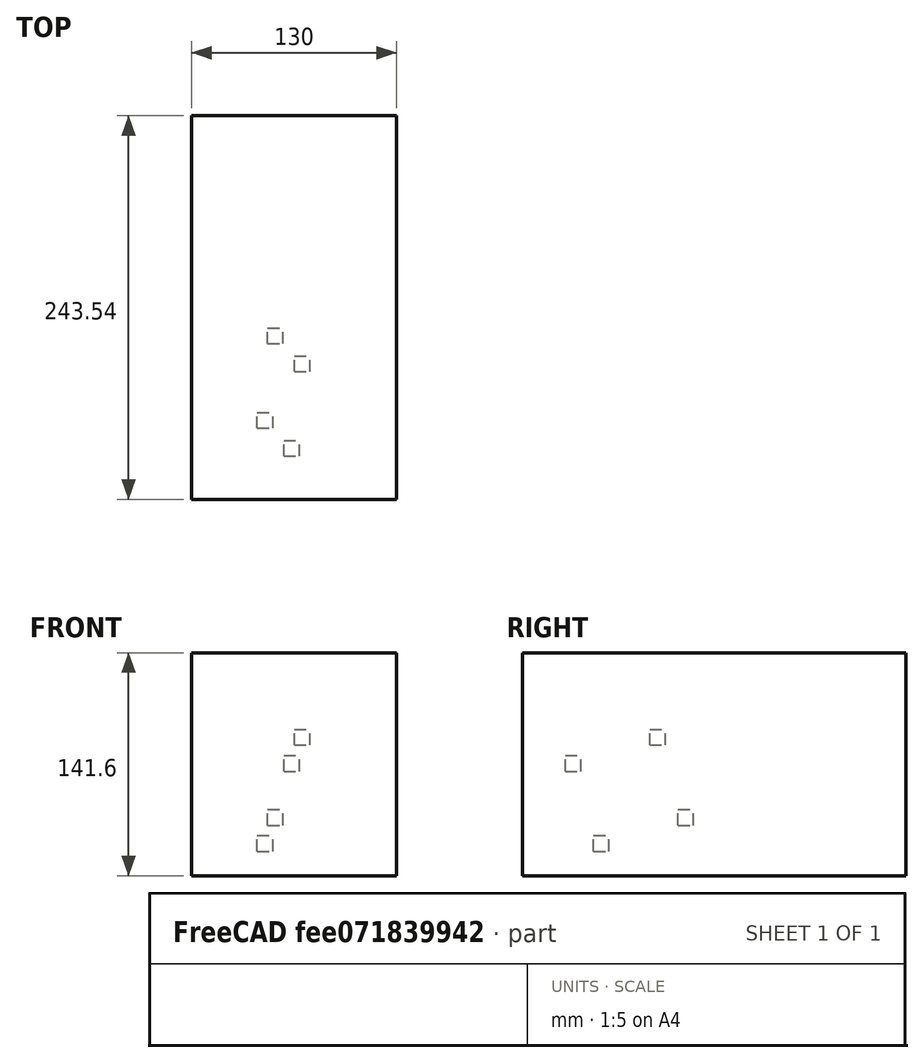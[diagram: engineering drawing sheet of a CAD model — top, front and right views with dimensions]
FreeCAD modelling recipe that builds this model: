
FCSTD DOCUMENT  (FreeCAD 1.0R39109 (Git))
Label: PathArray2
License: All rights reserved
LicenseURL: http://en.wikipedia.org/wiki/All_rights_reserved
objects: App::DocumentObjectGroupPython×1251, Part::FeaturePython×3, App::Part×2, Part::Part2DObjectPython×1
note: 4 computed .brp shape members not serialized (recipe doc carries the construction recipe); baked Part::Feature solids carry a one-line shape summary decoded from their .brp

FEATURE [App::DocumentObjectGroupPython] HALFPI  # scripted group (container) (typed FeaturePython)
  name = HALFPI
  value = pi/2.
FEATURE [App::DocumentObjectGroupPython] PI  # scripted group (container) (typed FeaturePython)
  name = PI
  value = 1.*pi
FEATURE [App::DocumentObjectGroupPython] TWOPI  # scripted group (container) (typed FeaturePython)
  name = TWOPI
  value = 2.*pi
FEATURE [App::DocumentObjectGroupPython] Constants  # scripted group (container) (typed FeaturePython)
  Group = -> [HALFPI,PI,TWOPI]
FEATURE [App::DocumentObjectGroupPython] Variables  # scripted group (container) (typed FeaturePython)
FEATURE [App::DocumentObjectGroupPython] Quantities  # scripted group (container) (typed FeaturePython)
FEATURE [App::DocumentObjectGroupPython] Isotopes  # scripted group (container) (typed FeaturePython)
FEATURE [App::DocumentObjectGroupPython] Elements  # scripted group (container) (typed FeaturePython)
FEATURE [App::DocumentObjectGroupPython] Matrix  # scripted group (container) (typed FeaturePython)
FEATURE [App::DocumentObjectGroupPython] Surfaces  # scripted group (container) (typed FeaturePython)
FEATURE [App::DocumentObjectGroupPython] Opticals  # scripted group (container) (typed FeaturePython)
  Group = -> [Matrix,Surfaces]
FEATURE [App::DocumentObjectGroupPython] G4Isotopes  # scripted group (container) (typed FeaturePython)
FEATURE [App::DocumentObjectGroupPython] H_element  # scripted group (container) (typed FeaturePython)
  Z = 1
  atom_value = 1.008
  formula = H
  name = H_element
FEATURE [App::DocumentObjectGroupPython] He_element  # scripted group (container) (typed FeaturePython)
  Z = 2
  atom_value = 4.0026
  formula = He
  name = He_element
FEATURE [App::DocumentObjectGroupPython] Li_element  # scripted group (container) (typed FeaturePython)
  Z = 3
  atom_value = 6.94
  formula = Li
  name = Li_element
FEATURE [App::DocumentObjectGroupPython] Be_element  # scripted group (container) (typed FeaturePython)
  Z = 4
  atom_value = 9.01218
  formula = Be
  name = Be_element
FEATURE [App::DocumentObjectGroupPython] B_element  # scripted group (container) (typed FeaturePython)
  Z = 5
  atom_value = 10.81
  formula = B
  name = B_element
FEATURE [App::DocumentObjectGroupPython] C_element  # scripted group (container) (typed FeaturePython)
  Z = 6
  atom_value = 12.011
  formula = C
  name = C_element
FEATURE [App::DocumentObjectGroupPython] N_element  # scripted group (container) (typed FeaturePython)
  Z = 7
  atom_value = 14.007
  formula = N
  name = N_element
FEATURE [App::DocumentObjectGroupPython] O_element  # scripted group (container) (typed FeaturePython)
  Z = 8
  atom_value = 15.999
  formula = O
  name = O_element
FEATURE [App::DocumentObjectGroupPython] F_element  # scripted group (container) (typed FeaturePython)
  Z = 9
  atom_value = 18.9984
  formula = F
  name = F_element
FEATURE [App::DocumentObjectGroupPython] Ne_element  # scripted group (container) (typed FeaturePython)
  Z = 10
  atom_value = 20.1797
  formula = Ne
  name = Ne_element
FEATURE [App::DocumentObjectGroupPython] Na_element  # scripted group (container) (typed FeaturePython)
  Z = 11
  atom_value = 22.9898
  formula = Na
  name = Na_element
FEATURE [App::DocumentObjectGroupPython] Mg_element  # scripted group (container) (typed FeaturePython)
  Z = 12
  atom_value = 24.305
  formula = Mg
  name = Mg_element
FEATURE [App::DocumentObjectGroupPython] Al_element  # scripted group (container) (typed FeaturePython)
  Z = 13
  atom_value = 26.9815
  formula = Al
  name = Al_element
FEATURE [App::DocumentObjectGroupPython] Si_element  # scripted group (container) (typed FeaturePython)
  Z = 14
  atom_value = 28.085
  formula = Si
  name = Si_element
FEATURE [App::DocumentObjectGroupPython] P_element  # scripted group (container) (typed FeaturePython)
  Z = 15
  atom_value = 30.9738
  formula = P
  name = P_element
FEATURE [App::DocumentObjectGroupPython] S_element  # scripted group (container) (typed FeaturePython)
  Z = 16
  atom_value = 32.06
  formula = S
  name = S_element
FEATURE [App::DocumentObjectGroupPython] Cl_element  # scripted group (container) (typed FeaturePython)
  Z = 17
  atom_value = 35.45
  formula = Cl
  name = Cl_element
FEATURE [App::DocumentObjectGroupPython] Ar_element  # scripted group (container) (typed FeaturePython)
  Z = 18
  atom_value = 39.95
  formula = Ar
  name = Ar_element
FEATURE [App::DocumentObjectGroupPython] K_element  # scripted group (container) (typed FeaturePython)
  Z = 19
  atom_value = 39.0983
  formula = K
  name = K_element
FEATURE [App::DocumentObjectGroupPython] Ca_element  # scripted group (container) (typed FeaturePython)
  Z = 20
  atom_value = 40.078
  formula = Ca
  name = Ca_element
FEATURE [App::DocumentObjectGroupPython] Sc_element  # scripted group (container) (typed FeaturePython)
  Z = 21
  atom_value = 44.9559
  formula = Sc
  name = Sc_element
FEATURE [App::DocumentObjectGroupPython] Ti_element  # scripted group (container) (typed FeaturePython)
  Z = 22
  atom_value = 47.867
  formula = Ti
  name = Ti_element
FEATURE [App::DocumentObjectGroupPython] V_element  # scripted group (container) (typed FeaturePython)
  Z = 23
  atom_value = 50.9415
  formula = V
  name = V_element
FEATURE [App::DocumentObjectGroupPython] Cr_element  # scripted group (container) (typed FeaturePython)
  Z = 24
  atom_value = 51.9961
  formula = Cr
  name = Cr_element
FEATURE [App::DocumentObjectGroupPython] Mn_element  # scripted group (container) (typed FeaturePython)
  Z = 25
  atom_value = 54.938
  formula = Mn
  name = Mn_element
FEATURE [App::DocumentObjectGroupPython] Fe_element  # scripted group (container) (typed FeaturePython)
  Z = 26
  atom_value = 55.845
  formula = Fe
  name = Fe_element
FEATURE [App::DocumentObjectGroupPython] Co_element  # scripted group (container) (typed FeaturePython)
  Z = 27
  atom_value = 58.9332
  formula = Co
  name = Co_element
FEATURE [App::DocumentObjectGroupPython] Ni_element  # scripted group (container) (typed FeaturePython)
  Z = 28
  atom_value = 58.6934
  formula = Ni
  name = Ni_element
FEATURE [App::DocumentObjectGroupPython] Cu_element  # scripted group (container) (typed FeaturePython)
  Z = 29
  atom_value = 63.546
  formula = Cu
  name = Cu_element
FEATURE [App::DocumentObjectGroupPython] Zn_element  # scripted group (container) (typed FeaturePython)
  Z = 30
  atom_value = 65.38
  formula = Zn
  name = Zn_element
FEATURE [App::DocumentObjectGroupPython] Ga_element  # scripted group (container) (typed FeaturePython)
  Z = 31
  atom_value = 69.723
  formula = Ga
  name = Ga_element
FEATURE [App::DocumentObjectGroupPython] Ge_element  # scripted group (container) (typed FeaturePython)
  Z = 32
  atom_value = 72.63
  formula = Ge
  name = Ge_element
FEATURE [App::DocumentObjectGroupPython] As_element  # scripted group (container) (typed FeaturePython)
  Z = 33
  atom_value = 74.9216
  formula = As
  name = As_element
FEATURE [App::DocumentObjectGroupPython] Se_element  # scripted group (container) (typed FeaturePython)
  Z = 34
  atom_value = 78.971
  formula = Se
  name = Se_element
FEATURE [App::DocumentObjectGroupPython] Br_element  # scripted group (container) (typed FeaturePython)
  Z = 35
  atom_value = 79.904
  formula = Br
  name = Br_element
FEATURE [App::DocumentObjectGroupPython] Kr_element  # scripted group (container) (typed FeaturePython)
  Z = 36
  atom_value = 83.798
  formula = Kr
  name = Kr_element
FEATURE [App::DocumentObjectGroupPython] Rb_element  # scripted group (container) (typed FeaturePython)
  Z = 37
  atom_value = 85.4678
  formula = Rb
  name = Rb_element
FEATURE [App::DocumentObjectGroupPython] Sr_element  # scripted group (container) (typed FeaturePython)
  Z = 38
  atom_value = 87.62
  formula = Sr
  name = Sr_element
FEATURE [App::DocumentObjectGroupPython] Y_element  # scripted group (container) (typed FeaturePython)
  Z = 39
  atom_value = 88.9058
  formula = Y
  name = Y_element
FEATURE [App::DocumentObjectGroupPython] Zr_element  # scripted group (container) (typed FeaturePython)
  Z = 40
  atom_value = 91.224
  formula = Zr
  name = Zr_element
FEATURE [App::DocumentObjectGroupPython] Nb_element  # scripted group (container) (typed FeaturePython)
  Z = 41
  atom_value = 92.9064
  formula = Nb
  name = Nb_element
FEATURE [App::DocumentObjectGroupPython] Mo_element  # scripted group (container) (typed FeaturePython)
  Z = 42
  atom_value = 95.95
  formula = Mo
  name = Mo_element
FEATURE [App::DocumentObjectGroupPython] Tc_element  # scripted group (container) (typed FeaturePython)
  Z = 43
  atom_value = 97
  formula = Tc
  name = Tc_element
FEATURE [App::DocumentObjectGroupPython] Ru_element  # scripted group (container) (typed FeaturePython)
  Z = 44
  atom_value = 101.07
  formula = Ru
  name = Ru_element
FEATURE [App::DocumentObjectGroupPython] Rh_element  # scripted group (container) (typed FeaturePython)
  Z = 45
  atom_value = 102.905
  formula = Rh
  name = Rh_element
FEATURE [App::DocumentObjectGroupPython] Pd_element  # scripted group (container) (typed FeaturePython)
  Z = 46
  atom_value = 106.42
  formula = Pd
  name = Pd_element
FEATURE [App::DocumentObjectGroupPython] Ag_element  # scripted group (container) (typed FeaturePython)
  Z = 47
  atom_value = 107.868
  formula = Ag
  name = Ag_element
FEATURE [App::DocumentObjectGroupPython] Cd_element  # scripted group (container) (typed FeaturePython)
  Z = 48
  atom_value = 112.414
  formula = Cd
  name = Cd_element
FEATURE [App::DocumentObjectGroupPython] In_element  # scripted group (container) (typed FeaturePython)
  Z = 49
  atom_value = 114.818
  formula = In
  name = In_element
FEATURE [App::DocumentObjectGroupPython] Sn_element  # scripted group (container) (typed FeaturePython)
  Z = 50
  atom_value = 118.71
  formula = Sn
  name = Sn_element
FEATURE [App::DocumentObjectGroupPython] Sb_element  # scripted group (container) (typed FeaturePython)
  Z = 51
  atom_value = 121.76
  formula = Sb
  name = Sb_element
FEATURE [App::DocumentObjectGroupPython] Te_element  # scripted group (container) (typed FeaturePython)
  Z = 52
  atom_value = 127.6
  formula = Te
  name = Te_element
FEATURE [App::DocumentObjectGroupPython] I_element  # scripted group (container) (typed FeaturePython)
  Z = 53
  atom_value = 126.904
  formula = I
  name = I_element
FEATURE [App::DocumentObjectGroupPython] Xe_element  # scripted group (container) (typed FeaturePython)
  Z = 54
  atom_value = 131.293
  formula = Xe
  name = Xe_element
FEATURE [App::DocumentObjectGroupPython] Cs_element  # scripted group (container) (typed FeaturePython)
  Z = 55
  atom_value = 132.905
  formula = Cs
  name = Cs_element
FEATURE [App::DocumentObjectGroupPython] Ba_element  # scripted group (container) (typed FeaturePython)
  Z = 56
  atom_value = 137.327
  formula = Ba
  name = Ba_element
FEATURE [App::DocumentObjectGroupPython] La_element  # scripted group (container) (typed FeaturePython)
  Z = 57
  atom_value = 138.905
  formula = La
  name = La_element
FEATURE [App::DocumentObjectGroupPython] Ce_element  # scripted group (container) (typed FeaturePython)
  Z = 58
  atom_value = 140.116
  formula = Ce
  name = Ce_element
FEATURE [App::DocumentObjectGroupPython] Pr_element  # scripted group (container) (typed FeaturePython)
  Z = 59
  atom_value = 140.908
  formula = Pr
  name = Pr_element
FEATURE [App::DocumentObjectGroupPython] Nd_element  # scripted group (container) (typed FeaturePython)
  Z = 60
  atom_value = 144.242
  formula = Nd
  name = Nd_element
FEATURE [App::DocumentObjectGroupPython] Pm_element  # scripted group (container) (typed FeaturePython)
  Z = 61
  atom_value = 145
  formula = Pm
  name = Pm_element
FEATURE [App::DocumentObjectGroupPython] Sm_element  # scripted group (container) (typed FeaturePython)
  Z = 62
  atom_value = 150.36
  formula = Sm
  name = Sm_element
FEATURE [App::DocumentObjectGroupPython] Eu_element  # scripted group (container) (typed FeaturePython)
  Z = 63
  atom_value = 151.964
  formula = Eu
  name = Eu_element
FEATURE [App::DocumentObjectGroupPython] Gd_element  # scripted group (container) (typed FeaturePython)
  Z = 64
  atom_value = 157.25
  formula = Gd
  name = Gd_element
FEATURE [App::DocumentObjectGroupPython] Tb_element  # scripted group (container) (typed FeaturePython)
  Z = 65
  atom_value = 158.925
  formula = Tb
  name = Tb_element
FEATURE [App::DocumentObjectGroupPython] Dy_element  # scripted group (container) (typed FeaturePython)
  Z = 66
  atom_value = 162.5
  formula = Dy
  name = Dy_element
FEATURE [App::DocumentObjectGroupPython] Ho_element  # scripted group (container) (typed FeaturePython)
  Z = 67
  atom_value = 164.93
  formula = Ho
  name = Ho_element
FEATURE [App::DocumentObjectGroupPython] Er_element  # scripted group (container) (typed FeaturePython)
  Z = 68
  atom_value = 167.259
  formula = Er
  name = Er_element
FEATURE [App::DocumentObjectGroupPython] Tm_element  # scripted group (container) (typed FeaturePython)
  Z = 69
  atom_value = 168.934
  formula = Tm
  name = Tm_element
FEATURE [App::DocumentObjectGroupPython] Yb_element  # scripted group (container) (typed FeaturePython)
  Z = 70
  atom_value = 173.045
  formula = Yb
  name = Yb_element
FEATURE [App::DocumentObjectGroupPython] Lu_element  # scripted group (container) (typed FeaturePython)
  Z = 71
  atom_value = 174.967
  formula = Lu
  name = Lu_element
FEATURE [App::DocumentObjectGroupPython] Hf_element  # scripted group (container) (typed FeaturePython)
  Z = 72
  atom_value = 178.49
  formula = Hf
  name = Hf_element
FEATURE [App::DocumentObjectGroupPython] Ta_element  # scripted group (container) (typed FeaturePython)
  Z = 73
  atom_value = 180.948
  formula = Ta
  name = Ta_element
FEATURE [App::DocumentObjectGroupPython] W_element  # scripted group (container) (typed FeaturePython)
  Z = 74
  atom_value = 183.84
  formula = W
  name = W_element
FEATURE [App::DocumentObjectGroupPython] Re_element  # scripted group (container) (typed FeaturePython)
  Z = 75
  atom_value = 186.207
  formula = Re
  name = Re_element
FEATURE [App::DocumentObjectGroupPython] Os_element  # scripted group (container) (typed FeaturePython)
  Z = 76
  atom_value = 190.23
  formula = Os
  name = Os_element
FEATURE [App::DocumentObjectGroupPython] Ir_element  # scripted group (container) (typed FeaturePython)
  Z = 77
  atom_value = 192.217
  formula = Ir
  name = Ir_element
FEATURE [App::DocumentObjectGroupPython] Pt_element  # scripted group (container) (typed FeaturePython)
  Z = 78
  atom_value = 195.084
  formula = Pt
  name = Pt_element
FEATURE [App::DocumentObjectGroupPython] Au_element  # scripted group (container) (typed FeaturePython)
  Z = 79
  atom_value = 196.967
  formula = Au
  name = Au_element
FEATURE [App::DocumentObjectGroupPython] Hg_element  # scripted group (container) (typed FeaturePython)
  Z = 80
  atom_value = 200.592
  formula = Hg
  name = Hg_element
FEATURE [App::DocumentObjectGroupPython] Tl_element  # scripted group (container) (typed FeaturePython)
  Z = 81
  atom_value = 204.38
  formula = Tl
  name = Tl_element
FEATURE [App::DocumentObjectGroupPython] Pb_element  # scripted group (container) (typed FeaturePython)
  Z = 82
  atom_value = 207.2
  formula = Pb
  name = Pb_element
FEATURE [App::DocumentObjectGroupPython] Bi_element  # scripted group (container) (typed FeaturePython)
  Z = 83
  atom_value = 208.98
  formula = Bi
  name = Bi_element
FEATURE [App::DocumentObjectGroupPython] Po_element  # scripted group (container) (typed FeaturePython)
  Z = 84
  atom_value = 209
  formula = Po
  name = Po_element
FEATURE [App::DocumentObjectGroupPython] At_element  # scripted group (container) (typed FeaturePython)
  Z = 85
  atom_value = 210
  formula = At
  name = At_element
FEATURE [App::DocumentObjectGroupPython] Rn_element  # scripted group (container) (typed FeaturePython)
  Z = 86
  atom_value = 222
  formula = Rn
  name = Rn_element
FEATURE [App::DocumentObjectGroupPython] Fr_element  # scripted group (container) (typed FeaturePython)
  Z = 87
  atom_value = 223
  formula = Fr
  name = Fr_element
FEATURE [App::DocumentObjectGroupPython] Ra_element  # scripted group (container) (typed FeaturePython)
  Z = 88
  atom_value = 226
  formula = Ra
  name = Ra_element
FEATURE [App::DocumentObjectGroupPython] Ac_element  # scripted group (container) (typed FeaturePython)
  Z = 89
  atom_value = 227
  formula = Ac
  name = Ac_element
FEATURE [App::DocumentObjectGroupPython] Th_element  # scripted group (container) (typed FeaturePython)
  Z = 90
  atom_value = 232.038
  formula = Th
  name = Th_element
FEATURE [App::DocumentObjectGroupPython] Pa_element  # scripted group (container) (typed FeaturePython)
  Z = 91
  atom_value = 231.036
  formula = Pa
  name = Pa_element
FEATURE [App::DocumentObjectGroupPython] U_element  # scripted group (container) (typed FeaturePython)
  Z = 92
  atom_value = 238.029
  formula = U
  name = U_element
FEATURE [App::DocumentObjectGroupPython] Np_element  # scripted group (container) (typed FeaturePython)
  Z = 93
  atom_value = 237
  formula = Np
  name = Np_element
FEATURE [App::DocumentObjectGroupPython] Pu_element  # scripted group (container) (typed FeaturePython)
  Z = 94
  atom_value = 244
  formula = Pu
  name = Pu_element
FEATURE [App::DocumentObjectGroupPython] Am_element  # scripted group (container) (typed FeaturePython)
  Z = 95
  atom_value = 243
  formula = Am
  name = Am_element
FEATURE [App::DocumentObjectGroupPython] Cm_element  # scripted group (container) (typed FeaturePython)
  Z = 96
  atom_value = 247
  formula = Cm
  name = Cm_element
FEATURE [App::DocumentObjectGroupPython] Bk_element  # scripted group (container) (typed FeaturePython)
  Z = 97
  atom_value = 247
  formula = Bk
  name = Bk_element
FEATURE [App::DocumentObjectGroupPython] Cf_element  # scripted group (container) (typed FeaturePython)
  Z = 98
  atom_value = 251
  formula = Cf
  name = Cf_element
FEATURE [App::DocumentObjectGroupPython] G4Elements  # scripted group (container) (typed FeaturePython)
  Group = -> [H_element,He_element,Li_element,Be_element,B_element,C_element,N_element,O_element,F_element,Ne_element,Na_element,Mg_element,Al_element,Si_element,P_element,S_element,Cl_element,Ar_element,K_element,Ca_element,Sc_element,Ti_element,V_element,Cr_element,Mn_element,Fe_element,Co_element,Ni_element,Cu_element,Zn_element,Ga_element,Ge_element,As_element,Se_element,Br_element,Kr_element,Rb_element,+61 more]
FEATURE [App::DocumentObjectGroupPython] H_element001  label="H_element : 0.101"  # scripted group (container) (typed FeaturePython)
  n = 0.101327
FEATURE [App::DocumentObjectGroupPython] C_element001  label="C_element : 0.775"  # scripted group (container) (typed FeaturePython)
  n = 0.7755
FEATURE [App::DocumentObjectGroupPython] N_element001  label="N_element : 0.035"  # scripted group (container) (typed FeaturePython)
  n = 0.035057
FEATURE [App::DocumentObjectGroupPython] O_element001  label="O_element : 0.052"  # scripted group (container) (typed FeaturePython)
  n = 0.0523159
FEATURE [App::DocumentObjectGroupPython] F_element001  label="F_element : 0.017"  # scripted group (container) (typed FeaturePython)
  n = 0.017422
FEATURE [App::DocumentObjectGroupPython] Ca_element001  label="Ca_element : 0.018"  # scripted group (container) (typed FeaturePython)
  n = 0.018378
FEATURE [App::DocumentObjectGroupPython] G4_A_150_TISSUE  label="G4_A-150_TISSUE"  # scripted group (container) (typed FeaturePython)
  Dunit = g/cm3
  Dvalue = 1.127
  Group = -> [H_element001,C_element001,N_element001,O_element001,F_element001,Ca_element001]
  conduct = 2
  density = 1
  expand = 3
  formula = G4_A-150_TISSUE
  name = G4_A-150_TISSUE
  specific = 4
FEATURE [App::DocumentObjectGroupPython] C_element002  label="C_element : 3"  # scripted group (container) (typed FeaturePython)
  n = 3
  ref = C_element
FEATURE [App::DocumentObjectGroupPython] H_element002  label="H_element : 6"  # scripted group (container) (typed FeaturePython)
  n = 6
  ref = H_element
FEATURE [App::DocumentObjectGroupPython] O_element002  label="O_element : 1"  # scripted group (container) (typed FeaturePython)
  n = 1
  ref = O_element
FEATURE [App::DocumentObjectGroupPython] G4_ACETONE  # scripted group (container) (typed FeaturePython)
  Dunit = g/cm3
  Dvalue = 0.7899
  Group = -> [C_element002,H_element002,O_element002]
  conduct = 2
  density = 1
  expand = 3
  formula = G4_ACETONE
  name = G4_ACETONE
  specific = 4
FEATURE [App::DocumentObjectGroupPython] C_element003  label="C_element : 2"  # scripted group (container) (typed FeaturePython)
  n = 2
  ref = C_element
FEATURE [App::DocumentObjectGroupPython] H_element003  label="H_element : 2"  # scripted group (container) (typed FeaturePython)
  n = 2
  ref = H_element
FEATURE [App::DocumentObjectGroupPython] G4_ACETYLENE  # scripted group (container) (typed FeaturePython)
  Dunit = g/cm3
  Dvalue = 0.0010967
  Group = -> [C_element003,H_element003]
  conduct = 2
  density = 1
  expand = 3
  formula = G4_ACETYLENE
  name = G4_ACETYLENE
  specific = 4
FEATURE [App::DocumentObjectGroupPython] C_element004  label="C_element : 5"  # scripted group (container) (typed FeaturePython)
  n = 5
  ref = C_element
FEATURE [App::DocumentObjectGroupPython] H_element004  label="H_element : 5"  # scripted group (container) (typed FeaturePython)
  n = 5
  ref = H_element
FEATURE [App::DocumentObjectGroupPython] N_element002  label="N_element : 5"  # scripted group (container) (typed FeaturePython)
  n = 5
  ref = N_element
FEATURE [App::DocumentObjectGroupPython] G4_ADENINE  # scripted group (container) (typed FeaturePython)
  Dunit = g/cm3
  Dvalue = 1.6
  Group = -> [C_element004,H_element004,N_element002]
  conduct = 2
  density = 1
  expand = 3
  formula = G4_ADENINE
  name = G4_ADENINE
  specific = 4
FEATURE [App::DocumentObjectGroupPython] H_element005  label="H_element : 0.114"  # scripted group (container) (typed FeaturePython)
  n = 0.114
FEATURE [App::DocumentObjectGroupPython] C_element005  label="C_element : 0.598"  # scripted group (container) (typed FeaturePython)
  n = 0.598
FEATURE [App::DocumentObjectGroupPython] N_element003  label="N_element : 0.007"  # scripted group (container) (typed FeaturePython)
  n = 0.007
FEATURE [App::DocumentObjectGroupPython] O_element003  label="O_element : 0.278"  # scripted group (container) (typed FeaturePython)
  n = 0.278
FEATURE [App::DocumentObjectGroupPython] Na_element001  label="Na_element : 0.001"  # scripted group (container) (typed FeaturePython)
  n = 0.001
FEATURE [App::DocumentObjectGroupPython] S_element001  label="S_element : 0.001"  # scripted group (container) (typed FeaturePython)
  n = 0.001
FEATURE [App::DocumentObjectGroupPython] Cl_element001  label="Cl_element : 0.001"  # scripted group (container) (typed FeaturePython)
  n = 0.001
FEATURE [App::DocumentObjectGroupPython] G4_ADIPOSE_TISSUE_ICRP  # scripted group (container) (typed FeaturePython)
  Dunit = g/cm3
  Dvalue = 0.95
  Group = -> [H_element005,C_element005,N_element003,O_element003,Na_element001,S_element001,Cl_element001]
  conduct = 2
  density = 1
  expand = 3
  formula = G4_ADIPOSE_TISSUE_ICRP
  name = G4_ADIPOSE_TISSUE_ICRP
  specific = 4
FEATURE [App::DocumentObjectGroupPython] C_element006  label="C_element : 0.000"  # scripted group (container) (typed FeaturePython)
  n = 0.000124
FEATURE [App::DocumentObjectGroupPython] N_element004  label="N_element : 0.755"  # scripted group (container) (typed FeaturePython)
  n = 0.755268
FEATURE [App::DocumentObjectGroupPython] O_element004  label="O_element : 0.232"  # scripted group (container) (typed FeaturePython)
  n = 0.231781
FEATURE [App::DocumentObjectGroupPython] Ar_element001  label="Ar_element : 0.013"  # scripted group (container) (typed FeaturePython)
  n = 0.012827
FEATURE [App::DocumentObjectGroupPython] G4_AIR  # scripted group (container) (typed FeaturePython)
  Dunit = g/cm3
  Dvalue = 0.00120479
  Group = -> [C_element006,N_element004,O_element004,Ar_element001]
  conduct = 2
  density = 1
  expand = 3
  formula = G4_AIR
  name = G4_AIR
  specific = 4
FEATURE [App::DocumentObjectGroupPython] C_element007  label="C_element : 006"  # scripted group (container) (typed FeaturePython)
  n = 3
  ref = C_element
FEATURE [App::DocumentObjectGroupPython] H_element006  label="H_element : 7"  # scripted group (container) (typed FeaturePython)
  n = 7
  ref = H_element
FEATURE [App::DocumentObjectGroupPython] N_element005  label="N_element : 1"  # scripted group (container) (typed FeaturePython)
  n = 1
  ref = N_element
FEATURE [App::DocumentObjectGroupPython] O_element005  label="O_element : 2"  # scripted group (container) (typed FeaturePython)
  n = 2
  ref = O_element
FEATURE [App::DocumentObjectGroupPython] G4_ALANINE  # scripted group (container) (typed FeaturePython)
  Dunit = g/cm3
  Dvalue = 1.42
  Group = -> [C_element007,H_element006,N_element005,O_element005]
  conduct = 2
  density = 1
  expand = 3
  formula = G4_ALANINE
  name = G4_ALANINE
  specific = 4
FEATURE [App::DocumentObjectGroupPython] Al_element001  label="Al_element : 2"  # scripted group (container) (typed FeaturePython)
  n = 2
  ref = Al_element
FEATURE [App::DocumentObjectGroupPython] O_element006  label="O_element : 3"  # scripted group (container) (typed FeaturePython)
  n = 3
  ref = O_element
FEATURE [App::DocumentObjectGroupPython] G4_ALUMINUM_OXIDE  # scripted group (container) (typed FeaturePython)
  Dunit = g/cm3
  Dvalue = 3.97
  Group = -> [Al_element001,O_element006]
  conduct = 2
  density = 1
  expand = 3
  formula = G4_ALUMINUM_OXIDE
  name = G4_ALUMINUM_OXIDE
  specific = 4
FEATURE [App::DocumentObjectGroupPython] H_element007  label="H_element : 0.106"  # scripted group (container) (typed FeaturePython)
  n = 0.10593
FEATURE [App::DocumentObjectGroupPython] C_element008  label="C_element : 0.789"  # scripted group (container) (typed FeaturePython)
  n = 0.788974
FEATURE [App::DocumentObjectGroupPython] O_element007  label="O_element : 0.105"  # scripted group (container) (typed FeaturePython)
  n = 0.105096
FEATURE [App::DocumentObjectGroupPython] G4_AMBER  # scripted group (container) (typed FeaturePython)
  Dunit = g/cm3
  Dvalue = 1.1
  Group = -> [H_element007,C_element008,O_element007]
  conduct = 2
  density = 1
  expand = 3
  formula = G4_AMBER
  name = G4_AMBER
  specific = 4
FEATURE [App::DocumentObjectGroupPython] N_element006  label="N_element : 006"  # scripted group (container) (typed FeaturePython)
  n = 1
  ref = N_element
FEATURE [App::DocumentObjectGroupPython] H_element008  label="H_element : 3"  # scripted group (container) (typed FeaturePython)
  n = 3
  ref = H_element
FEATURE [App::DocumentObjectGroupPython] G4_AMMONIA  # scripted group (container) (typed FeaturePython)
  Dunit = g/cm3
  Dvalue = 0.000826019
  Group = -> [N_element006,H_element008]
  conduct = 2
  density = 1
  expand = 3
  formula = G4_AMMONIA
  name = G4_AMMONIA
  specific = 4
FEATURE [App::DocumentObjectGroupPython] C_element009  label="C_element : 6"  # scripted group (container) (typed FeaturePython)
  n = 6
  ref = C_element
FEATURE [App::DocumentObjectGroupPython] H_element009  label="H_element : 008"  # scripted group (container) (typed FeaturePython)
  n = 7
  ref = H_element
FEATURE [App::DocumentObjectGroupPython] N_element007  label="N_element : 007"  # scripted group (container) (typed FeaturePython)
  n = 1
  ref = N_element
FEATURE [App::DocumentObjectGroupPython] G4_ANILINE  # scripted group (container) (typed FeaturePython)
  Dunit = g/cm3
  Dvalue = 1.0235
  Group = -> [C_element009,H_element009,N_element007]
  conduct = 2
  density = 1
  expand = 3
  formula = G4_ANILINE
  name = G4_ANILINE
  specific = 4
FEATURE [App::DocumentObjectGroupPython] C_element010  label="C_element : 14"  # scripted group (container) (typed FeaturePython)
  n = 14
  ref = C_element
FEATURE [App::DocumentObjectGroupPython] H_element010  label="H_element : 10"  # scripted group (container) (typed FeaturePython)
  n = 10
  ref = H_element
FEATURE [App::DocumentObjectGroupPython] G4_ANTHRACENE  # scripted group (container) (typed FeaturePython)
  Dunit = g/cm3
  Dvalue = 1.283
  Group = -> [C_element010,H_element010]
  conduct = 2
  density = 1
  expand = 3
  formula = G4_ANTHRACENE
  name = G4_ANTHRACENE
  specific = 4
FEATURE [App::DocumentObjectGroupPython] H_element011  label="H_element : 0.065"  # scripted group (container) (typed FeaturePython)
  n = 0.0654709
FEATURE [App::DocumentObjectGroupPython] C_element011  label="C_element : 0.537"  # scripted group (container) (typed FeaturePython)
  n = 0.536944
FEATURE [App::DocumentObjectGroupPython] N_element008  label="N_element : 0.021"  # scripted group (container) (typed FeaturePython)
  n = 0.0215
FEATURE [App::DocumentObjectGroupPython] O_element008  label="O_element : 0.032"  # scripted group (container) (typed FeaturePython)
  n = 0.032085
FEATURE [App::DocumentObjectGroupPython] F_element002  label="F_element : 0.167"  # scripted group (container) (typed FeaturePython)
  n = 0.167411
FEATURE [App::DocumentObjectGroupPython] Ca_element002  label="Ca_element : 0.177"  # scripted group (container) (typed FeaturePython)
  n = 0.176589
FEATURE [App::DocumentObjectGroupPython] G4_B_100_BONE  label="G4_B-100_BONE"  # scripted group (container) (typed FeaturePython)
  Dunit = g/cm3
  Dvalue = 1.45
  Group = -> [H_element011,C_element011,N_element008,O_element008,F_element002,Ca_element002]
  conduct = 2
  density = 1
  expand = 3
  formula = G4_B-100_BONE
  name = G4_B-100_BONE
  specific = 4
FEATURE [App::DocumentObjectGroupPython] H_element012  label="H_element : 0.057"  # scripted group (container) (typed FeaturePython)
  n = 0.057441
FEATURE [App::DocumentObjectGroupPython] C_element012  label="C_element : 0.790"  # scripted group (container) (typed FeaturePython)
  n = 0.774591
FEATURE [App::DocumentObjectGroupPython] O_element009  label="O_element : 0.168"  # scripted group (container) (typed FeaturePython)
  n = 0.167968
FEATURE [App::DocumentObjectGroupPython] G4_BAKELITE  # scripted group (container) (typed FeaturePython)
  Dunit = g/cm3
  Dvalue = 1.25
  Group = -> [H_element012,C_element012,O_element009]
  conduct = 2
  density = 1
  expand = 3
  formula = G4_BAKELITE
  name = G4_BAKELITE
  specific = 4
FEATURE [App::DocumentObjectGroupPython] Ba_element001  label="Ba_element : 1"  # scripted group (container) (typed FeaturePython)
  n = 1
  ref = Ba_element
FEATURE [App::DocumentObjectGroupPython] F_element003  label="F_element : 2"  # scripted group (container) (typed FeaturePython)
  n = 2
  ref = F_element
FEATURE [App::DocumentObjectGroupPython] G4_BARIUM_FLUORIDE  # scripted group (container) (typed FeaturePython)
  Dunit = g/cm3
  Dvalue = 4.89
  Group = -> [Ba_element001,F_element003]
  conduct = 2
  density = 1
  expand = 3
  formula = G4_BARIUM_FLUORIDE
  name = G4_BARIUM_FLUORIDE
  specific = 4
FEATURE [App::DocumentObjectGroupPython] Ba_element002  label="Ba_element : 002"  # scripted group (container) (typed FeaturePython)
  n = 1
  ref = Ba_element
FEATURE [App::DocumentObjectGroupPython] S_element002  label="S_element : 1"  # scripted group (container) (typed FeaturePython)
  n = 1
  ref = S_element
FEATURE [App::DocumentObjectGroupPython] O_element010  label="O_element : 4"  # scripted group (container) (typed FeaturePython)
  n = 4
  ref = O_element
FEATURE [App::DocumentObjectGroupPython] G4_BARIUM_SULFATE  # scripted group (container) (typed FeaturePython)
  Dunit = g/cm3
  Dvalue = 4.5
  Group = -> [Ba_element002,S_element002,O_element010]
  conduct = 2
  density = 1
  expand = 3
  formula = G4_BARIUM_SULFATE
  name = G4_BARIUM_SULFATE
  specific = 4
FEATURE [App::DocumentObjectGroupPython] C_element013  label="C_element : 007"  # scripted group (container) (typed FeaturePython)
  n = 6
  ref = C_element
FEATURE [App::DocumentObjectGroupPython] H_element013  label="H_element : 009"  # scripted group (container) (typed FeaturePython)
  n = 6
  ref = H_element
FEATURE [App::DocumentObjectGroupPython] G4_BENZENE  # scripted group (container) (typed FeaturePython)
  Dunit = g/cm3
  Dvalue = 0.87865
  Group = -> [C_element013,H_element013]
  conduct = 2
  density = 1
  expand = 3
  formula = G4_BENZENE
  name = G4_BENZENE
  specific = 4
FEATURE [App::DocumentObjectGroupPython] Be_element001  label="Be_element : 1"  # scripted group (container) (typed FeaturePython)
  n = 1
  ref = Be_element
FEATURE [App::DocumentObjectGroupPython] O_element011  label="O_element : 005"  # scripted group (container) (typed FeaturePython)
  n = 1
  ref = O_element
FEATURE [App::DocumentObjectGroupPython] G4_BERYLLIUM_OXIDE  # scripted group (container) (typed FeaturePython)
  Dunit = g/cm3
  Dvalue = 3.01
  Group = -> [Be_element001,O_element011]
  conduct = 2
  density = 1
  expand = 3
  formula = G4_BERYLLIUM_OXIDE
  name = G4_BERYLLIUM_OXIDE
  specific = 4
FEATURE [App::DocumentObjectGroupPython] Bi_element001  label="Bi_element : 4"  # scripted group (container) (typed FeaturePython)
  n = 4
  ref = Bi_element
FEATURE [App::DocumentObjectGroupPython] Ge_element001  label="Ge_element : 3"  # scripted group (container) (typed FeaturePython)
  n = 3
  ref = Ge_element
FEATURE [App::DocumentObjectGroupPython] O_element012  label="O_element : 12"  # scripted group (container) (typed FeaturePython)
  n = 12
  ref = O_element
FEATURE [App::DocumentObjectGroupPython] G4_BGO  # scripted group (container) (typed FeaturePython)
  Dunit = g/cm3
  Dvalue = 7.13
  Group = -> [Bi_element001,Ge_element001,O_element012]
  conduct = 2
  density = 1
  expand = 3
  formula = G4_BGO
  name = G4_BGO
  specific = 4
FEATURE [App::DocumentObjectGroupPython] H_element014  label="H_element : 0.102"  # scripted group (container) (typed FeaturePython)
  n = 0.102
FEATURE [App::DocumentObjectGroupPython] C_element014  label="C_element : 0.110"  # scripted group (container) (typed FeaturePython)
  n = 0.11
FEATURE [App::DocumentObjectGroupPython] N_element009  label="N_element : 0.033"  # scripted group (container) (typed FeaturePython)
  n = 0.033
FEATURE [App::DocumentObjectGroupPython] O_element013  label="O_element : 0.745"  # scripted group (container) (typed FeaturePython)
  n = 0.745
FEATURE [App::DocumentObjectGroupPython] Na_element002  label="Na_element : 0.002"  # scripted group (container) (typed FeaturePython)
  n = 0.001
FEATURE [App::DocumentObjectGroupPython] P_element001  label="P_element : 0.001"  # scripted group (container) (typed FeaturePython)
  n = 0.001
FEATURE [App::DocumentObjectGroupPython] S_element003  label="S_element : 0.002"  # scripted group (container) (typed FeaturePython)
  n = 0.002
FEATURE [App::DocumentObjectGroupPython] Cl_element002  label="Cl_element : 0.003"  # scripted group (container) (typed FeaturePython)
  n = 0.003
FEATURE [App::DocumentObjectGroupPython] K_element001  label="K_element : 0.002"  # scripted group (container) (typed FeaturePython)
  n = 0.002
FEATURE [App::DocumentObjectGroupPython] Fe_element001  label="Fe_element : 0.001"  # scripted group (container) (typed FeaturePython)
  n = 0.001
FEATURE [App::DocumentObjectGroupPython] G4_BLOOD_ICRP  # scripted group (container) (typed FeaturePython)
  Dunit = g/cm3
  Dvalue = 1.06
  Group = -> [H_element014,C_element014,N_element009,O_element013,Na_element002,P_element001,S_element003,Cl_element002,K_element001,Fe_element001]
  conduct = 2
  density = 1
  expand = 3
  formula = G4_BLOOD_ICRP
  name = G4_BLOOD_ICRP
  specific = 4
FEATURE [App::DocumentObjectGroupPython] H_element015  label="H_element : 0.064"  # scripted group (container) (typed FeaturePython)
  n = 0.064
FEATURE [App::DocumentObjectGroupPython] C_element015  label="C_element : 0.278"  # scripted group (container) (typed FeaturePython)
  n = 0.278
FEATURE [App::DocumentObjectGroupPython] N_element010  label="N_element : 0.027"  # scripted group (container) (typed FeaturePython)
  n = 0.027
FEATURE [App::DocumentObjectGroupPython] O_element014  label="O_element : 0.410"  # scripted group (container) (typed FeaturePython)
  n = 0.41
FEATURE [App::DocumentObjectGroupPython] Mg_element001  label="Mg_element : 0.002"  # scripted group (container) (typed FeaturePython)
  n = 0.002
FEATURE [App::DocumentObjectGroupPython] P_element002  label="P_element : 0.070"  # scripted group (container) (typed FeaturePython)
  n = 0.07
FEATURE [App::DocumentObjectGroupPython] S_element004  label="S_element : 0.003"  # scripted group (container) (typed FeaturePython)
  n = 0.002
FEATURE [App::DocumentObjectGroupPython] Ca_element003  label="Ca_element : 0.147"  # scripted group (container) (typed FeaturePython)
  n = 0.147
FEATURE [App::DocumentObjectGroupPython] G4_BONE_COMPACT_ICRU  # scripted group (container) (typed FeaturePython)
  Dunit = g/cm3
  Dvalue = 1.85
  Group = -> [H_element015,C_element015,N_element010,O_element014,Mg_element001,P_element002,S_element004,Ca_element003]
  conduct = 2
  density = 1
  expand = 3
  formula = G4_BONE_COMPACT_ICRU
  name = G4_BONE_COMPACT_ICRU
  specific = 4
FEATURE [App::DocumentObjectGroupPython] H_element016  label="H_element : 0.034"  # scripted group (container) (typed FeaturePython)
  n = 0.034
FEATURE [App::DocumentObjectGroupPython] C_element016  label="C_element : 0.155"  # scripted group (container) (typed FeaturePython)
  n = 0.155
FEATURE [App::DocumentObjectGroupPython] N_element011  label="N_element : 0.042"  # scripted group (container) (typed FeaturePython)
  n = 0.042
FEATURE [App::DocumentObjectGroupPython] O_element015  label="O_element : 0.435"  # scripted group (container) (typed FeaturePython)
  n = 0.435
FEATURE [App::DocumentObjectGroupPython] Na_element003  label="Na_element : 0.003"  # scripted group (container) (typed FeaturePython)
  n = 0.001
FEATURE [App::DocumentObjectGroupPython] Mg_element002  label="Mg_element : 0.003"  # scripted group (container) (typed FeaturePython)
  n = 0.002
FEATURE [App::DocumentObjectGroupPython] P_element003  label="P_element : 0.103"  # scripted group (container) (typed FeaturePython)
  n = 0.103
FEATURE [App::DocumentObjectGroupPython] S_element005  label="S_element : 0.004"  # scripted group (container) (typed FeaturePython)
  n = 0.003
FEATURE [App::DocumentObjectGroupPython] Ca_element004  label="Ca_element : 0.225"  # scripted group (container) (typed FeaturePython)
  n = 0.225
FEATURE [App::DocumentObjectGroupPython] G4_BONE_CORTICAL_ICRP  # scripted group (container) (typed FeaturePython)
  Dunit = g/cm3
  Dvalue = 1.92
  Group = -> [H_element016,C_element016,N_element011,O_element015,Na_element003,Mg_element002,P_element003,S_element005,Ca_element004]
  conduct = 2
  density = 1
  expand = 3
  formula = G4_BONE_CORTICAL_ICRP
  name = G4_BONE_CORTICAL_ICRP
  specific = 4
FEATURE [App::DocumentObjectGroupPython] B_element001  label="B_element : 4"  # scripted group (container) (typed FeaturePython)
  n = 4
  ref = B_element
FEATURE [App::DocumentObjectGroupPython] C_element017  label="C_element : 1"  # scripted group (container) (typed FeaturePython)
  n = 1
  ref = C_element
FEATURE [App::DocumentObjectGroupPython] G4_BORON_CARBIDE  # scripted group (container) (typed FeaturePython)
  Dunit = g/cm3
  Dvalue = 2.52
  Group = -> [B_element001,C_element017]
  conduct = 2
  density = 1
  expand = 3
  formula = G4_BORON_CARBIDE
  name = G4_BORON_CARBIDE
  specific = 4
FEATURE [App::DocumentObjectGroupPython] B_element002  label="B_element : 2"  # scripted group (container) (typed FeaturePython)
  n = 2
  ref = B_element
FEATURE [App::DocumentObjectGroupPython] O_element016  label="O_element : 006"  # scripted group (container) (typed FeaturePython)
  n = 3
  ref = O_element
FEATURE [App::DocumentObjectGroupPython] G4_BORON_OXIDE  # scripted group (container) (typed FeaturePython)
  Dunit = g/cm3
  Dvalue = 1.812
  Group = -> [B_element002,O_element016]
  conduct = 2
  density = 1
  expand = 3
  formula = G4_BORON_OXIDE
  name = G4_BORON_OXIDE
  specific = 4
FEATURE [App::DocumentObjectGroupPython] H_element017  label="H_element : 0.107"  # scripted group (container) (typed FeaturePython)
  n = 0.107
FEATURE [App::DocumentObjectGroupPython] C_element018  label="C_element : 0.145"  # scripted group (container) (typed FeaturePython)
  n = 0.145
FEATURE [App::DocumentObjectGroupPython] N_element012  label="N_element : 0.022"  # scripted group (container) (typed FeaturePython)
  n = 0.022
FEATURE [App::DocumentObjectGroupPython] O_element017  label="O_element : 0.712"  # scripted group (container) (typed FeaturePython)
  n = 0.712
FEATURE [App::DocumentObjectGroupPython] Na_element004  label="Na_element : 0.004"  # scripted group (container) (typed FeaturePython)
  n = 0.002
FEATURE [App::DocumentObjectGroupPython] P_element004  label="P_element : 0.004"  # scripted group (container) (typed FeaturePython)
  n = 0.004
FEATURE [App::DocumentObjectGroupPython] S_element006  label="S_element : 0.005"  # scripted group (container) (typed FeaturePython)
  n = 0.002
FEATURE [App::DocumentObjectGroupPython] Cl_element003  label="Cl_element : 0.004"  # scripted group (container) (typed FeaturePython)
  n = 0.003
FEATURE [App::DocumentObjectGroupPython] K_element002  label="K_element : 0.003"  # scripted group (container) (typed FeaturePython)
  n = 0.003
FEATURE [App::DocumentObjectGroupPython] G4_BRAIN_ICRP  # scripted group (container) (typed FeaturePython)
  Dunit = g/cm3
  Dvalue = 1.04
  Group = -> [H_element017,C_element018,N_element012,O_element017,Na_element004,P_element004,S_element006,Cl_element003,K_element002]
  conduct = 2
  density = 1
  expand = 3
  formula = G4_BRAIN_ICRP
  name = G4_BRAIN_ICRP
  specific = 4
FEATURE [App::DocumentObjectGroupPython] C_element019  label="C_element : 4"  # scripted group (container) (typed FeaturePython)
  n = 4
  ref = C_element
FEATURE [App::DocumentObjectGroupPython] H_element018  label="H_element : 010"  # scripted group (container) (typed FeaturePython)
  n = 10
  ref = H_element
FEATURE [App::DocumentObjectGroupPython] G4_BUTANE  # scripted group (container) (typed FeaturePython)
  Dunit = g/cm3
  Dvalue = 0.00249343
  Group = -> [C_element019,H_element018]
  conduct = 2
  density = 1
  expand = 3
  formula = G4_BUTANE
  name = G4_BUTANE
  specific = 4
FEATURE [App::DocumentObjectGroupPython] C_element020  label="C_element : 008"  # scripted group (container) (typed FeaturePython)
  n = 4
  ref = C_element
FEATURE [App::DocumentObjectGroupPython] H_element019  label="H_element : 011"  # scripted group (container) (typed FeaturePython)
  n = 10
  ref = H_element
FEATURE [App::DocumentObjectGroupPython] O_element018  label="O_element : 007"  # scripted group (container) (typed FeaturePython)
  n = 1
  ref = O_element
FEATURE [App::DocumentObjectGroupPython] G4_N_BUTYL_ALCOHOL  label="G4_N-BUTYL_ALCOHOL"  # scripted group (container) (typed FeaturePython)
  Dunit = g/cm3
  Dvalue = 0.8098
  Group = -> [C_element020,H_element019,O_element018]
  conduct = 2
  density = 1
  expand = 3
  formula = G4_N-BUTYL_ALCOHOL
  name = G4_N-BUTYL_ALCOHOL
  specific = 4
FEATURE [App::DocumentObjectGroupPython] H_element020  label="H_element : 0.025"  # scripted group (container) (typed FeaturePython)
  n = 0.02468
FEATURE [App::DocumentObjectGroupPython] C_element021  label="C_element : 0.502"  # scripted group (container) (typed FeaturePython)
  n = 0.501611
FEATURE [App::DocumentObjectGroupPython] O_element019  label="O_element : 0.005"  # scripted group (container) (typed FeaturePython)
  n = 0.004527
FEATURE [App::DocumentObjectGroupPython] F_element004  label="F_element : 0.465"  # scripted group (container) (typed FeaturePython)
  n = 0.465209
FEATURE [App::DocumentObjectGroupPython] Si_element001  label="Si_element : 0.004"  # scripted group (container) (typed FeaturePython)
  n = 0.003973
FEATURE [App::DocumentObjectGroupPython] G4_C_552  label="G4_C-552"  # scripted group (container) (typed FeaturePython)
  Dunit = g/cm3
  Dvalue = 1.76
  Group = -> [H_element020,C_element021,O_element019,F_element004,Si_element001]
  conduct = 2
  density = 1
  expand = 3
  formula = G4_C-552
  name = G4_C-552
  specific = 4
FEATURE [App::DocumentObjectGroupPython] Cd_element001  label="Cd_element : 1"  # scripted group (container) (typed FeaturePython)
  n = 1
  ref = Cd_element
FEATURE [App::DocumentObjectGroupPython] Te_element001  label="Te_element : 1"  # scripted group (container) (typed FeaturePython)
  n = 1
  ref = Te_element
FEATURE [App::DocumentObjectGroupPython] G4_CADMIUM_TELLURIDE  # scripted group (container) (typed FeaturePython)
  Dunit = g/cm3
  Dvalue = 6.2
  Group = -> [Cd_element001,Te_element001]
  conduct = 2
  density = 1
  expand = 3
  formula = G4_CADMIUM_TELLURIDE
  name = G4_CADMIUM_TELLURIDE
  specific = 4
FEATURE [App::DocumentObjectGroupPython] Cd_element002  label="Cd_element : 002"  # scripted group (container) (typed FeaturePython)
  n = 1
  ref = Cd_element
FEATURE [App::DocumentObjectGroupPython] W_element001  label="W_element : 1"  # scripted group (container) (typed FeaturePython)
  n = 1
  ref = W_element
FEATURE [App::DocumentObjectGroupPython] O_element020  label="O_element : 008"  # scripted group (container) (typed FeaturePython)
  n = 4
  ref = O_element
FEATURE [App::DocumentObjectGroupPython] G4_CADMIUM_TUNGSTATE  # scripted group (container) (typed FeaturePython)
  Dunit = g/cm3
  Dvalue = 7.9
  Group = -> [Cd_element002,W_element001,O_element020]
  conduct = 2
  density = 1
  expand = 3
  formula = G4_CADMIUM_TUNGSTATE
  name = G4_CADMIUM_TUNGSTATE
  specific = 4
FEATURE [App::DocumentObjectGroupPython] Ca_element005  label="Ca_element : 1"  # scripted group (container) (typed FeaturePython)
  n = 1
  ref = Ca_element
FEATURE [App::DocumentObjectGroupPython] C_element022  label="C_element : 009"  # scripted group (container) (typed FeaturePython)
  n = 1
  ref = C_element
FEATURE [App::DocumentObjectGroupPython] O_element021  label="O_element : 009"  # scripted group (container) (typed FeaturePython)
  n = 3
  ref = O_element
FEATURE [App::DocumentObjectGroupPython] G4_CALCIUM_CARBONATE  # scripted group (container) (typed FeaturePython)
  Dunit = g/cm3
  Dvalue = 2.8
  Group = -> [Ca_element005,C_element022,O_element021]
  conduct = 2
  density = 1
  expand = 3
  formula = G4_CALCIUM_CARBONATE
  name = G4_CALCIUM_CARBONATE
  specific = 4
FEATURE [App::DocumentObjectGroupPython] Ca_element006  label="Ca_element : 002"  # scripted group (container) (typed FeaturePython)
  n = 1
  ref = Ca_element
FEATURE [App::DocumentObjectGroupPython] F_element005  label="F_element : 003"  # scripted group (container) (typed FeaturePython)
  n = 2
  ref = F_element
FEATURE [App::DocumentObjectGroupPython] G4_CALCIUM_FLUORIDE  # scripted group (container) (typed FeaturePython)
  Dunit = g/cm3
  Dvalue = 3.18
  Group = -> [Ca_element006,F_element005]
  conduct = 2
  density = 1
  expand = 3
  formula = G4_CALCIUM_FLUORIDE
  name = G4_CALCIUM_FLUORIDE
  specific = 4
FEATURE [App::DocumentObjectGroupPython] Ca_element007  label="Ca_element : 003"  # scripted group (container) (typed FeaturePython)
  n = 1
  ref = Ca_element
FEATURE [App::DocumentObjectGroupPython] O_element022  label="O_element : 010"  # scripted group (container) (typed FeaturePython)
  n = 1
  ref = O_element
FEATURE [App::DocumentObjectGroupPython] G4_CALCIUM_OXIDE  # scripted group (container) (typed FeaturePython)
  Dunit = g/cm3
  Dvalue = 3.3
  Group = -> [Ca_element007,O_element022]
  conduct = 2
  density = 1
  expand = 3
  formula = G4_CALCIUM_OXIDE
  name = G4_CALCIUM_OXIDE
  specific = 4
FEATURE [App::DocumentObjectGroupPython] Ca_element008  label="Ca_element : 004"  # scripted group (container) (typed FeaturePython)
  n = 1
  ref = Ca_element
FEATURE [App::DocumentObjectGroupPython] S_element007  label="S_element : 002"  # scripted group (container) (typed FeaturePython)
  n = 1
  ref = S_element
FEATURE [App::DocumentObjectGroupPython] O_element023  label="O_element : 011"  # scripted group (container) (typed FeaturePython)
  n = 4
  ref = O_element
FEATURE [App::DocumentObjectGroupPython] G4_CALCIUM_SULFATE  # scripted group (container) (typed FeaturePython)
  Dunit = g/cm3
  Dvalue = 2.96
  Group = -> [Ca_element008,S_element007,O_element023]
  conduct = 2
  density = 1
  expand = 3
  formula = G4_CALCIUM_SULFATE
  name = G4_CALCIUM_SULFATE
  specific = 4
FEATURE [App::DocumentObjectGroupPython] Ca_element009  label="Ca_element : 005"  # scripted group (container) (typed FeaturePython)
  n = 1
  ref = Ca_element
FEATURE [App::DocumentObjectGroupPython] W_element002  label="W_element : 002"  # scripted group (container) (typed FeaturePython)
  n = 1
  ref = W_element
FEATURE [App::DocumentObjectGroupPython] O_element024  label="O_element : 012"  # scripted group (container) (typed FeaturePython)
  n = 4
  ref = O_element
FEATURE [App::DocumentObjectGroupPython] G4_CALCIUM_TUNGSTATE  # scripted group (container) (typed FeaturePython)
  Dunit = g/cm3
  Dvalue = 6.062
  Group = -> [Ca_element009,W_element002,O_element024]
  conduct = 2
  density = 1
  expand = 3
  formula = G4_CALCIUM_TUNGSTATE
  name = G4_CALCIUM_TUNGSTATE
  specific = 4
FEATURE [App::DocumentObjectGroupPython] C_element023  label="C_element : 010"  # scripted group (container) (typed FeaturePython)
  n = 1
  ref = C_element
FEATURE [App::DocumentObjectGroupPython] O_element025  label="O_element : 013"  # scripted group (container) (typed FeaturePython)
  n = 2
  ref = O_element
FEATURE [App::DocumentObjectGroupPython] G4_CARBON_DIOXIDE  # scripted group (container) (typed FeaturePython)
  Dunit = g/cm3
  Dvalue = 0.00184212
  Group = -> [C_element023,O_element025]
  conduct = 2
  density = 1
  expand = 3
  formula = G4_CARBON_DIOXIDE
  name = G4_CARBON_DIOXIDE
  specific = 4
FEATURE [App::DocumentObjectGroupPython] C_element024  label="C_element : 011"  # scripted group (container) (typed FeaturePython)
  n = 1
  ref = C_element
FEATURE [App::DocumentObjectGroupPython] Cl_element004  label="Cl_element : 4"  # scripted group (container) (typed FeaturePython)
  n = 4
  ref = Cl_element
FEATURE [App::DocumentObjectGroupPython] G4_CARBON_TETRACHLORIDE  # scripted group (container) (typed FeaturePython)
  Dunit = g/cm3
  Dvalue = 1.594
  Group = -> [C_element024,Cl_element004]
  conduct = 2
  density = 1
  expand = 3
  formula = G4_CARBON_TETRACHLORIDE
  name = G4_CARBON_TETRACHLORIDE
  specific = 4
FEATURE [App::DocumentObjectGroupPython] C_element025  label="C_element : 012"  # scripted group (container) (typed FeaturePython)
  n = 6
  ref = C_element
FEATURE [App::DocumentObjectGroupPython] H_element021  label="H_element : 012"  # scripted group (container) (typed FeaturePython)
  n = 10
  ref = H_element
FEATURE [App::DocumentObjectGroupPython] O_element026  label="O_element : 5"  # scripted group (container) (typed FeaturePython)
  n = 5
  ref = O_element
FEATURE [App::DocumentObjectGroupPython] G4_CELLULOSE_CELLOPHANE  # scripted group (container) (typed FeaturePython)
  Dunit = g/cm3
  Dvalue = 1.42
  Group = -> [C_element025,H_element021,O_element026]
  conduct = 2
  density = 1
  expand = 3
  formula = G4_CELLULOSE_CELLOPHANE
  name = G4_CELLULOSE_CELLOPHANE
  specific = 4
FEATURE [App::DocumentObjectGroupPython] H_element022  label="H_element : 0.067"  # scripted group (container) (typed FeaturePython)
  n = 0.067125
FEATURE [App::DocumentObjectGroupPython] C_element026  label="C_element : 0.545"  # scripted group (container) (typed FeaturePython)
  n = 0.545403
FEATURE [App::DocumentObjectGroupPython] O_element027  label="O_element : 0.387"  # scripted group (container) (typed FeaturePython)
  n = 0.387472
FEATURE [App::DocumentObjectGroupPython] G4_CELLULOSE_BUTYRATE  # scripted group (container) (typed FeaturePython)
  Dunit = g/cm3
  Dvalue = 1.2
  Group = -> [H_element022,C_element026,O_element027]
  conduct = 2
  density = 1
  expand = 3
  formula = G4_CELLULOSE_BUTYRATE
  name = G4_CELLULOSE_BUTYRATE
  specific = 4
FEATURE [App::DocumentObjectGroupPython] H_element023  label="H_element : 0.029"  # scripted group (container) (typed FeaturePython)
  n = 0.029216
FEATURE [App::DocumentObjectGroupPython] C_element027  label="C_element : 0.271"  # scripted group (container) (typed FeaturePython)
  n = 0.271296
FEATURE [App::DocumentObjectGroupPython] N_element013  label="N_element : 0.121"  # scripted group (container) (typed FeaturePython)
  n = 0.121276
FEATURE [App::DocumentObjectGroupPython] O_element028  label="O_element : 0.578"  # scripted group (container) (typed FeaturePython)
  n = 0.578212
FEATURE [App::DocumentObjectGroupPython] G4_CELLULOSE_NITRATE  # scripted group (container) (typed FeaturePython)
  Dunit = g/cm3
  Dvalue = 1.49
  Group = -> [H_element023,C_element027,N_element013,O_element028]
  conduct = 2
  density = 1
  expand = 3
  formula = G4_CELLULOSE_NITRATE
  name = G4_CELLULOSE_NITRATE
  specific = 4
FEATURE [App::DocumentObjectGroupPython] H_element024  label="H_element : 0.108"  # scripted group (container) (typed FeaturePython)
  n = 0.107596
FEATURE [App::DocumentObjectGroupPython] N_element014  label="N_element : 0.001"  # scripted group (container) (typed FeaturePython)
  n = 0.0008
FEATURE [App::DocumentObjectGroupPython] O_element029  label="O_element : 0.875"  # scripted group (container) (typed FeaturePython)
  n = 0.874976
FEATURE [App::DocumentObjectGroupPython] S_element008  label="S_element : 0.015"  # scripted group (container) (typed FeaturePython)
  n = 0.014627
FEATURE [App::DocumentObjectGroupPython] Ce_element001  label="Ce_element : 0.002"  # scripted group (container) (typed FeaturePython)
  n = 0.002001
FEATURE [App::DocumentObjectGroupPython] G4_CERIC_SULFATE  # scripted group (container) (typed FeaturePython)
  Dunit = g/cm3
  Dvalue = 1.03
  Group = -> [H_element024,N_element014,O_element029,S_element008,Ce_element001]
  conduct = 2
  density = 1
  expand = 3
  formula = G4_CERIC_SULFATE
  name = G4_CERIC_SULFATE
  specific = 4
FEATURE [App::DocumentObjectGroupPython] Cs_element001  label="Cs_element : 1"  # scripted group (container) (typed FeaturePython)
  n = 1
  ref = Cs_element
FEATURE [App::DocumentObjectGroupPython] F_element006  label="F_element : 1"  # scripted group (container) (typed FeaturePython)
  n = 1
  ref = F_element
FEATURE [App::DocumentObjectGroupPython] G4_CESIUM_FLUORIDE  # scripted group (container) (typed FeaturePython)
  Dunit = g/cm3
  Dvalue = 4.115
  Group = -> [Cs_element001,F_element006]
  conduct = 2
  density = 1
  expand = 3
  formula = G4_CESIUM_FLUORIDE
  name = G4_CESIUM_FLUORIDE
  specific = 4
FEATURE [App::DocumentObjectGroupPython] Cs_element002  label="Cs_element : 002"  # scripted group (container) (typed FeaturePython)
  n = 1
  ref = Cs_element
FEATURE [App::DocumentObjectGroupPython] I_element001  label="I_element : 1"  # scripted group (container) (typed FeaturePython)
  n = 1
  ref = I_element
FEATURE [App::DocumentObjectGroupPython] G4_CESIUM_IODIDE  # scripted group (container) (typed FeaturePython)
  Dunit = g/cm3
  Dvalue = 4.51
  Group = -> [Cs_element002,I_element001]
  conduct = 2
  density = 1
  expand = 3
  formula = G4_CESIUM_IODIDE
  name = G4_CESIUM_IODIDE
  specific = 4
FEATURE [App::DocumentObjectGroupPython] C_element028  label="C_element : 013"  # scripted group (container) (typed FeaturePython)
  n = 6
  ref = C_element
FEATURE [App::DocumentObjectGroupPython] H_element025  label="H_element : 013"  # scripted group (container) (typed FeaturePython)
  n = 5
  ref = H_element
FEATURE [App::DocumentObjectGroupPython] Cl_element005  label="Cl_element : 1"  # scripted group (container) (typed FeaturePython)
  n = 1
  ref = Cl_element
FEATURE [App::DocumentObjectGroupPython] G4_CHLOROBENZENE  # scripted group (container) (typed FeaturePython)
  Dunit = g/cm3
  Dvalue = 1.1058
  Group = -> [C_element028,H_element025,Cl_element005]
  conduct = 2
  density = 1
  expand = 3
  formula = G4_CHLOROBENZENE
  name = G4_CHLOROBENZENE
  specific = 4
FEATURE [App::DocumentObjectGroupPython] C_element029  label="C_element : 014"  # scripted group (container) (typed FeaturePython)
  n = 1
  ref = C_element
FEATURE [App::DocumentObjectGroupPython] H_element026  label="H_element : 1"  # scripted group (container) (typed FeaturePython)
  n = 1
  ref = H_element
FEATURE [App::DocumentObjectGroupPython] Cl_element006  label="Cl_element : 3"  # scripted group (container) (typed FeaturePython)
  n = 3
  ref = Cl_element
FEATURE [App::DocumentObjectGroupPython] G4_CHLOROFORM  # scripted group (container) (typed FeaturePython)
  Dunit = g/cm3
  Dvalue = 1.4832
  Group = -> [C_element029,H_element026,Cl_element006]
  conduct = 2
  density = 1
  expand = 3
  formula = G4_CHLOROFORM
  name = G4_CHLOROFORM
  specific = 4
FEATURE [App::DocumentObjectGroupPython] H_element027  label="H_element : 0.010"  # scripted group (container) (typed FeaturePython)
  n = 0.01
FEATURE [App::DocumentObjectGroupPython] C_element030  label="C_element : 0.001"  # scripted group (container) (typed FeaturePython)
  n = 0.001
FEATURE [App::DocumentObjectGroupPython] O_element030  label="O_element : 0.529"  # scripted group (container) (typed FeaturePython)
  n = 0.529107
FEATURE [App::DocumentObjectGroupPython] Na_element005  label="Na_element : 0.016"  # scripted group (container) (typed FeaturePython)
  n = 0.016
FEATURE [App::DocumentObjectGroupPython] Mg_element003  label="Mg_element : 0.004"  # scripted group (container) (typed FeaturePython)
  n = 0.002
FEATURE [App::DocumentObjectGroupPython] Al_element002  label="Al_element : 0.034"  # scripted group (container) (typed FeaturePython)
  n = 0.033872
FEATURE [App::DocumentObjectGroupPython] Si_element002  label="Si_element : 0.337"  # scripted group (container) (typed FeaturePython)
  n = 0.337021
FEATURE [App::DocumentObjectGroupPython] K_element003  label="K_element : 0.013"  # scripted group (container) (typed FeaturePython)
  n = 0.013
FEATURE [App::DocumentObjectGroupPython] Ca_element010  label="Ca_element : 0.044"  # scripted group (container) (typed FeaturePython)
  n = 0.044
FEATURE [App::DocumentObjectGroupPython] Fe_element002  label="Fe_element : 0.014"  # scripted group (container) (typed FeaturePython)
  n = 0.014
FEATURE [App::DocumentObjectGroupPython] G4_CONCRETE  # scripted group (container) (typed FeaturePython)
  Dunit = g/cm3
  Dvalue = 2.3
  Group = -> [H_element027,C_element030,O_element030,Na_element005,Mg_element003,Al_element002,Si_element002,K_element003,Ca_element010,Fe_element002]
  conduct = 2
  density = 1
  expand = 3
  formula = G4_CONCRETE
  name = G4_CONCRETE
  specific = 4
FEATURE [App::DocumentObjectGroupPython] C_element031  label="C_element : 015"  # scripted group (container) (typed FeaturePython)
  n = 6
  ref = C_element
FEATURE [App::DocumentObjectGroupPython] H_element028  label="H_element : 12"  # scripted group (container) (typed FeaturePython)
  n = 12
  ref = H_element
FEATURE [App::DocumentObjectGroupPython] G4_CYCLOHEXANE  # scripted group (container) (typed FeaturePython)
  Dunit = g/cm3
  Dvalue = 0.779
  Group = -> [C_element031,H_element028]
  conduct = 2
  density = 1
  expand = 3
  formula = G4_CYCLOHEXANE
  name = G4_CYCLOHEXANE
  specific = 4
FEATURE [App::DocumentObjectGroupPython] C_element032  label="C_element : 016"  # scripted group (container) (typed FeaturePython)
  n = 6
  ref = C_element
FEATURE [App::DocumentObjectGroupPython] H_element029  label="H_element : 4"  # scripted group (container) (typed FeaturePython)
  n = 4
  ref = H_element
FEATURE [App::DocumentObjectGroupPython] Cl_element007  label="Cl_element : 2"  # scripted group (container) (typed FeaturePython)
  n = 2
  ref = Cl_element
FEATURE [App::DocumentObjectGroupPython] G4_1_2_DICHLOROBENZENE  label="G4_1.2-DICHLOROBENZENE"  # scripted group (container) (typed FeaturePython)
  Dunit = g/cm3
  Dvalue = 1.3048
  Group = -> [C_element032,H_element029,Cl_element007]
  conduct = 2
  density = 1
  expand = 3
  formula = G4_1.2-DICHLOROBENZENE
  name = G4_1.2-DICHLOROBENZENE
  specific = 4
FEATURE [App::DocumentObjectGroupPython] C_element033  label="C_element : 017"  # scripted group (container) (typed FeaturePython)
  n = 4
  ref = C_element
FEATURE [App::DocumentObjectGroupPython] H_element030  label="H_element : 8"  # scripted group (container) (typed FeaturePython)
  n = 8
  ref = H_element
FEATURE [App::DocumentObjectGroupPython] O_element031  label="O_element : 014"  # scripted group (container) (typed FeaturePython)
  n = 1
  ref = O_element
FEATURE [App::DocumentObjectGroupPython] Cl_element008  label="Cl_element : 005"  # scripted group (container) (typed FeaturePython)
  n = 2
  ref = Cl_element
FEATURE [App::DocumentObjectGroupPython] G4_DICHLORODIETHYL_ETHER  # scripted group (container) (typed FeaturePython)
  Dunit = g/cm3
  Dvalue = 1.2199
  Group = -> [C_element033,H_element030,O_element031,Cl_element008]
  conduct = 2
  density = 1
  expand = 3
  formula = G4_DICHLORODIETHYL_ETHER
  name = G4_DICHLORODIETHYL_ETHER
  specific = 4
FEATURE [App::DocumentObjectGroupPython] C_element034  label="C_element : 018"  # scripted group (container) (typed FeaturePython)
  n = 2
  ref = C_element
FEATURE [App::DocumentObjectGroupPython] H_element031  label="H_element : 014"  # scripted group (container) (typed FeaturePython)
  n = 4
  ref = H_element
FEATURE [App::DocumentObjectGroupPython] Cl_element009  label="Cl_element : 006"  # scripted group (container) (typed FeaturePython)
  n = 2
  ref = Cl_element
FEATURE [App::DocumentObjectGroupPython] G4_1_2_DICHLOROETHANE  label="G4_1.2-DICHLOROETHANE"  # scripted group (container) (typed FeaturePython)
  Dunit = g/cm3
  Dvalue = 1.2351
  Group = -> [C_element034,H_element031,Cl_element009]
  conduct = 2
  density = 1
  expand = 3
  formula = G4_1.2-DICHLOROETHANE
  name = G4_1.2-DICHLOROETHANE
  specific = 4
FEATURE [App::DocumentObjectGroupPython] C_element035  label="C_element : 019"  # scripted group (container) (typed FeaturePython)
  n = 4
  ref = C_element
FEATURE [App::DocumentObjectGroupPython] H_element032  label="H_element : 015"  # scripted group (container) (typed FeaturePython)
  n = 10
  ref = H_element
FEATURE [App::DocumentObjectGroupPython] O_element032  label="O_element : 015"  # scripted group (container) (typed FeaturePython)
  n = 1
  ref = O_element
FEATURE [App::DocumentObjectGroupPython] G4_DIETHYL_ETHER  # scripted group (container) (typed FeaturePython)
  Dunit = g/cm3
  Dvalue = 0.71378
  Group = -> [C_element035,H_element032,O_element032]
  conduct = 2
  density = 1
  expand = 3
  formula = G4_DIETHYL_ETHER
  name = G4_DIETHYL_ETHER
  specific = 4
FEATURE [App::DocumentObjectGroupPython] C_element036  label="C_element : 020"  # scripted group (container) (typed FeaturePython)
  n = 3
  ref = C_element
FEATURE [App::DocumentObjectGroupPython] H_element033  label="H_element : 016"  # scripted group (container) (typed FeaturePython)
  n = 7
  ref = H_element
FEATURE [App::DocumentObjectGroupPython] N_element015  label="N_element : 008"  # scripted group (container) (typed FeaturePython)
  n = 1
  ref = N_element
FEATURE [App::DocumentObjectGroupPython] O_element033  label="O_element : 016"  # scripted group (container) (typed FeaturePython)
  n = 1
  ref = O_element
FEATURE [App::DocumentObjectGroupPython] G4_N_N_DIMETHYL_FORMAMIDE  label="G4_N.N-DIMETHYL_FORMAMIDE"  # scripted group (container) (typed FeaturePython)
  Dunit = g/cm3
  Dvalue = 0.9487
  Group = -> [C_element036,H_element033,N_element015,O_element033]
  conduct = 2
  density = 1
  expand = 3
  formula = G4_N.N-DIMETHYL_FORMAMIDE
  name = G4_N.N-DIMETHYL_FORMAMIDE
  specific = 4
FEATURE [App::DocumentObjectGroupPython] C_element037  label="C_element : 021"  # scripted group (container) (typed FeaturePython)
  n = 2
  ref = C_element
FEATURE [App::DocumentObjectGroupPython] H_element034  label="H_element : 017"  # scripted group (container) (typed FeaturePython)
  n = 6
  ref = H_element
FEATURE [App::DocumentObjectGroupPython] O_element034  label="O_element : 017"  # scripted group (container) (typed FeaturePython)
  n = 1
  ref = O_element
FEATURE [App::DocumentObjectGroupPython] S_element009  label="S_element : 003"  # scripted group (container) (typed FeaturePython)
  n = 1
  ref = S_element
FEATURE [App::DocumentObjectGroupPython] G4_DIMETHYL_SULFOXIDE  # scripted group (container) (typed FeaturePython)
  Dunit = g/cm3
  Dvalue = 1.1014
  Group = -> [C_element037,H_element034,O_element034,S_element009]
  conduct = 2
  density = 1
  expand = 3
  formula = G4_DIMETHYL_SULFOXIDE
  name = G4_DIMETHYL_SULFOXIDE
  specific = 4
FEATURE [App::DocumentObjectGroupPython] C_element038  label="C_element : 022"  # scripted group (container) (typed FeaturePython)
  n = 2
  ref = C_element
FEATURE [App::DocumentObjectGroupPython] H_element035  label="H_element : 018"  # scripted group (container) (typed FeaturePython)
  n = 6
  ref = H_element
FEATURE [App::DocumentObjectGroupPython] G4_ETHANE  # scripted group (container) (typed FeaturePython)
  Dunit = g/cm3
  Dvalue = 0.00125324
  Group = -> [C_element038,H_element035]
  conduct = 2
  density = 1
  expand = 3
  formula = G4_ETHANE
  name = G4_ETHANE
  specific = 4
FEATURE [App::DocumentObjectGroupPython] C_element039  label="C_element : 023"  # scripted group (container) (typed FeaturePython)
  n = 2
  ref = C_element
FEATURE [App::DocumentObjectGroupPython] H_element036  label="H_element : 019"  # scripted group (container) (typed FeaturePython)
  n = 6
  ref = H_element
FEATURE [App::DocumentObjectGroupPython] O_element035  label="O_element : 018"  # scripted group (container) (typed FeaturePython)
  n = 1
  ref = O_element
FEATURE [App::DocumentObjectGroupPython] G4_ETHYL_ALCOHOL  # scripted group (container) (typed FeaturePython)
  Dunit = g/cm3
  Dvalue = 0.7893
  Group = -> [C_element039,H_element036,O_element035]
  conduct = 2
  density = 1
  expand = 3
  formula = G4_ETHYL_ALCOHOL
  name = G4_ETHYL_ALCOHOL
  specific = 4
FEATURE [App::DocumentObjectGroupPython] H_element037  label="H_element : 0.090"  # scripted group (container) (typed FeaturePython)
  n = 0.090027
FEATURE [App::DocumentObjectGroupPython] C_element040  label="C_element : 0.585"  # scripted group (container) (typed FeaturePython)
  n = 0.585182
FEATURE [App::DocumentObjectGroupPython] O_element036  label="O_element : 0.325"  # scripted group (container) (typed FeaturePython)
  n = 0.324791
FEATURE [App::DocumentObjectGroupPython] G4_ETHYL_CELLULOSE  # scripted group (container) (typed FeaturePython)
  Dunit = g/cm3
  Dvalue = 1.13
  Group = -> [H_element037,C_element040,O_element036]
  conduct = 2
  density = 1
  expand = 3
  formula = G4_ETHYL_CELLULOSE
  name = G4_ETHYL_CELLULOSE
  specific = 4
FEATURE [App::DocumentObjectGroupPython] C_element041  label="C_element : 024"  # scripted group (container) (typed FeaturePython)
  n = 2
  ref = C_element
FEATURE [App::DocumentObjectGroupPython] H_element038  label="H_element : 020"  # scripted group (container) (typed FeaturePython)
  n = 4
  ref = H_element
FEATURE [App::DocumentObjectGroupPython] G4_ETHYLENE  # scripted group (container) (typed FeaturePython)
  Dunit = g/cm3
  Dvalue = 0.00117497
  Group = -> [C_element041,H_element038]
  conduct = 2
  density = 1
  expand = 3
  formula = G4_ETHYLENE
  name = G4_ETHYLENE
  specific = 4
FEATURE [App::DocumentObjectGroupPython] H_element039  label="H_element : 0.096"  # scripted group (container) (typed FeaturePython)
  n = 0.096
FEATURE [App::DocumentObjectGroupPython] C_element042  label="C_element : 0.195"  # scripted group (container) (typed FeaturePython)
  n = 0.195
FEATURE [App::DocumentObjectGroupPython] N_element016  label="N_element : 0.057"  # scripted group (container) (typed FeaturePython)
  n = 0.057
FEATURE [App::DocumentObjectGroupPython] O_element037  label="O_element : 0.646"  # scripted group (container) (typed FeaturePython)
  n = 0.646
FEATURE [App::DocumentObjectGroupPython] Na_element006  label="Na_element : 0.017"  # scripted group (container) (typed FeaturePython)
  n = 0.001
FEATURE [App::DocumentObjectGroupPython] P_element005  label="P_element : 0.104"  # scripted group (container) (typed FeaturePython)
  n = 0.001
FEATURE [App::DocumentObjectGroupPython] S_element010  label="S_element : 0.016"  # scripted group (container) (typed FeaturePython)
  n = 0.003
FEATURE [App::DocumentObjectGroupPython] Cl_element010  label="Cl_element : 0.005"  # scripted group (container) (typed FeaturePython)
  n = 0.001
FEATURE [App::DocumentObjectGroupPython] G4_EYE_LENS_ICRP  # scripted group (container) (typed FeaturePython)
  Dunit = g/cm3
  Dvalue = 1.07
  Group = -> [H_element039,C_element042,N_element016,O_element037,Na_element006,P_element005,S_element010,Cl_element010]
  conduct = 2
  density = 1
  expand = 3
  formula = G4_EYE_LENS_ICRP
  name = G4_EYE_LENS_ICRP
  specific = 4
FEATURE [App::DocumentObjectGroupPython] Fe_element003  label="Fe_element : 2"  # scripted group (container) (typed FeaturePython)
  n = 2
  ref = Fe_element
FEATURE [App::DocumentObjectGroupPython] O_element038  label="O_element : 019"  # scripted group (container) (typed FeaturePython)
  n = 3
  ref = O_element
FEATURE [App::DocumentObjectGroupPython] G4_FERRIC_OXIDE  # scripted group (container) (typed FeaturePython)
  Dunit = g/cm3
  Dvalue = 5.2
  Group = -> [Fe_element003,O_element038]
  conduct = 2
  density = 1
  expand = 3
  formula = G4_FERRIC_OXIDE
  name = G4_FERRIC_OXIDE
  specific = 4
FEATURE [App::DocumentObjectGroupPython] Fe_element004  label="Fe_element : 1"  # scripted group (container) (typed FeaturePython)
  n = 1
  ref = Fe_element
FEATURE [App::DocumentObjectGroupPython] B_element003  label="B_element : 1"  # scripted group (container) (typed FeaturePython)
  n = 1
  ref = B_element
FEATURE [App::DocumentObjectGroupPython] G4_FERROBORIDE  # scripted group (container) (typed FeaturePython)
  Dunit = g/cm3
  Dvalue = 7.15
  Group = -> [Fe_element004,B_element003]
  conduct = 2
  density = 1
  expand = 3
  formula = G4_FERROBORIDE
  name = G4_FERROBORIDE
  specific = 4
FEATURE [App::DocumentObjectGroupPython] Fe_element005  label="Fe_element : 003"  # scripted group (container) (typed FeaturePython)
  n = 1
  ref = Fe_element
FEATURE [App::DocumentObjectGroupPython] O_element039  label="O_element : 020"  # scripted group (container) (typed FeaturePython)
  n = 1
  ref = O_element
FEATURE [App::DocumentObjectGroupPython] G4_FERROUS_OXIDE  # scripted group (container) (typed FeaturePython)
  Dunit = g/cm3
  Dvalue = 5.7
  Group = -> [Fe_element005,O_element039]
  conduct = 2
  density = 1
  expand = 3
  formula = G4_FERROUS_OXIDE
  name = G4_FERROUS_OXIDE
  specific = 4
FEATURE [App::DocumentObjectGroupPython] H_element040  label="H_element : 0.115"  # scripted group (container) (typed FeaturePython)
  n = 0.108259
FEATURE [App::DocumentObjectGroupPython] N_element017  label="N_element : 0.000"  # scripted group (container) (typed FeaturePython)
  n = 2.7e-05
FEATURE [App::DocumentObjectGroupPython] O_element040  label="O_element : 0.879"  # scripted group (container) (typed FeaturePython)
  n = 0.878636
FEATURE [App::DocumentObjectGroupPython] Na_element007  label="Na_element : 0.000"  # scripted group (container) (typed FeaturePython)
  n = 2.2e-05
FEATURE [App::DocumentObjectGroupPython] S_element011  label="S_element : 0.013"  # scripted group (container) (typed FeaturePython)
  n = 0.012968
FEATURE [App::DocumentObjectGroupPython] Cl_element011  label="Cl_element : 0.000"  # scripted group (container) (typed FeaturePython)
  n = 3.4e-05
FEATURE [App::DocumentObjectGroupPython] Fe_element006  label="Fe_element : 0.000"  # scripted group (container) (typed FeaturePython)
  n = 5.4e-05
FEATURE [App::DocumentObjectGroupPython] G4_FERROUS_SULFATE  # scripted group (container) (typed FeaturePython)
  Dunit = g/cm3
  Dvalue = 1.024
  Group = -> [H_element040,N_element017,O_element040,Na_element007,S_element011,Cl_element011,Fe_element006]
  conduct = 2
  density = 1
  expand = 3
  formula = G4_FERROUS_SULFATE
  name = G4_FERROUS_SULFATE
  specific = 4
FEATURE [App::DocumentObjectGroupPython] C_element043  label="C_element : 0.099"  # scripted group (container) (typed FeaturePython)
  n = 0.099335
FEATURE [App::DocumentObjectGroupPython] F_element007  label="F_element : 0.314"  # scripted group (container) (typed FeaturePython)
  n = 0.314247
FEATURE [App::DocumentObjectGroupPython] Cl_element012  label="Cl_element : 0.586"  # scripted group (container) (typed FeaturePython)
  n = 0.586418
FEATURE [App::DocumentObjectGroupPython] G4_FREON_12  label="G4_FREON-12"  # scripted group (container) (typed FeaturePython)
  Dunit = g/cm3
  Dvalue = 1.12
  Group = -> [C_element043,F_element007,Cl_element012]
  conduct = 2
  density = 1
  expand = 3
  formula = G4_FREON-12
  name = G4_FREON-12
  specific = 4
FEATURE [App::DocumentObjectGroupPython] C_element044  label="C_element : 0.057"  # scripted group (container) (typed FeaturePython)
  n = 0.057245
FEATURE [App::DocumentObjectGroupPython] F_element008  label="F_element : 0.181"  # scripted group (container) (typed FeaturePython)
  n = 0.181096
FEATURE [App::DocumentObjectGroupPython] Br_element001  label="Br_element : 0.762"  # scripted group (container) (typed FeaturePython)
  n = 0.761659
FEATURE [App::DocumentObjectGroupPython] G4_FREON_12B2  label="G4_FREON-12B2"  # scripted group (container) (typed FeaturePython)
  Dunit = g/cm3
  Dvalue = 1.8
  Group = -> [C_element044,F_element008,Br_element001]
  conduct = 2
  density = 1
  expand = 3
  formula = G4_FREON-12B2
  name = G4_FREON-12B2
  specific = 4
FEATURE [App::DocumentObjectGroupPython] C_element045  label="C_element : 0.115"  # scripted group (container) (typed FeaturePython)
  n = 0.114983
FEATURE [App::DocumentObjectGroupPython] F_element009  label="F_element : 0.546"  # scripted group (container) (typed FeaturePython)
  n = 0.545621
FEATURE [App::DocumentObjectGroupPython] Cl_element013  label="Cl_element : 0.339"  # scripted group (container) (typed FeaturePython)
  n = 0.339396
FEATURE [App::DocumentObjectGroupPython] G4_FREON_13  label="G4_FREON-13"  # scripted group (container) (typed FeaturePython)
  Dunit = g/cm3
  Dvalue = 0.95
  Group = -> [C_element045,F_element009,Cl_element013]
  conduct = 2
  density = 1
  expand = 3
  formula = G4_FREON-13
  name = G4_FREON-13
  specific = 4
FEATURE [App::DocumentObjectGroupPython] C_element046  label="C_element : 025"  # scripted group (container) (typed FeaturePython)
  n = 1
  ref = C_element
FEATURE [App::DocumentObjectGroupPython] F_element010  label="F_element : 3"  # scripted group (container) (typed FeaturePython)
  n = 3
  ref = F_element
FEATURE [App::DocumentObjectGroupPython] Br_element002  label="Br_element : 1"  # scripted group (container) (typed FeaturePython)
  n = 1
  ref = Br_element
FEATURE [App::DocumentObjectGroupPython] G4_FREON_13B1  label="G4_FREON-13B1"  # scripted group (container) (typed FeaturePython)
  Dunit = g/cm3
  Dvalue = 1.5
  Group = -> [C_element046,F_element010,Br_element002]
  conduct = 2
  density = 1
  expand = 3
  formula = G4_FREON-13B1
  name = G4_FREON-13B1
  specific = 4
FEATURE [App::DocumentObjectGroupPython] C_element047  label="C_element : 0.061"  # scripted group (container) (typed FeaturePython)
  n = 0.061309
FEATURE [App::DocumentObjectGroupPython] F_element011  label="F_element : 0.291"  # scripted group (container) (typed FeaturePython)
  n = 0.290924
FEATURE [App::DocumentObjectGroupPython] I_element002  label="I_element : 0.648"  # scripted group (container) (typed FeaturePython)
  n = 0.647767
FEATURE [App::DocumentObjectGroupPython] G4_FREON_13I1  label="G4_FREON-13I1"  # scripted group (container) (typed FeaturePython)
  Dunit = g/cm3
  Dvalue = 1.8
  Group = -> [C_element047,F_element011,I_element002]
  conduct = 2
  density = 1
  expand = 3
  formula = G4_FREON-13I1
  name = G4_FREON-13I1
  specific = 4
FEATURE [App::DocumentObjectGroupPython] Gd_element001  label="Gd_element : 2"  # scripted group (container) (typed FeaturePython)
  n = 2
  ref = Gd_element
FEATURE [App::DocumentObjectGroupPython] O_element041  label="O_element : 021"  # scripted group (container) (typed FeaturePython)
  n = 2
  ref = O_element
FEATURE [App::DocumentObjectGroupPython] S_element012  label="S_element : 004"  # scripted group (container) (typed FeaturePython)
  n = 1
  ref = S_element
FEATURE [App::DocumentObjectGroupPython] G4_GADOLINIUM_OXYSULFIDE  # scripted group (container) (typed FeaturePython)
  Dunit = g/cm3
  Dvalue = 7.44
  Group = -> [Gd_element001,O_element041,S_element012]
  conduct = 2
  density = 1
  expand = 3
  formula = G4_GADOLINIUM_OXYSULFIDE
  name = G4_GADOLINIUM_OXYSULFIDE
  specific = 4
FEATURE [App::DocumentObjectGroupPython] Ga_element001  label="Ga_element : 1"  # scripted group (container) (typed FeaturePython)
  n = 1
  ref = Ga_element
FEATURE [App::DocumentObjectGroupPython] As_element001  label="As_element : 1"  # scripted group (container) (typed FeaturePython)
  n = 1
  ref = As_element
FEATURE [App::DocumentObjectGroupPython] G4_GALLIUM_ARSENIDE  # scripted group (container) (typed FeaturePython)
  Dunit = g/cm3
  Dvalue = 5.31
  Group = -> [Ga_element001,As_element001]
  conduct = 2
  density = 1
  expand = 3
  formula = G4_GALLIUM_ARSENIDE
  name = G4_GALLIUM_ARSENIDE
  specific = 4
FEATURE [App::DocumentObjectGroupPython] H_element041  label="H_element : 0.081"  # scripted group (container) (typed FeaturePython)
  n = 0.08118
FEATURE [App::DocumentObjectGroupPython] C_element048  label="C_element : 0.416"  # scripted group (container) (typed FeaturePython)
  n = 0.41606
FEATURE [App::DocumentObjectGroupPython] N_element018  label="N_element : 0.111"  # scripted group (container) (typed FeaturePython)
  n = 0.11124
FEATURE [App::DocumentObjectGroupPython] O_element042  label="O_element : 0.381"  # scripted group (container) (typed FeaturePython)
  n = 0.38064
FEATURE [App::DocumentObjectGroupPython] S_element013  label="S_element : 0.011"  # scripted group (container) (typed FeaturePython)
  n = 0.01088
FEATURE [App::DocumentObjectGroupPython] G4_GEL_PHOTO_EMULSION  # scripted group (container) (typed FeaturePython)
  Dunit = g/cm3
  Dvalue = 1.2914
  Group = -> [H_element041,C_element048,N_element018,O_element042,S_element013]
  conduct = 2
  density = 1
  expand = 3
  formula = G4_GEL_PHOTO_EMULSION
  name = G4_GEL_PHOTO_EMULSION
  specific = 4
FEATURE [App::DocumentObjectGroupPython] B_element004  label="B_element : 0.040"  # scripted group (container) (typed FeaturePython)
  n = 0.0400639
FEATURE [App::DocumentObjectGroupPython] O_element043  label="O_element : 0.540"  # scripted group (container) (typed FeaturePython)
  n = 0.539561
FEATURE [App::DocumentObjectGroupPython] Na_element008  label="Na_element : 0.028"  # scripted group (container) (typed FeaturePython)
  n = 0.0281909
FEATURE [App::DocumentObjectGroupPython] Al_element003  label="Al_element : 0.012"  # scripted group (container) (typed FeaturePython)
  n = 0.011644
FEATURE [App::DocumentObjectGroupPython] Si_element003  label="Si_element : 0.377"  # scripted group (container) (typed FeaturePython)
  n = 0.377219
FEATURE [App::DocumentObjectGroupPython] K_element004  label="K_element : 0.014"  # scripted group (container) (typed FeaturePython)
  n = 0.00332099
FEATURE [App::DocumentObjectGroupPython] G4_Pyrex_Glass  # scripted group (container) (typed FeaturePython)
  Dunit = g/cm3
  Dvalue = 2.23
  Group = -> [B_element004,O_element043,Na_element008,Al_element003,Si_element003,K_element004]
  conduct = 2
  density = 1
  expand = 3
  formula = G4_Pyrex_Glass
  name = G4_Pyrex_Glass
  specific = 4
FEATURE [App::DocumentObjectGroupPython] O_element044  label="O_element : 0.156"  # scripted group (container) (typed FeaturePython)
  n = 0.156453
FEATURE [App::DocumentObjectGroupPython] Si_element004  label="Si_element : 0.081"  # scripted group (container) (typed FeaturePython)
  n = 0.080866
FEATURE [App::DocumentObjectGroupPython] Ti_element001  label="Ti_element : 0.008"  # scripted group (container) (typed FeaturePython)
  n = 0.008092
FEATURE [App::DocumentObjectGroupPython] As_element002  label="As_element : 0.003"  # scripted group (container) (typed FeaturePython)
  n = 0.002651
FEATURE [App::DocumentObjectGroupPython] Pb_element001  label="Pb_element : 0.752"  # scripted group (container) (typed FeaturePython)
  n = 0.751938
FEATURE [App::DocumentObjectGroupPython] G4_GLASS_LEAD  # scripted group (container) (typed FeaturePython)
  Dunit = g/cm3
  Dvalue = 6.22
  Group = -> [O_element044,Si_element004,Ti_element001,As_element002,Pb_element001]
  conduct = 2
  density = 1
  expand = 3
  formula = G4_GLASS_LEAD
  name = G4_GLASS_LEAD
  specific = 4
FEATURE [App::DocumentObjectGroupPython] O_element045  label="O_element : 0.460"  # scripted group (container) (typed FeaturePython)
  n = 0.4598
FEATURE [App::DocumentObjectGroupPython] Na_element009  label="Na_element : 0.096"  # scripted group (container) (typed FeaturePython)
  n = 0.0964411
FEATURE [App::DocumentObjectGroupPython] Si_element005  label="Si_element : 0.378"  # scripted group (container) (typed FeaturePython)
  n = 0.336553
FEATURE [App::DocumentObjectGroupPython] Ca_element011  label="Ca_element : 0.107"  # scripted group (container) (typed FeaturePython)
  n = 0.107205
FEATURE [App::DocumentObjectGroupPython] G4_GLASS_PLATE  # scripted group (container) (typed FeaturePython)
  Dunit = g/cm3
  Dvalue = 2.4
  Group = -> [O_element045,Na_element009,Si_element005,Ca_element011]
  conduct = 2
  density = 1
  expand = 3
  formula = G4_GLASS_PLATE
  name = G4_GLASS_PLATE
  specific = 4
FEATURE [App::DocumentObjectGroupPython] C_element049  label="C_element : 026"  # scripted group (container) (typed FeaturePython)
  n = 5
  ref = C_element
FEATURE [App::DocumentObjectGroupPython] H_element042  label="H_element : 021"  # scripted group (container) (typed FeaturePython)
  n = 10
  ref = H_element
FEATURE [App::DocumentObjectGroupPython] N_element019  label="N_element : 2"  # scripted group (container) (typed FeaturePython)
  n = 2
  ref = N_element
FEATURE [App::DocumentObjectGroupPython] O_element046  label="O_element : 022"  # scripted group (container) (typed FeaturePython)
  n = 3
  ref = O_element
FEATURE [App::DocumentObjectGroupPython] G4_GLUTAMINE  # scripted group (container) (typed FeaturePython)
  Dunit = g/cm3
  Dvalue = 1.46
  Group = -> [C_element049,H_element042,N_element019,O_element046]
  conduct = 2
  density = 1
  expand = 3
  formula = G4_GLUTAMINE
  name = G4_GLUTAMINE
  specific = 4
FEATURE [App::DocumentObjectGroupPython] C_element050  label="C_element : 027"  # scripted group (container) (typed FeaturePython)
  n = 3
  ref = C_element
FEATURE [App::DocumentObjectGroupPython] H_element043  label="H_element : 022"  # scripted group (container) (typed FeaturePython)
  n = 8
  ref = H_element
FEATURE [App::DocumentObjectGroupPython] O_element047  label="O_element : 023"  # scripted group (container) (typed FeaturePython)
  n = 3
  ref = O_element
FEATURE [App::DocumentObjectGroupPython] G4_GLYCEROL  # scripted group (container) (typed FeaturePython)
  Dunit = g/cm3
  Dvalue = 1.2613
  Group = -> [C_element050,H_element043,O_element047]
  conduct = 2
  density = 1
  expand = 3
  formula = G4_GLYCEROL
  name = G4_GLYCEROL
  specific = 4
FEATURE [App::DocumentObjectGroupPython] C_element051  label="C_element : 028"  # scripted group (container) (typed FeaturePython)
  n = 5
  ref = C_element
FEATURE [App::DocumentObjectGroupPython] H_element044  label="H_element : 023"  # scripted group (container) (typed FeaturePython)
  n = 5
  ref = H_element
FEATURE [App::DocumentObjectGroupPython] N_element020  label="N_element : 009"  # scripted group (container) (typed FeaturePython)
  n = 5
  ref = N_element
FEATURE [App::DocumentObjectGroupPython] O_element048  label="O_element : 024"  # scripted group (container) (typed FeaturePython)
  n = 1
  ref = O_element
FEATURE [App::DocumentObjectGroupPython] G4_GUANINE  # scripted group (container) (typed FeaturePython)
  Dunit = g/cm3
  Dvalue = 2.2
  Group = -> [C_element051,H_element044,N_element020,O_element048]
  conduct = 2
  density = 1
  expand = 3
  formula = G4_GUANINE
  name = G4_GUANINE
  specific = 4
FEATURE [App::DocumentObjectGroupPython] Ca_element012  label="Ca_element : 006"  # scripted group (container) (typed FeaturePython)
  n = 1
  ref = Ca_element
FEATURE [App::DocumentObjectGroupPython] S_element014  label="S_element : 005"  # scripted group (container) (typed FeaturePython)
  n = 1
  ref = S_element
FEATURE [App::DocumentObjectGroupPython] O_element049  label="O_element : 6"  # scripted group (container) (typed FeaturePython)
  n = 6
  ref = O_element
FEATURE [App::DocumentObjectGroupPython] H_element045  label="H_element : 024"  # scripted group (container) (typed FeaturePython)
  n = 4
  ref = H_element
FEATURE [App::DocumentObjectGroupPython] G4_GYPSUM  # scripted group (container) (typed FeaturePython)
  Dunit = g/cm3
  Dvalue = 2.32
  Group = -> [Ca_element012,S_element014,O_element049,H_element045]
  conduct = 2
  density = 1
  expand = 3
  formula = G4_GYPSUM
  name = G4_GYPSUM
  specific = 4
FEATURE [App::DocumentObjectGroupPython] C_element052  label="C_element : 7"  # scripted group (container) (typed FeaturePython)
  n = 7
  ref = C_element
FEATURE [App::DocumentObjectGroupPython] H_element046  label="H_element : 16"  # scripted group (container) (typed FeaturePython)
  n = 16
  ref = H_element
FEATURE [App::DocumentObjectGroupPython] G4_N_HEPTANE  label="G4_N-HEPTANE"  # scripted group (container) (typed FeaturePython)
  Dunit = g/cm3
  Dvalue = 0.68376
  Group = -> [C_element052,H_element046]
  conduct = 2
  density = 1
  expand = 3
  formula = G4_N-HEPTANE
  name = G4_N-HEPTANE
  specific = 4
FEATURE [App::DocumentObjectGroupPython] C_element053  label="C_element : 029"  # scripted group (container) (typed FeaturePython)
  n = 6
  ref = C_element
FEATURE [App::DocumentObjectGroupPython] H_element047  label="H_element : 14"  # scripted group (container) (typed FeaturePython)
  n = 14
  ref = H_element
FEATURE [App::DocumentObjectGroupPython] G4_N_HEXANE  label="G4_N-HEXANE"  # scripted group (container) (typed FeaturePython)
  Dunit = g/cm3
  Dvalue = 0.6603
  Group = -> [C_element053,H_element047]
  conduct = 2
  density = 1
  expand = 3
  formula = G4_N-HEXANE
  name = G4_N-HEXANE
  specific = 4
FEATURE [App::DocumentObjectGroupPython] C_element054  label="C_element : 22"  # scripted group (container) (typed FeaturePython)
  n = 22
  ref = C_element
FEATURE [App::DocumentObjectGroupPython] H_element048  label="H_element : 025"  # scripted group (container) (typed FeaturePython)
  n = 10
  ref = H_element
FEATURE [App::DocumentObjectGroupPython] N_element021  label="N_element : 010"  # scripted group (container) (typed FeaturePython)
  n = 2
  ref = N_element
FEATURE [App::DocumentObjectGroupPython] O_element050  label="O_element : 025"  # scripted group (container) (typed FeaturePython)
  n = 5
  ref = O_element
FEATURE [App::DocumentObjectGroupPython] G4_KAPTON  # scripted group (container) (typed FeaturePython)
  Dunit = g/cm3
  Dvalue = 1.42
  Group = -> [C_element054,H_element048,N_element021,O_element050]
  conduct = 2
  density = 1
  expand = 3
  formula = G4_KAPTON
  name = G4_KAPTON
  specific = 4
FEATURE [App::DocumentObjectGroupPython] La_element001  label="La_element : 1"  # scripted group (container) (typed FeaturePython)
  n = 1
  ref = La_element
FEATURE [App::DocumentObjectGroupPython] Br_element003  label="Br_element : 002"  # scripted group (container) (typed FeaturePython)
  n = 1
  ref = Br_element
FEATURE [App::DocumentObjectGroupPython] O_element051  label="O_element : 026"  # scripted group (container) (typed FeaturePython)
  n = 1
  ref = O_element
FEATURE [App::DocumentObjectGroupPython] G4_LANTHANUM_OXYBROMIDE  # scripted group (container) (typed FeaturePython)
  Dunit = g/cm3
  Dvalue = 6.28
  Group = -> [La_element001,Br_element003,O_element051]
  conduct = 2
  density = 1
  expand = 3
  formula = G4_LANTHANUM_OXYBROMIDE
  name = G4_LANTHANUM_OXYBROMIDE
  specific = 4
FEATURE [App::DocumentObjectGroupPython] La_element002  label="La_element : 2"  # scripted group (container) (typed FeaturePython)
  n = 2
  ref = La_element
FEATURE [App::DocumentObjectGroupPython] O_element052  label="O_element : 027"  # scripted group (container) (typed FeaturePython)
  n = 2
  ref = O_element
FEATURE [App::DocumentObjectGroupPython] S_element015  label="S_element : 006"  # scripted group (container) (typed FeaturePython)
  n = 1
  ref = S_element
FEATURE [App::DocumentObjectGroupPython] G4_LANTHANUM_OXYSULFIDE  # scripted group (container) (typed FeaturePython)
  Dunit = g/cm3
  Dvalue = 5.86
  Group = -> [La_element002,O_element052,S_element015]
  conduct = 2
  density = 1
  expand = 3
  formula = G4_LANTHANUM_OXYSULFIDE
  name = G4_LANTHANUM_OXYSULFIDE
  specific = 4
FEATURE [App::DocumentObjectGroupPython] O_element053  label="O_element : 0.072"  # scripted group (container) (typed FeaturePython)
  n = 0.071682
FEATURE [App::DocumentObjectGroupPython] Pb_element002  label="Pb_element : 0.928"  # scripted group (container) (typed FeaturePython)
  n = 0.928318
FEATURE [App::DocumentObjectGroupPython] G4_LEAD_OXIDE  # scripted group (container) (typed FeaturePython)
  Dunit = g/cm3
  Dvalue = 9.53
  Group = -> [O_element053,Pb_element002]
  conduct = 2
  density = 1
  expand = 3
  formula = G4_LEAD_OXIDE
  name = G4_LEAD_OXIDE
  specific = 4
FEATURE [App::DocumentObjectGroupPython] Li_element001  label="Li_element : 1"  # scripted group (container) (typed FeaturePython)
  n = 1
  ref = Li_element
FEATURE [App::DocumentObjectGroupPython] N_element022  label="N_element : 011"  # scripted group (container) (typed FeaturePython)
  n = 1
  ref = N_element
FEATURE [App::DocumentObjectGroupPython] H_element049  label="H_element : 026"  # scripted group (container) (typed FeaturePython)
  n = 2
  ref = H_element
FEATURE [App::DocumentObjectGroupPython] G4_LITHIUM_AMIDE  # scripted group (container) (typed FeaturePython)
  Dunit = g/cm3
  Dvalue = 1.178
  Group = -> [Li_element001,N_element022,H_element049]
  conduct = 2
  density = 1
  expand = 3
  formula = G4_LITHIUM_AMIDE
  name = G4_LITHIUM_AMIDE
  specific = 4
FEATURE [App::DocumentObjectGroupPython] Li_element002  label="Li_element : 2"  # scripted group (container) (typed FeaturePython)
  n = 2
  ref = Li_element
FEATURE [App::DocumentObjectGroupPython] C_element055  label="C_element : 030"  # scripted group (container) (typed FeaturePython)
  n = 1
  ref = C_element
FEATURE [App::DocumentObjectGroupPython] O_element054  label="O_element : 028"  # scripted group (container) (typed FeaturePython)
  n = 3
  ref = O_element
FEATURE [App::DocumentObjectGroupPython] G4_LITHIUM_CARBONATE  # scripted group (container) (typed FeaturePython)
  Dunit = g/cm3
  Dvalue = 2.11
  Group = -> [Li_element002,C_element055,O_element054]
  conduct = 2
  density = 1
  expand = 3
  formula = G4_LITHIUM_CARBONATE
  name = G4_LITHIUM_CARBONATE
  specific = 4
FEATURE [App::DocumentObjectGroupPython] Li_element003  label="Li_element : 003"  # scripted group (container) (typed FeaturePython)
  n = 1
  ref = Li_element
FEATURE [App::DocumentObjectGroupPython] F_element012  label="F_element : 004"  # scripted group (container) (typed FeaturePython)
  n = 1
  ref = F_element
FEATURE [App::DocumentObjectGroupPython] G4_LITHIUM_FLUORIDE  # scripted group (container) (typed FeaturePython)
  Dunit = g/cm3
  Dvalue = 2.635
  Group = -> [Li_element003,F_element012]
  conduct = 2
  density = 1
  expand = 3
  formula = G4_LITHIUM_FLUORIDE
  name = G4_LITHIUM_FLUORIDE
  specific = 4
FEATURE [App::DocumentObjectGroupPython] Li_element004  label="Li_element : 004"  # scripted group (container) (typed FeaturePython)
  n = 1
  ref = Li_element
FEATURE [App::DocumentObjectGroupPython] H_element050  label="H_element : 027"  # scripted group (container) (typed FeaturePython)
  n = 1
  ref = H_element
FEATURE [App::DocumentObjectGroupPython] G4_LITHIUM_HYDRIDE  # scripted group (container) (typed FeaturePython)
  Dunit = g/cm3
  Dvalue = 0.82
  Group = -> [Li_element004,H_element050]
  conduct = 2
  density = 1
  expand = 3
  formula = G4_LITHIUM_HYDRIDE
  name = G4_LITHIUM_HYDRIDE
  specific = 4
FEATURE [App::DocumentObjectGroupPython] Li_element005  label="Li_element : 005"  # scripted group (container) (typed FeaturePython)
  n = 1
  ref = Li_element
FEATURE [App::DocumentObjectGroupPython] I_element003  label="I_element : 002"  # scripted group (container) (typed FeaturePython)
  n = 1
  ref = I_element
FEATURE [App::DocumentObjectGroupPython] G4_LITHIUM_IODIDE  # scripted group (container) (typed FeaturePython)
  Dunit = g/cm3
  Dvalue = 3.494
  Group = -> [Li_element005,I_element003]
  conduct = 2
  density = 1
  expand = 3
  formula = G4_LITHIUM_IODIDE
  name = G4_LITHIUM_IODIDE
  specific = 4
FEATURE [App::DocumentObjectGroupPython] Li_element006  label="Li_element : 006"  # scripted group (container) (typed FeaturePython)
  n = 2
  ref = Li_element
FEATURE [App::DocumentObjectGroupPython] O_element055  label="O_element : 029"  # scripted group (container) (typed FeaturePython)
  n = 1
  ref = O_element
FEATURE [App::DocumentObjectGroupPython] G4_LITHIUM_OXIDE  # scripted group (container) (typed FeaturePython)
  Dunit = g/cm3
  Dvalue = 2.013
  Group = -> [Li_element006,O_element055]
  conduct = 2
  density = 1
  expand = 3
  formula = G4_LITHIUM_OXIDE
  name = G4_LITHIUM_OXIDE
  specific = 4
FEATURE [App::DocumentObjectGroupPython] Li_element007  label="Li_element : 007"  # scripted group (container) (typed FeaturePython)
  n = 2
  ref = Li_element
FEATURE [App::DocumentObjectGroupPython] B_element005  label="B_element : 005"  # scripted group (container) (typed FeaturePython)
  n = 4
  ref = B_element
FEATURE [App::DocumentObjectGroupPython] O_element056  label="O_element : 7"  # scripted group (container) (typed FeaturePython)
  n = 7
  ref = O_element
FEATURE [App::DocumentObjectGroupPython] G4_LITHIUM_TETRABORATE  # scripted group (container) (typed FeaturePython)
  Dunit = g/cm3
  Dvalue = 2.44
  Group = -> [Li_element007,B_element005,O_element056]
  conduct = 2
  density = 1
  expand = 3
  formula = G4_LITHIUM_TETRABORATE
  name = G4_LITHIUM_TETRABORATE
  specific = 4
FEATURE [App::DocumentObjectGroupPython] H_element051  label="H_element : 0.105"  # scripted group (container) (typed FeaturePython)
  n = 0.105
FEATURE [App::DocumentObjectGroupPython] C_element056  label="C_element : 0.083"  # scripted group (container) (typed FeaturePython)
  n = 0.083
FEATURE [App::DocumentObjectGroupPython] N_element023  label="N_element : 0.023"  # scripted group (container) (typed FeaturePython)
  n = 0.023
FEATURE [App::DocumentObjectGroupPython] O_element057  label="O_element : 0.779"  # scripted group (container) (typed FeaturePython)
  n = 0.779
FEATURE [App::DocumentObjectGroupPython] Na_element010  label="Na_element : 0.097"  # scripted group (container) (typed FeaturePython)
  n = 0.002
FEATURE [App::DocumentObjectGroupPython] P_element006  label="P_element : 0.105"  # scripted group (container) (typed FeaturePython)
  n = 0.001
FEATURE [App::DocumentObjectGroupPython] S_element016  label="S_element : 0.017"  # scripted group (container) (typed FeaturePython)
  n = 0.002
FEATURE [App::DocumentObjectGroupPython] Cl_element014  label="Cl_element : 0.587"  # scripted group (container) (typed FeaturePython)
  n = 0.003
FEATURE [App::DocumentObjectGroupPython] K_element005  label="K_element : 0.015"  # scripted group (container) (typed FeaturePython)
  n = 0.002
FEATURE [App::DocumentObjectGroupPython] G4_LUNG_ICRP  # scripted group (container) (typed FeaturePython)
  Dunit = g/cm3
  Dvalue = 1.04
  Group = -> [H_element051,C_element056,N_element023,O_element057,Na_element010,P_element006,S_element016,Cl_element014,K_element005]
  conduct = 2
  density = 1
  expand = 3
  formula = G4_LUNG_ICRP
  name = G4_LUNG_ICRP
  specific = 4
FEATURE [App::DocumentObjectGroupPython] H_element052  label="H_element : 0.116"  # scripted group (container) (typed FeaturePython)
  n = 0.114318
FEATURE [App::DocumentObjectGroupPython] C_element057  label="C_element : 0.656"  # scripted group (container) (typed FeaturePython)
  n = 0.655824
FEATURE [App::DocumentObjectGroupPython] O_element058  label="O_element : 0.092"  # scripted group (container) (typed FeaturePython)
  n = 0.0921831
FEATURE [App::DocumentObjectGroupPython] Mg_element004  label="Mg_element : 0.135"  # scripted group (container) (typed FeaturePython)
  n = 0.134792
FEATURE [App::DocumentObjectGroupPython] Ca_element013  label="Ca_element : 0.003"  # scripted group (container) (typed FeaturePython)
  n = 0.002883
FEATURE [App::DocumentObjectGroupPython] G4_M3_WAX  # scripted group (container) (typed FeaturePython)
  Dunit = g/cm3
  Dvalue = 1.05
  Group = -> [H_element052,C_element057,O_element058,Mg_element004,Ca_element013]
  conduct = 2
  density = 1
  expand = 3
  formula = G4_M3_WAX
  name = G4_M3_WAX
  specific = 4
FEATURE [App::DocumentObjectGroupPython] Mg_element005  label="Mg_element : 1"  # scripted group (container) (typed FeaturePython)
  n = 1
  ref = Mg_element
FEATURE [App::DocumentObjectGroupPython] C_element058  label="C_element : 031"  # scripted group (container) (typed FeaturePython)
  n = 1
  ref = C_element
FEATURE [App::DocumentObjectGroupPython] O_element059  label="O_element : 030"  # scripted group (container) (typed FeaturePython)
  n = 3
  ref = O_element
FEATURE [App::DocumentObjectGroupPython] G4_MAGNESIUM_CARBONATE  # scripted group (container) (typed FeaturePython)
  Dunit = g/cm3
  Dvalue = 2.958
  Group = -> [Mg_element005,C_element058,O_element059]
  conduct = 2
  density = 1
  expand = 3
  formula = G4_MAGNESIUM_CARBONATE
  name = G4_MAGNESIUM_CARBONATE
  specific = 4
FEATURE [App::DocumentObjectGroupPython] Mg_element006  label="Mg_element : 002"  # scripted group (container) (typed FeaturePython)
  n = 1
  ref = Mg_element
FEATURE [App::DocumentObjectGroupPython] F_element013  label="F_element : 005"  # scripted group (container) (typed FeaturePython)
  n = 2
  ref = F_element
FEATURE [App::DocumentObjectGroupPython] G4_MAGNESIUM_FLUORIDE  # scripted group (container) (typed FeaturePython)
  Dunit = g/cm3
  Dvalue = 3
  Group = -> [Mg_element006,F_element013]
  conduct = 2
  density = 1
  expand = 3
  formula = G4_MAGNESIUM_FLUORIDE
  name = G4_MAGNESIUM_FLUORIDE
  specific = 4
FEATURE [App::DocumentObjectGroupPython] Mg_element007  label="Mg_element : 003"  # scripted group (container) (typed FeaturePython)
  n = 1
  ref = Mg_element
FEATURE [App::DocumentObjectGroupPython] O_element060  label="O_element : 031"  # scripted group (container) (typed FeaturePython)
  n = 1
  ref = O_element
FEATURE [App::DocumentObjectGroupPython] G4_MAGNESIUM_OXIDE  # scripted group (container) (typed FeaturePython)
  Dunit = g/cm3
  Dvalue = 3.58
  Group = -> [Mg_element007,O_element060]
  conduct = 2
  density = 1
  expand = 3
  formula = G4_MAGNESIUM_OXIDE
  name = G4_MAGNESIUM_OXIDE
  specific = 4
FEATURE [App::DocumentObjectGroupPython] Mg_element008  label="Mg_element : 004"  # scripted group (container) (typed FeaturePython)
  n = 1
  ref = Mg_element
FEATURE [App::DocumentObjectGroupPython] B_element006  label="B_element : 006"  # scripted group (container) (typed FeaturePython)
  n = 4
  ref = B_element
FEATURE [App::DocumentObjectGroupPython] O_element061  label="O_element : 032"  # scripted group (container) (typed FeaturePython)
  n = 7
  ref = O_element
FEATURE [App::DocumentObjectGroupPython] G4_MAGNESIUM_TETRABORATE  # scripted group (container) (typed FeaturePython)
  Dunit = g/cm3
  Dvalue = 2.53
  Group = -> [Mg_element008,B_element006,O_element061]
  conduct = 2
  density = 1
  expand = 3
  formula = G4_MAGNESIUM_TETRABORATE
  name = G4_MAGNESIUM_TETRABORATE
  specific = 4
FEATURE [App::DocumentObjectGroupPython] Hg_element001  label="Hg_element : 1"  # scripted group (container) (typed FeaturePython)
  n = 1
  ref = Hg_element
FEATURE [App::DocumentObjectGroupPython] I_element004  label="I_element : 2"  # scripted group (container) (typed FeaturePython)
  n = 2
  ref = I_element
FEATURE [App::DocumentObjectGroupPython] G4_MERCURIC_IODIDE  # scripted group (container) (typed FeaturePython)
  Dunit = g/cm3
  Dvalue = 6.36
  Group = -> [Hg_element001,I_element004]
  conduct = 2
  density = 1
  expand = 3
  formula = G4_MERCURIC_IODIDE
  name = G4_MERCURIC_IODIDE
  specific = 4
FEATURE [App::DocumentObjectGroupPython] C_element059  label="C_element : 032"  # scripted group (container) (typed FeaturePython)
  n = 1
  ref = C_element
FEATURE [App::DocumentObjectGroupPython] H_element053  label="H_element : 028"  # scripted group (container) (typed FeaturePython)
  n = 4
  ref = H_element
FEATURE [App::DocumentObjectGroupPython] G4_METHANE  # scripted group (container) (typed FeaturePython)
  Dunit = g/cm3
  Dvalue = 0.000667151
  Group = -> [C_element059,H_element053]
  conduct = 2
  density = 1
  expand = 3
  formula = G4_METHANE
  name = G4_METHANE
  specific = 4
FEATURE [App::DocumentObjectGroupPython] C_element060  label="C_element : 033"  # scripted group (container) (typed FeaturePython)
  n = 1
  ref = C_element
FEATURE [App::DocumentObjectGroupPython] H_element054  label="H_element : 029"  # scripted group (container) (typed FeaturePython)
  n = 4
  ref = H_element
FEATURE [App::DocumentObjectGroupPython] O_element062  label="O_element : 033"  # scripted group (container) (typed FeaturePython)
  n = 1
  ref = O_element
FEATURE [App::DocumentObjectGroupPython] G4_METHANOL  # scripted group (container) (typed FeaturePython)
  Dunit = g/cm3
  Dvalue = 0.7914
  Group = -> [C_element060,H_element054,O_element062]
  conduct = 2
  density = 1
  expand = 3
  formula = G4_METHANOL
  name = G4_METHANOL
  specific = 4
FEATURE [App::DocumentObjectGroupPython] H_element055  label="H_element : 0.134"  # scripted group (container) (typed FeaturePython)
  n = 0.13404
FEATURE [App::DocumentObjectGroupPython] C_element061  label="C_element : 0.778"  # scripted group (container) (typed FeaturePython)
  n = 0.77796
FEATURE [App::DocumentObjectGroupPython] O_element063  label="O_element : 0.035"  # scripted group (container) (typed FeaturePython)
  n = 0.03502
FEATURE [App::DocumentObjectGroupPython] Mg_element009  label="Mg_element : 0.039"  # scripted group (container) (typed FeaturePython)
  n = 0.038594
FEATURE [App::DocumentObjectGroupPython] Ti_element002  label="Ti_element : 0.014"  # scripted group (container) (typed FeaturePython)
  n = 0.014386
FEATURE [App::DocumentObjectGroupPython] G4_MIX_D_WAX  # scripted group (container) (typed FeaturePython)
  Dunit = g/cm3
  Dvalue = 0.99
  Group = -> [H_element055,C_element061,O_element063,Mg_element009,Ti_element002]
  conduct = 2
  density = 1
  expand = 3
  formula = G4_MIX_D_WAX
  name = G4_MIX_D_WAX
  specific = 4
FEATURE [App::DocumentObjectGroupPython] H_element056  label="H_element : 0.135"  # scripted group (container) (typed FeaturePython)
  n = 0.081192
FEATURE [App::DocumentObjectGroupPython] C_element062  label="C_element : 0.583"  # scripted group (container) (typed FeaturePython)
  n = 0.583442
FEATURE [App::DocumentObjectGroupPython] N_element024  label="N_element : 0.018"  # scripted group (container) (typed FeaturePython)
  n = 0.017798
FEATURE [App::DocumentObjectGroupPython] O_element064  label="O_element : 0.186"  # scripted group (container) (typed FeaturePython)
  n = 0.186381
FEATURE [App::DocumentObjectGroupPython] Mg_element010  label="Mg_element : 0.130"  # scripted group (container) (typed FeaturePython)
  n = 0.130287
FEATURE [App::DocumentObjectGroupPython] Cl_element015  label="Cl_element : 0.588"  # scripted group (container) (typed FeaturePython)
  n = 0.0009
FEATURE [App::DocumentObjectGroupPython] G4_MS20_TISSUE  # scripted group (container) (typed FeaturePython)
  Dunit = g/cm3
  Dvalue = 1
  Group = -> [H_element056,C_element062,N_element024,O_element064,Mg_element010,Cl_element015]
  conduct = 2
  density = 1
  expand = 3
  formula = G4_MS20_TISSUE
  name = G4_MS20_TISSUE
  specific = 4
FEATURE [App::DocumentObjectGroupPython] H_element057  label="H_element : 0.136"  # scripted group (container) (typed FeaturePython)
  n = 0.102
FEATURE [App::DocumentObjectGroupPython] C_element063  label="C_element : 0.143"  # scripted group (container) (typed FeaturePython)
  n = 0.143
FEATURE [App::DocumentObjectGroupPython] N_element025  label="N_element : 0.034"  # scripted group (container) (typed FeaturePython)
  n = 0.034
FEATURE [App::DocumentObjectGroupPython] O_element065  label="O_element : 0.710"  # scripted group (container) (typed FeaturePython)
  n = 0.71
FEATURE [App::DocumentObjectGroupPython] Na_element011  label="Na_element : 0.098"  # scripted group (container) (typed FeaturePython)
  n = 0.001
FEATURE [App::DocumentObjectGroupPython] P_element007  label="P_element : 0.002"  # scripted group (container) (typed FeaturePython)
  n = 0.002
FEATURE [App::DocumentObjectGroupPython] S_element017  label="S_element : 0.018"  # scripted group (container) (typed FeaturePython)
  n = 0.003
FEATURE [App::DocumentObjectGroupPython] Cl_element016  label="Cl_element : 0.589"  # scripted group (container) (typed FeaturePython)
  n = 0.001
FEATURE [App::DocumentObjectGroupPython] K_element006  label="K_element : 0.004"  # scripted group (container) (typed FeaturePython)
  n = 0.004
FEATURE [App::DocumentObjectGroupPython] G4_MUSCLE_SKELETAL_ICRP  # scripted group (container) (typed FeaturePython)
  Dunit = g/cm3
  Dvalue = 1.05
  Group = -> [H_element057,C_element063,N_element025,O_element065,Na_element011,P_element007,S_element017,Cl_element016,K_element006]
  conduct = 2
  density = 1
  expand = 3
  formula = G4_MUSCLE_SKELETAL_ICRP
  name = G4_MUSCLE_SKELETAL_ICRP
  specific = 4
FEATURE [App::DocumentObjectGroupPython] H_element058  label="H_element : 0.137"  # scripted group (container) (typed FeaturePython)
  n = 0.102102
FEATURE [App::DocumentObjectGroupPython] C_element064  label="C_element : 0.123"  # scripted group (container) (typed FeaturePython)
  n = 0.123123
FEATURE [App::DocumentObjectGroupPython] N_element026  label="N_element : 0.756"  # scripted group (container) (typed FeaturePython)
  n = 0.035035
FEATURE [App::DocumentObjectGroupPython] O_element066  label="O_element : 0.730"  # scripted group (container) (typed FeaturePython)
  n = 0.72973
FEATURE [App::DocumentObjectGroupPython] Na_element012  label="Na_element : 0.099"  # scripted group (container) (typed FeaturePython)
  n = 0.001001
FEATURE [App::DocumentObjectGroupPython] P_element008  label="P_element : 0.106"  # scripted group (container) (typed FeaturePython)
  n = 0.002002
FEATURE [App::DocumentObjectGroupPython] S_element018  label="S_element : 0.019"  # scripted group (container) (typed FeaturePython)
  n = 0.004004
FEATURE [App::DocumentObjectGroupPython] K_element007  label="K_element : 0.016"  # scripted group (container) (typed FeaturePython)
  n = 0.003003
FEATURE [App::DocumentObjectGroupPython] G4_MUSCLE_STRIATED_ICRU  # scripted group (container) (typed FeaturePython)
  Dunit = g/cm3
  Dvalue = 1.04
  Group = -> [H_element058,C_element064,N_element026,O_element066,Na_element012,P_element008,S_element018,K_element007]
  conduct = 2
  density = 1
  expand = 3
  formula = G4_MUSCLE_STRIATED_ICRU
  name = G4_MUSCLE_STRIATED_ICRU
  specific = 4
FEATURE [App::DocumentObjectGroupPython] H_element059  label="H_element : 0.098"  # scripted group (container) (typed FeaturePython)
  n = 0.0982341
FEATURE [App::DocumentObjectGroupPython] C_element065  label="C_element : 0.156"  # scripted group (container) (typed FeaturePython)
  n = 0.156214
FEATURE [App::DocumentObjectGroupPython] N_element027  label="N_element : 0.757"  # scripted group (container) (typed FeaturePython)
  n = 0.035451
FEATURE [App::DocumentObjectGroupPython] O_element067  label="O_element : 0.880"  # scripted group (container) (typed FeaturePython)
  n = 0.710101
FEATURE [App::DocumentObjectGroupPython] G4_MUSCLE_WITH_SUCROSE  # scripted group (container) (typed FeaturePython)
  Dunit = g/cm3
  Dvalue = 1.11
  Group = -> [H_element059,C_element065,N_element027,O_element067]
  conduct = 2
  density = 1
  expand = 3
  formula = G4_MUSCLE_WITH_SUCROSE
  name = G4_MUSCLE_WITH_SUCROSE
  specific = 4
FEATURE [App::DocumentObjectGroupPython] H_element060  label="H_element : 0.138"  # scripted group (container) (typed FeaturePython)
  n = 0.101969
FEATURE [App::DocumentObjectGroupPython] C_element066  label="C_element : 0.120"  # scripted group (container) (typed FeaturePython)
  n = 0.120058
FEATURE [App::DocumentObjectGroupPython] N_element028  label="N_element : 0.758"  # scripted group (container) (typed FeaturePython)
  n = 0.035451
FEATURE [App::DocumentObjectGroupPython] O_element068  label="O_element : 0.743"  # scripted group (container) (typed FeaturePython)
  n = 0.742522
FEATURE [App::DocumentObjectGroupPython] G4_MUSCLE_WITHOUT_SUCROSE  # scripted group (container) (typed FeaturePython)
  Dunit = g/cm3
  Dvalue = 1.07
  Group = -> [H_element060,C_element066,N_element028,O_element068]
  conduct = 2
  density = 1
  expand = 3
  formula = G4_MUSCLE_WITHOUT_SUCROSE
  name = G4_MUSCLE_WITHOUT_SUCROSE
  specific = 4
FEATURE [App::DocumentObjectGroupPython] C_element067  label="C_element : 10"  # scripted group (container) (typed FeaturePython)
  n = 10
  ref = C_element
FEATURE [App::DocumentObjectGroupPython] H_element061  label="H_element : 030"  # scripted group (container) (typed FeaturePython)
  n = 8
  ref = H_element
FEATURE [App::DocumentObjectGroupPython] G4_NAPHTHALENE  # scripted group (container) (typed FeaturePython)
  Dunit = g/cm3
  Dvalue = 1.145
  Group = -> [C_element067,H_element061]
  conduct = 2
  density = 1
  expand = 3
  formula = G4_NAPHTHALENE
  name = G4_NAPHTHALENE
  specific = 4
FEATURE [App::DocumentObjectGroupPython] C_element068  label="C_element : 034"  # scripted group (container) (typed FeaturePython)
  n = 6
  ref = C_element
FEATURE [App::DocumentObjectGroupPython] H_element062  label="H_element : 031"  # scripted group (container) (typed FeaturePython)
  n = 5
  ref = H_element
FEATURE [App::DocumentObjectGroupPython] N_element029  label="N_element : 012"  # scripted group (container) (typed FeaturePython)
  n = 1
  ref = N_element
FEATURE [App::DocumentObjectGroupPython] O_element069  label="O_element : 034"  # scripted group (container) (typed FeaturePython)
  n = 2
  ref = O_element
FEATURE [App::DocumentObjectGroupPython] G4_NITROBENZENE  # scripted group (container) (typed FeaturePython)
  Dunit = g/cm3
  Dvalue = 1.19867
  Group = -> [C_element068,H_element062,N_element029,O_element069]
  conduct = 2
  density = 1
  expand = 3
  formula = G4_NITROBENZENE
  name = G4_NITROBENZENE
  specific = 4
FEATURE [App::DocumentObjectGroupPython] N_element030  label="N_element : 013"  # scripted group (container) (typed FeaturePython)
  n = 2
  ref = N_element
FEATURE [App::DocumentObjectGroupPython] O_element070  label="O_element : 035"  # scripted group (container) (typed FeaturePython)
  n = 1
  ref = O_element
FEATURE [App::DocumentObjectGroupPython] G4_NITROUS_OXIDE  # scripted group (container) (typed FeaturePython)
  Dunit = g/cm3
  Dvalue = 0.00183094
  Group = -> [N_element030,O_element070]
  conduct = 2
  density = 1
  expand = 3
  formula = G4_NITROUS_OXIDE
  name = G4_NITROUS_OXIDE
  specific = 4
FEATURE [App::DocumentObjectGroupPython] H_element063  label="H_element : 0.104"  # scripted group (container) (typed FeaturePython)
  n = 0.103509
FEATURE [App::DocumentObjectGroupPython] C_element069  label="C_element : 0.648"  # scripted group (container) (typed FeaturePython)
  n = 0.648416
FEATURE [App::DocumentObjectGroupPython] N_element031  label="N_element : 0.100"  # scripted group (container) (typed FeaturePython)
  n = 0.0995361
FEATURE [App::DocumentObjectGroupPython] O_element071  label="O_element : 0.149"  # scripted group (container) (typed FeaturePython)
  n = 0.148539
FEATURE [App::DocumentObjectGroupPython] G4_NYLON_8062  label="G4_NYLON-8062"  # scripted group (container) (typed FeaturePython)
  Dunit = g/cm3
  Dvalue = 1.08
  Group = -> [H_element063,C_element069,N_element031,O_element071]
  conduct = 2
  density = 1
  expand = 3
  formula = G4_NYLON-8062
  name = G4_NYLON-8062
  specific = 4
FEATURE [App::DocumentObjectGroupPython] C_element070  label="C_element : 035"  # scripted group (container) (typed FeaturePython)
  n = 6
  ref = C_element
FEATURE [App::DocumentObjectGroupPython] H_element064  label="H_element : 11"  # scripted group (container) (typed FeaturePython)
  n = 11
  ref = H_element
FEATURE [App::DocumentObjectGroupPython] N_element032  label="N_element : 014"  # scripted group (container) (typed FeaturePython)
  n = 1
  ref = N_element
FEATURE [App::DocumentObjectGroupPython] O_element072  label="O_element : 036"  # scripted group (container) (typed FeaturePython)
  n = 1
  ref = O_element
FEATURE [App::DocumentObjectGroupPython] G4_NYLON_6_6  label="G4_NYLON-6-6"  # scripted group (container) (typed FeaturePython)
  Dunit = g/cm3
  Dvalue = 1.14
  Group = -> [C_element070,H_element064,N_element032,O_element072]
  conduct = 2
  density = 1
  expand = 3
  formula = G4_NYLON-6-6
  name = G4_NYLON-6-6
  specific = 4
FEATURE [App::DocumentObjectGroupPython] H_element065  label="H_element : 0.139"  # scripted group (container) (typed FeaturePython)
  n = 0.107062
FEATURE [App::DocumentObjectGroupPython] C_element071  label="C_element : 0.680"  # scripted group (container) (typed FeaturePython)
  n = 0.680449
FEATURE [App::DocumentObjectGroupPython] N_element033  label="N_element : 0.099"  # scripted group (container) (typed FeaturePython)
  n = 0.099189
FEATURE [App::DocumentObjectGroupPython] O_element073  label="O_element : 0.113"  # scripted group (container) (typed FeaturePython)
  n = 0.1133
FEATURE [App::DocumentObjectGroupPython] G4_NYLON_6_10  label="G4_NYLON-6-10"  # scripted group (container) (typed FeaturePython)
  Dunit = g/cm3
  Dvalue = 1.14
  Group = -> [H_element065,C_element071,N_element033,O_element073]
  conduct = 2
  density = 1
  expand = 3
  formula = G4_NYLON-6-10
  name = G4_NYLON-6-10
  specific = 4
FEATURE [App::DocumentObjectGroupPython] H_element066  label="H_element : 0.140"  # scripted group (container) (typed FeaturePython)
  n = 0.115476
FEATURE [App::DocumentObjectGroupPython] C_element072  label="C_element : 0.721"  # scripted group (container) (typed FeaturePython)
  n = 0.720818
FEATURE [App::DocumentObjectGroupPython] N_element034  label="N_element : 0.076"  # scripted group (container) (typed FeaturePython)
  n = 0.0764169
FEATURE [App::DocumentObjectGroupPython] O_element074  label="O_element : 0.087"  # scripted group (container) (typed FeaturePython)
  n = 0.0872889
FEATURE [App::DocumentObjectGroupPython] G4_NYLON_11_RILSAN  label="G4_NYLON-11_RILSAN"  # scripted group (container) (typed FeaturePython)
  Dunit = g/cm3
  Dvalue = 1.425
  Group = -> [H_element066,C_element072,N_element034,O_element074]
  conduct = 2
  density = 1
  expand = 3
  formula = G4_NYLON-11_RILSAN
  name = G4_NYLON-11_RILSAN
  specific = 4
FEATURE [App::DocumentObjectGroupPython] C_element073  label="C_element : 8"  # scripted group (container) (typed FeaturePython)
  n = 8
  ref = C_element
FEATURE [App::DocumentObjectGroupPython] H_element067  label="H_element : 18"  # scripted group (container) (typed FeaturePython)
  n = 18
  ref = H_element
FEATURE [App::DocumentObjectGroupPython] G4_OCTANE  # scripted group (container) (typed FeaturePython)
  Dunit = g/cm3
  Dvalue = 0.7026
  Group = -> [C_element073,H_element067]
  conduct = 2
  density = 1
  expand = 3
  formula = G4_OCTANE
  name = G4_OCTANE
  specific = 4
FEATURE [App::DocumentObjectGroupPython] C_element074  label="C_element : 25"  # scripted group (container) (typed FeaturePython)
  n = 25
  ref = C_element
FEATURE [App::DocumentObjectGroupPython] H_element068  label="H_element : 52"  # scripted group (container) (typed FeaturePython)
  n = 52
  ref = H_element
FEATURE [App::DocumentObjectGroupPython] G4_PARAFFIN  # scripted group (container) (typed FeaturePython)
  Dunit = g/cm3
  Dvalue = 0.93
  Group = -> [C_element074,H_element068]
  conduct = 2
  density = 1
  expand = 3
  formula = G4_PARAFFIN
  name = G4_PARAFFIN
  specific = 4
FEATURE [App::DocumentObjectGroupPython] C_element075  label="C_element : 036"  # scripted group (container) (typed FeaturePython)
  n = 5
  ref = C_element
FEATURE [App::DocumentObjectGroupPython] H_element069  label="H_element : 032"  # scripted group (container) (typed FeaturePython)
  n = 12
  ref = H_element
FEATURE [App::DocumentObjectGroupPython] G4_N_PENTANE  label="G4_N-PENTANE"  # scripted group (container) (typed FeaturePython)
  Dunit = g/cm3
  Dvalue = 0.6262
  Group = -> [C_element075,H_element069]
  conduct = 2
  density = 1
  expand = 3
  formula = G4_N-PENTANE
  name = G4_N-PENTANE
  specific = 4
FEATURE [App::DocumentObjectGroupPython] H_element070  label="H_element : 0.014"  # scripted group (container) (typed FeaturePython)
  n = 0.0141
FEATURE [App::DocumentObjectGroupPython] C_element076  label="C_element : 0.072"  # scripted group (container) (typed FeaturePython)
  n = 0.072261
FEATURE [App::DocumentObjectGroupPython] N_element035  label="N_element : 0.019"  # scripted group (container) (typed FeaturePython)
  n = 0.01932
FEATURE [App::DocumentObjectGroupPython] O_element075  label="O_element : 0.066"  # scripted group (container) (typed FeaturePython)
  n = 0.066101
FEATURE [App::DocumentObjectGroupPython] S_element019  label="S_element : 0.020"  # scripted group (container) (typed FeaturePython)
  n = 0.00189
FEATURE [App::DocumentObjectGroupPython] Br_element004  label="Br_element : 0.349"  # scripted group (container) (typed FeaturePython)
  n = 0.349103
FEATURE [App::DocumentObjectGroupPython] Ag_element001  label="Ag_element : 0.474"  # scripted group (container) (typed FeaturePython)
  n = 0.474105
FEATURE [App::DocumentObjectGroupPython] I_element005  label="I_element : 0.003"  # scripted group (container) (typed FeaturePython)
  n = 0.00312
FEATURE [App::DocumentObjectGroupPython] G4_PHOTO_EMULSION  # scripted group (container) (typed FeaturePython)
  Dunit = g/cm3
  Dvalue = 3.815
  Group = -> [H_element070,C_element076,N_element035,O_element075,S_element019,Br_element004,Ag_element001,I_element005]
  conduct = 2
  density = 1
  expand = 3
  formula = G4_PHOTO_EMULSION
  name = G4_PHOTO_EMULSION
  specific = 4
FEATURE [App::DocumentObjectGroupPython] C_element077  label="C_element : 9"  # scripted group (container) (typed FeaturePython)
  n = 9
  ref = C_element
FEATURE [App::DocumentObjectGroupPython] H_element071  label="H_element : 033"  # scripted group (container) (typed FeaturePython)
  n = 10
  ref = H_element
FEATURE [App::DocumentObjectGroupPython] G4_PLASTIC_SC_VINYLTOLUENE  # scripted group (container) (typed FeaturePython)
  Dunit = g/cm3
  Dvalue = 1.032
  Group = -> [C_element077,H_element071]
  conduct = 2
  density = 1
  expand = 3
  formula = G4_PLASTIC_SC_VINYLTOLUENE
  name = G4_PLASTIC_SC_VINYLTOLUENE
  specific = 4
FEATURE [App::DocumentObjectGroupPython] Pu_element001  label="Pu_element : 1"  # scripted group (container) (typed FeaturePython)
  n = 1
  ref = Pu_element
FEATURE [App::DocumentObjectGroupPython] O_element076  label="O_element : 037"  # scripted group (container) (typed FeaturePython)
  n = 2
  ref = O_element
FEATURE [App::DocumentObjectGroupPython] G4_PLUTONIUM_DIOXIDE  # scripted group (container) (typed FeaturePython)
  Dunit = g/cm3
  Dvalue = 11.46
  Group = -> [Pu_element001,O_element076]
  conduct = 2
  density = 1
  expand = 3
  formula = G4_PLUTONIUM_DIOXIDE
  name = G4_PLUTONIUM_DIOXIDE
  specific = 4
FEATURE [App::DocumentObjectGroupPython] C_element078  label="C_element : 037"  # scripted group (container) (typed FeaturePython)
  n = 3
  ref = C_element
FEATURE [App::DocumentObjectGroupPython] H_element072  label="H_element : 034"  # scripted group (container) (typed FeaturePython)
  n = 3
  ref = H_element
FEATURE [App::DocumentObjectGroupPython] N_element036  label="N_element : 015"  # scripted group (container) (typed FeaturePython)
  n = 1
  ref = N_element
FEATURE [App::DocumentObjectGroupPython] G4_POLYACRYLONITRILE  # scripted group (container) (typed FeaturePython)
  Dunit = g/cm3
  Dvalue = 1.17
  Group = -> [C_element078,H_element072,N_element036]
  conduct = 2
  density = 1
  expand = 3
  formula = G4_POLYACRYLONITRILE
  name = G4_POLYACRYLONITRILE
  specific = 4
FEATURE [App::DocumentObjectGroupPython] C_element079  label="C_element : 16"  # scripted group (container) (typed FeaturePython)
  n = 16
  ref = C_element
FEATURE [App::DocumentObjectGroupPython] H_element073  label="H_element : 035"  # scripted group (container) (typed FeaturePython)
  n = 14
  ref = H_element
FEATURE [App::DocumentObjectGroupPython] O_element077  label="O_element : 038"  # scripted group (container) (typed FeaturePython)
  n = 3
  ref = O_element
FEATURE [App::DocumentObjectGroupPython] G4_POLYCARBONATE  # scripted group (container) (typed FeaturePython)
  Dunit = g/cm3
  Dvalue = 1.2
  Group = -> [C_element079,H_element073,O_element077]
  conduct = 2
  density = 1
  expand = 3
  formula = G4_POLYCARBONATE
  name = G4_POLYCARBONATE
  specific = 4
FEATURE [App::DocumentObjectGroupPython] C_element080  label="C_element : 038"  # scripted group (container) (typed FeaturePython)
  n = 8
  ref = C_element
FEATURE [App::DocumentObjectGroupPython] H_element074  label="H_element : 036"  # scripted group (container) (typed FeaturePython)
  n = 7
  ref = H_element
FEATURE [App::DocumentObjectGroupPython] Cl_element017  label="Cl_element : 007"  # scripted group (container) (typed FeaturePython)
  n = 1
  ref = Cl_element
FEATURE [App::DocumentObjectGroupPython] G4_POLYCHLOROSTYRENE  # scripted group (container) (typed FeaturePython)
  Dunit = g/cm3
  Dvalue = 1.3
  Group = -> [C_element080,H_element074,Cl_element017]
  conduct = 2
  density = 1
  expand = 3
  formula = G4_POLYCHLOROSTYRENE
  name = G4_POLYCHLOROSTYRENE
  specific = 4
FEATURE [App::DocumentObjectGroupPython] C_element081  label="C_element : 039"  # scripted group (container) (typed FeaturePython)
  n = 1
  ref = C_element
FEATURE [App::DocumentObjectGroupPython] H_element075  label="H_element : 037"  # scripted group (container) (typed FeaturePython)
  n = 2
  ref = H_element
FEATURE [App::DocumentObjectGroupPython] G4_POLYETHYLENE  # scripted group (container) (typed FeaturePython)
  Dunit = g/cm3
  Dvalue = 0.94
  Group = -> [C_element081,H_element075]
  conduct = 2
  density = 1
  expand = 3
  formula = G4_POLYETHYLENE
  name = G4_POLYETHYLENE
  specific = 4
FEATURE [App::DocumentObjectGroupPython] C_element082  label="C_element : 040"  # scripted group (container) (typed FeaturePython)
  n = 10
  ref = C_element
FEATURE [App::DocumentObjectGroupPython] H_element076  label="H_element : 038"  # scripted group (container) (typed FeaturePython)
  n = 8
  ref = H_element
FEATURE [App::DocumentObjectGroupPython] O_element078  label="O_element : 039"  # scripted group (container) (typed FeaturePython)
  n = 4
  ref = O_element
FEATURE [App::DocumentObjectGroupPython] G4_MYLAR  # scripted group (container) (typed FeaturePython)
  Dunit = g/cm3
  Dvalue = 1.4
  Group = -> [C_element082,H_element076,O_element078]
  conduct = 2
  density = 1
  expand = 3
  formula = G4_MYLAR
  name = G4_MYLAR
  specific = 4
FEATURE [App::DocumentObjectGroupPython] C_element083  label="C_element : 041"  # scripted group (container) (typed FeaturePython)
  n = 5
  ref = C_element
FEATURE [App::DocumentObjectGroupPython] H_element077  label="H_element : 039"  # scripted group (container) (typed FeaturePython)
  n = 8
  ref = H_element
FEATURE [App::DocumentObjectGroupPython] O_element079  label="O_element : 040"  # scripted group (container) (typed FeaturePython)
  n = 2
  ref = O_element
FEATURE [App::DocumentObjectGroupPython] G4_PLEXIGLASS  # scripted group (container) (typed FeaturePython)
  Dunit = g/cm3
  Dvalue = 1.19
  Group = -> [C_element083,H_element077,O_element079]
  conduct = 2
  density = 1
  expand = 3
  formula = G4_PLEXIGLASS
  name = G4_PLEXIGLASS
  specific = 4
FEATURE [App::DocumentObjectGroupPython] C_element084  label="C_element : 042"  # scripted group (container) (typed FeaturePython)
  n = 1
  ref = C_element
FEATURE [App::DocumentObjectGroupPython] H_element078  label="H_element : 040"  # scripted group (container) (typed FeaturePython)
  n = 2
  ref = H_element
FEATURE [App::DocumentObjectGroupPython] O_element080  label="O_element : 041"  # scripted group (container) (typed FeaturePython)
  n = 1
  ref = O_element
FEATURE [App::DocumentObjectGroupPython] G4_POLYOXYMETHYLENE  # scripted group (container) (typed FeaturePython)
  Dunit = g/cm3
  Dvalue = 1.425
  Group = -> [C_element084,H_element078,O_element080]
  conduct = 2
  density = 1
  expand = 3
  formula = G4_POLYOXYMETHYLENE
  name = G4_POLYOXYMETHYLENE
  specific = 4
FEATURE [App::DocumentObjectGroupPython] C_element085  label="C_element : 043"  # scripted group (container) (typed FeaturePython)
  n = 2
  ref = C_element
FEATURE [App::DocumentObjectGroupPython] H_element079  label="H_element : 041"  # scripted group (container) (typed FeaturePython)
  n = 4
  ref = H_element
FEATURE [App::DocumentObjectGroupPython] G4_POLYPROPYLENE  # scripted group (container) (typed FeaturePython)
  Dunit = g/cm3
  Dvalue = 0.9
  Group = -> [C_element085,H_element079]
  conduct = 2
  density = 1
  expand = 3
  formula = G4_POLYPROPYLENE
  name = G4_POLYPROPYLENE
  specific = 4
FEATURE [App::DocumentObjectGroupPython] C_element086  label="C_element : 044"  # scripted group (container) (typed FeaturePython)
  n = 8
  ref = C_element
FEATURE [App::DocumentObjectGroupPython] H_element080  label="H_element : 042"  # scripted group (container) (typed FeaturePython)
  n = 8
  ref = H_element
FEATURE [App::DocumentObjectGroupPython] G4_POLYSTYRENE  # scripted group (container) (typed FeaturePython)
  Dunit = g/cm3
  Dvalue = 1.06
  Group = -> [C_element086,H_element080]
  conduct = 2
  density = 1
  expand = 3
  formula = G4_POLYSTYRENE
  name = G4_POLYSTYRENE
  specific = 4
FEATURE [App::DocumentObjectGroupPython] C_element087  label="C_element : 045"  # scripted group (container) (typed FeaturePython)
  n = 2
  ref = C_element
FEATURE [App::DocumentObjectGroupPython] F_element014  label="F_element : 4"  # scripted group (container) (typed FeaturePython)
  n = 4
  ref = F_element
FEATURE [App::DocumentObjectGroupPython] G4_TEFLON  # scripted group (container) (typed FeaturePython)
  Dunit = g/cm3
  Dvalue = 2.2
  Group = -> [C_element087,F_element014]
  conduct = 2
  density = 1
  expand = 3
  formula = G4_TEFLON
  name = G4_TEFLON
  specific = 4
FEATURE [App::DocumentObjectGroupPython] C_element088  label="C_element : 046"  # scripted group (container) (typed FeaturePython)
  n = 2
  ref = C_element
FEATURE [App::DocumentObjectGroupPython] F_element015  label="F_element : 006"  # scripted group (container) (typed FeaturePython)
  n = 3
  ref = F_element
FEATURE [App::DocumentObjectGroupPython] Cl_element018  label="Cl_element : 008"  # scripted group (container) (typed FeaturePython)
  n = 1
  ref = Cl_element
FEATURE [App::DocumentObjectGroupPython] G4_POLYTRIFLUOROCHLOROETHYLENE  # scripted group (container) (typed FeaturePython)
  Dunit = g/cm3
  Dvalue = 2.1
  Group = -> [C_element088,F_element015,Cl_element018]
  conduct = 2
  density = 1
  expand = 3
  formula = G4_POLYTRIFLUOROCHLOROETHYLENE
  name = G4_POLYTRIFLUOROCHLOROETHYLENE
  specific = 4
FEATURE [App::DocumentObjectGroupPython] C_element089  label="C_element : 047"  # scripted group (container) (typed FeaturePython)
  n = 4
  ref = C_element
FEATURE [App::DocumentObjectGroupPython] H_element081  label="H_element : 043"  # scripted group (container) (typed FeaturePython)
  n = 6
  ref = H_element
FEATURE [App::DocumentObjectGroupPython] O_element081  label="O_element : 042"  # scripted group (container) (typed FeaturePython)
  n = 2
  ref = O_element
FEATURE [App::DocumentObjectGroupPython] G4_POLYVINYL_ACETATE  # scripted group (container) (typed FeaturePython)
  Dunit = g/cm3
  Dvalue = 1.19
  Group = -> [C_element089,H_element081,O_element081]
  conduct = 2
  density = 1
  expand = 3
  formula = G4_POLYVINYL_ACETATE
  name = G4_POLYVINYL_ACETATE
  specific = 4
FEATURE [App::DocumentObjectGroupPython] C_element090  label="C_element : 048"  # scripted group (container) (typed FeaturePython)
  n = 2
  ref = C_element
FEATURE [App::DocumentObjectGroupPython] H_element082  label="H_element : 044"  # scripted group (container) (typed FeaturePython)
  n = 4
  ref = H_element
FEATURE [App::DocumentObjectGroupPython] O_element082  label="O_element : 043"  # scripted group (container) (typed FeaturePython)
  n = 1
  ref = O_element
FEATURE [App::DocumentObjectGroupPython] G4_POLYVINYL_ALCOHOL  # scripted group (container) (typed FeaturePython)
  Dunit = g/cm3
  Dvalue = 1.3
  Group = -> [C_element090,H_element082,O_element082]
  conduct = 2
  density = 1
  expand = 3
  formula = G4_POLYVINYL_ALCOHOL
  name = G4_POLYVINYL_ALCOHOL
  specific = 4
FEATURE [App::DocumentObjectGroupPython] C_element091  label="C_element : 049"  # scripted group (container) (typed FeaturePython)
  n = 8
  ref = C_element
FEATURE [App::DocumentObjectGroupPython] H_element083  label="H_element : 045"  # scripted group (container) (typed FeaturePython)
  n = 14
  ref = H_element
FEATURE [App::DocumentObjectGroupPython] O_element083  label="O_element : 044"  # scripted group (container) (typed FeaturePython)
  n = 2
  ref = O_element
FEATURE [App::DocumentObjectGroupPython] G4_POLYVINYL_BUTYRAL  # scripted group (container) (typed FeaturePython)
  Dunit = g/cm3
  Dvalue = 1.12
  Group = -> [C_element091,H_element083,O_element083]
  conduct = 2
  density = 1
  expand = 3
  formula = G4_POLYVINYL_BUTYRAL
  name = G4_POLYVINYL_BUTYRAL
  specific = 4
FEATURE [App::DocumentObjectGroupPython] C_element092  label="C_element : 050"  # scripted group (container) (typed FeaturePython)
  n = 2
  ref = C_element
FEATURE [App::DocumentObjectGroupPython] H_element084  label="H_element : 046"  # scripted group (container) (typed FeaturePython)
  n = 3
  ref = H_element
FEATURE [App::DocumentObjectGroupPython] Cl_element019  label="Cl_element : 009"  # scripted group (container) (typed FeaturePython)
  n = 1
  ref = Cl_element
FEATURE [App::DocumentObjectGroupPython] G4_POLYVINYL_CHLORIDE  # scripted group (container) (typed FeaturePython)
  Dunit = g/cm3
  Dvalue = 1.3
  Group = -> [C_element092,H_element084,Cl_element019]
  conduct = 2
  density = 1
  expand = 3
  formula = G4_POLYVINYL_CHLORIDE
  name = G4_POLYVINYL_CHLORIDE
  specific = 4
FEATURE [App::DocumentObjectGroupPython] C_element093  label="C_element : 051"  # scripted group (container) (typed FeaturePython)
  n = 2
  ref = C_element
FEATURE [App::DocumentObjectGroupPython] H_element085  label="H_element : 047"  # scripted group (container) (typed FeaturePython)
  n = 2
  ref = H_element
FEATURE [App::DocumentObjectGroupPython] Cl_element020  label="Cl_element : 010"  # scripted group (container) (typed FeaturePython)
  n = 2
  ref = Cl_element
FEATURE [App::DocumentObjectGroupPython] G4_POLYVINYLIDENE_CHLORIDE  # scripted group (container) (typed FeaturePython)
  Dunit = g/cm3
  Dvalue = 1.7
  Group = -> [C_element093,H_element085,Cl_element020]
  conduct = 2
  density = 1
  expand = 3
  formula = G4_POLYVINYLIDENE_CHLORIDE
  name = G4_POLYVINYLIDENE_CHLORIDE
  specific = 4
FEATURE [App::DocumentObjectGroupPython] C_element094  label="C_element : 052"  # scripted group (container) (typed FeaturePython)
  n = 2
  ref = C_element
FEATURE [App::DocumentObjectGroupPython] H_element086  label="H_element : 048"  # scripted group (container) (typed FeaturePython)
  n = 2
  ref = H_element
FEATURE [App::DocumentObjectGroupPython] F_element016  label="F_element : 007"  # scripted group (container) (typed FeaturePython)
  n = 2
  ref = F_element
FEATURE [App::DocumentObjectGroupPython] G4_POLYVINYLIDENE_FLUORIDE  # scripted group (container) (typed FeaturePython)
  Dunit = g/cm3
  Dvalue = 1.76
  Group = -> [C_element094,H_element086,F_element016]
  conduct = 2
  density = 1
  expand = 3
  formula = G4_POLYVINYLIDENE_FLUORIDE
  name = G4_POLYVINYLIDENE_FLUORIDE
  specific = 4
FEATURE [App::DocumentObjectGroupPython] C_element095  label="C_element : 053"  # scripted group (container) (typed FeaturePython)
  n = 6
  ref = C_element
FEATURE [App::DocumentObjectGroupPython] H_element087  label="H_element : 9"  # scripted group (container) (typed FeaturePython)
  n = 9
  ref = H_element
FEATURE [App::DocumentObjectGroupPython] N_element037  label="N_element : 016"  # scripted group (container) (typed FeaturePython)
  n = 1
  ref = N_element
FEATURE [App::DocumentObjectGroupPython] O_element084  label="O_element : 045"  # scripted group (container) (typed FeaturePython)
  n = 1
  ref = O_element
FEATURE [App::DocumentObjectGroupPython] G4_POLYVINYL_PYRROLIDONE  # scripted group (container) (typed FeaturePython)
  Dunit = g/cm3
  Dvalue = 1.25
  Group = -> [C_element095,H_element087,N_element037,O_element084]
  conduct = 2
  density = 1
  expand = 3
  formula = G4_POLYVINYL_PYRROLIDONE
  name = G4_POLYVINYL_PYRROLIDONE
  specific = 4
FEATURE [App::DocumentObjectGroupPython] K_element008  label="K_element : 1"  # scripted group (container) (typed FeaturePython)
  n = 1
  ref = K_element
FEATURE [App::DocumentObjectGroupPython] I_element006  label="I_element : 003"  # scripted group (container) (typed FeaturePython)
  n = 1
  ref = I_element
FEATURE [App::DocumentObjectGroupPython] G4_POTASSIUM_IODIDE  # scripted group (container) (typed FeaturePython)
  Dunit = g/cm3
  Dvalue = 3.13
  Group = -> [K_element008,I_element006]
  conduct = 2
  density = 1
  expand = 3
  formula = G4_POTASSIUM_IODIDE
  name = G4_POTASSIUM_IODIDE
  specific = 4
FEATURE [App::DocumentObjectGroupPython] K_element009  label="K_element : 2"  # scripted group (container) (typed FeaturePython)
  n = 2
  ref = K_element
FEATURE [App::DocumentObjectGroupPython] O_element085  label="O_element : 046"  # scripted group (container) (typed FeaturePython)
  n = 1
  ref = O_element
FEATURE [App::DocumentObjectGroupPython] G4_POTASSIUM_OXIDE  # scripted group (container) (typed FeaturePython)
  Dunit = g/cm3
  Dvalue = 2.32
  Group = -> [K_element009,O_element085]
  conduct = 2
  density = 1
  expand = 3
  formula = G4_POTASSIUM_OXIDE
  name = G4_POTASSIUM_OXIDE
  specific = 4
FEATURE [App::DocumentObjectGroupPython] C_element096  label="C_element : 054"  # scripted group (container) (typed FeaturePython)
  n = 3
  ref = C_element
FEATURE [App::DocumentObjectGroupPython] H_element088  label="H_element : 049"  # scripted group (container) (typed FeaturePython)
  n = 8
  ref = H_element
FEATURE [App::DocumentObjectGroupPython] G4_PROPANE  # scripted group (container) (typed FeaturePython)
  Dunit = g/cm3
  Dvalue = 0.00187939
  Group = -> [C_element096,H_element088]
  conduct = 2
  density = 1
  expand = 3
  formula = G4_PROPANE
  name = G4_PROPANE
  specific = 4
FEATURE [App::DocumentObjectGroupPython] C_element097  label="C_element : 055"  # scripted group (container) (typed FeaturePython)
  n = 3
  ref = C_element
FEATURE [App::DocumentObjectGroupPython] H_element089  label="H_element : 050"  # scripted group (container) (typed FeaturePython)
  n = 8
  ref = H_element
FEATURE [App::DocumentObjectGroupPython] G4_lPROPANE  # scripted group (container) (typed FeaturePython)
  Dunit = g/cm3
  Dvalue = 0.43
  Group = -> [C_element097,H_element089]
  conduct = 2
  density = 1
  expand = 3
  formula = G4_lPROPANE
  name = G4_lPROPANE
  specific = 4
FEATURE [App::DocumentObjectGroupPython] C_element098  label="C_element : 056"  # scripted group (container) (typed FeaturePython)
  n = 3
  ref = C_element
FEATURE [App::DocumentObjectGroupPython] H_element090  label="H_element : 051"  # scripted group (container) (typed FeaturePython)
  n = 8
  ref = H_element
FEATURE [App::DocumentObjectGroupPython] O_element086  label="O_element : 047"  # scripted group (container) (typed FeaturePython)
  n = 1
  ref = O_element
FEATURE [App::DocumentObjectGroupPython] G4_N_PROPYL_ALCOHOL  label="G4_N-PROPYL_ALCOHOL"  # scripted group (container) (typed FeaturePython)
  Dunit = g/cm3
  Dvalue = 0.8035
  Group = -> [C_element098,H_element090,O_element086]
  conduct = 2
  density = 1
  expand = 3
  formula = G4_N-PROPYL_ALCOHOL
  name = G4_N-PROPYL_ALCOHOL
  specific = 4
FEATURE [App::DocumentObjectGroupPython] C_element099  label="C_element : 057"  # scripted group (container) (typed FeaturePython)
  n = 5
  ref = C_element
FEATURE [App::DocumentObjectGroupPython] H_element091  label="H_element : 052"  # scripted group (container) (typed FeaturePython)
  n = 5
  ref = H_element
FEATURE [App::DocumentObjectGroupPython] N_element038  label="N_element : 017"  # scripted group (container) (typed FeaturePython)
  n = 1
  ref = N_element
FEATURE [App::DocumentObjectGroupPython] G4_PYRIDINE  # scripted group (container) (typed FeaturePython)
  Dunit = g/cm3
  Dvalue = 0.9819
  Group = -> [C_element099,H_element091,N_element038]
  conduct = 2
  density = 1
  expand = 3
  formula = G4_PYRIDINE
  name = G4_PYRIDINE
  specific = 4
FEATURE [App::DocumentObjectGroupPython] H_element092  label="H_element : 0.144"  # scripted group (container) (typed FeaturePython)
  n = 0.143711
FEATURE [App::DocumentObjectGroupPython] C_element100  label="C_element : 0.856"  # scripted group (container) (typed FeaturePython)
  n = 0.856289
FEATURE [App::DocumentObjectGroupPython] G4_RUBBER_BUTYL  # scripted group (container) (typed FeaturePython)
  Dunit = g/cm3
  Dvalue = 0.92
  Group = -> [H_element092,C_element100]
  conduct = 2
  density = 1
  expand = 3
  formula = G4_RUBBER_BUTYL
  name = G4_RUBBER_BUTYL
  specific = 4
FEATURE [App::DocumentObjectGroupPython] H_element093  label="H_element : 0.118"  # scripted group (container) (typed FeaturePython)
  n = 0.118371
FEATURE [App::DocumentObjectGroupPython] C_element101  label="C_element : 0.882"  # scripted group (container) (typed FeaturePython)
  n = 0.881629
FEATURE [App::DocumentObjectGroupPython] G4_RUBBER_NATURAL  # scripted group (container) (typed FeaturePython)
  Dunit = g/cm3
  Dvalue = 0.92
  Group = -> [H_element093,C_element101]
  conduct = 2
  density = 1
  expand = 3
  formula = G4_RUBBER_NATURAL
  name = G4_RUBBER_NATURAL
  specific = 4
FEATURE [App::DocumentObjectGroupPython] H_element094  label="H_element : 0.145"  # scripted group (container) (typed FeaturePython)
  n = 0.05692
FEATURE [App::DocumentObjectGroupPython] C_element102  label="C_element : 0.543"  # scripted group (container) (typed FeaturePython)
  n = 0.542646
FEATURE [App::DocumentObjectGroupPython] Cl_element021  label="Cl_element : 0.400"  # scripted group (container) (typed FeaturePython)
  n = 0.400434
FEATURE [App::DocumentObjectGroupPython] G4_RUBBER_NEOPRENE  # scripted group (container) (typed FeaturePython)
  Dunit = g/cm3
  Dvalue = 1.23
  Group = -> [H_element094,C_element102,Cl_element021]
  conduct = 2
  density = 1
  expand = 3
  formula = G4_RUBBER_NEOPRENE
  name = G4_RUBBER_NEOPRENE
  specific = 4
FEATURE [App::DocumentObjectGroupPython] Si_element006  label="Si_element : 1"  # scripted group (container) (typed FeaturePython)
  n = 1
  ref = Si_element
FEATURE [App::DocumentObjectGroupPython] O_element087  label="O_element : 048"  # scripted group (container) (typed FeaturePython)
  n = 2
  ref = O_element
FEATURE [App::DocumentObjectGroupPython] G4_SILICON_DIOXIDE  # scripted group (container) (typed FeaturePython)
  Dunit = g/cm3
  Dvalue = 2.32
  Group = -> [Si_element006,O_element087]
  conduct = 2
  density = 1
  expand = 3
  formula = G4_SILICON_DIOXIDE
  name = G4_SILICON_DIOXIDE
  specific = 4
FEATURE [App::DocumentObjectGroupPython] Ag_element002  label="Ag_element : 1"  # scripted group (container) (typed FeaturePython)
  n = 1
  ref = Ag_element
FEATURE [App::DocumentObjectGroupPython] Br_element005  label="Br_element : 003"  # scripted group (container) (typed FeaturePython)
  n = 1
  ref = Br_element
FEATURE [App::DocumentObjectGroupPython] G4_SILVER_BROMIDE  # scripted group (container) (typed FeaturePython)
  Dunit = g/cm3
  Dvalue = 6.473
  Group = -> [Ag_element002,Br_element005]
  conduct = 2
  density = 1
  expand = 3
  formula = G4_SILVER_BROMIDE
  name = G4_SILVER_BROMIDE
  specific = 4
FEATURE [App::DocumentObjectGroupPython] Ag_element003  label="Ag_element : 002"  # scripted group (container) (typed FeaturePython)
  n = 1
  ref = Ag_element
FEATURE [App::DocumentObjectGroupPython] Cl_element022  label="Cl_element : 011"  # scripted group (container) (typed FeaturePython)
  n = 1
  ref = Cl_element
FEATURE [App::DocumentObjectGroupPython] G4_SILVER_CHLORIDE  # scripted group (container) (typed FeaturePython)
  Dunit = g/cm3
  Dvalue = 5.56
  Group = -> [Ag_element003,Cl_element022]
  conduct = 2
  density = 1
  expand = 3
  formula = G4_SILVER_CHLORIDE
  name = G4_SILVER_CHLORIDE
  specific = 4
FEATURE [App::DocumentObjectGroupPython] Br_element006  label="Br_element : 0.423"  # scripted group (container) (typed FeaturePython)
  n = 0.422895
FEATURE [App::DocumentObjectGroupPython] Ag_element004  label="Ag_element : 0.574"  # scripted group (container) (typed FeaturePython)
  n = 0.573748
FEATURE [App::DocumentObjectGroupPython] I_element007  label="I_element : 0.649"  # scripted group (container) (typed FeaturePython)
  n = 0.003357
FEATURE [App::DocumentObjectGroupPython] G4_SILVER_HALIDES  # scripted group (container) (typed FeaturePython)
  Dunit = g/cm3
  Dvalue = 6.47
  Group = -> [Br_element006,Ag_element004,I_element007]
  conduct = 2
  density = 1
  expand = 3
  formula = G4_SILVER_HALIDES
  name = G4_SILVER_HALIDES
  specific = 4
FEATURE [App::DocumentObjectGroupPython] Ag_element005  label="Ag_element : 003"  # scripted group (container) (typed FeaturePython)
  n = 1
  ref = Ag_element
FEATURE [App::DocumentObjectGroupPython] I_element008  label="I_element : 004"  # scripted group (container) (typed FeaturePython)
  n = 1
  ref = I_element
FEATURE [App::DocumentObjectGroupPython] G4_SILVER_IODIDE  # scripted group (container) (typed FeaturePython)
  Dunit = g/cm3
  Dvalue = 6.01
  Group = -> [Ag_element005,I_element008]
  conduct = 2
  density = 1
  expand = 3
  formula = G4_SILVER_IODIDE
  name = G4_SILVER_IODIDE
  specific = 4
FEATURE [App::DocumentObjectGroupPython] H_element095  label="H_element : 0.100"  # scripted group (container) (typed FeaturePython)
  n = 0.1
FEATURE [App::DocumentObjectGroupPython] C_element103  label="C_element : 0.204"  # scripted group (container) (typed FeaturePython)
  n = 0.204
FEATURE [App::DocumentObjectGroupPython] N_element039  label="N_element : 0.759"  # scripted group (container) (typed FeaturePython)
  n = 0.042
FEATURE [App::DocumentObjectGroupPython] O_element088  label="O_element : 0.645"  # scripted group (container) (typed FeaturePython)
  n = 0.645
FEATURE [App::DocumentObjectGroupPython] Na_element013  label="Na_element : 0.100"  # scripted group (container) (typed FeaturePython)
  n = 0.002
FEATURE [App::DocumentObjectGroupPython] P_element009  label="P_element : 0.107"  # scripted group (container) (typed FeaturePython)
  n = 0.001
FEATURE [App::DocumentObjectGroupPython] S_element020  label="S_element : 0.021"  # scripted group (container) (typed FeaturePython)
  n = 0.002
FEATURE [App::DocumentObjectGroupPython] Cl_element023  label="Cl_element : 0.590"  # scripted group (container) (typed FeaturePython)
  n = 0.003
FEATURE [App::DocumentObjectGroupPython] K_element010  label="K_element : 0.001"  # scripted group (container) (typed FeaturePython)
  n = 0.001
FEATURE [App::DocumentObjectGroupPython] G4_SKIN_ICRP  # scripted group (container) (typed FeaturePython)
  Dunit = g/cm3
  Dvalue = 1.09
  Group = -> [H_element095,C_element103,N_element039,O_element088,Na_element013,P_element009,S_element020,Cl_element023,K_element010]
  conduct = 2
  density = 1
  expand = 3
  formula = G4_SKIN_ICRP
  name = G4_SKIN_ICRP
  specific = 4
FEATURE [App::DocumentObjectGroupPython] Na_element014  label="Na_element : 2"  # scripted group (container) (typed FeaturePython)
  n = 2
  ref = Na_element
FEATURE [App::DocumentObjectGroupPython] C_element104  label="C_element : 058"  # scripted group (container) (typed FeaturePython)
  n = 1
  ref = C_element
FEATURE [App::DocumentObjectGroupPython] O_element089  label="O_element : 049"  # scripted group (container) (typed FeaturePython)
  n = 3
  ref = O_element
FEATURE [App::DocumentObjectGroupPython] G4_SODIUM_CARBONATE  # scripted group (container) (typed FeaturePython)
  Dunit = g/cm3
  Dvalue = 2.532
  Group = -> [Na_element014,C_element104,O_element089]
  conduct = 2
  density = 1
  expand = 3
  formula = G4_SODIUM_CARBONATE
  name = G4_SODIUM_CARBONATE
  specific = 4
FEATURE [App::DocumentObjectGroupPython] Na_element015  label="Na_element : 1"  # scripted group (container) (typed FeaturePython)
  n = 1
  ref = Na_element
FEATURE [App::DocumentObjectGroupPython] I_element009  label="I_element : 005"  # scripted group (container) (typed FeaturePython)
  n = 1
  ref = I_element
FEATURE [App::DocumentObjectGroupPython] G4_SODIUM_IODIDE  # scripted group (container) (typed FeaturePython)
  Dunit = g/cm3
  Dvalue = 3.667
  Group = -> [Na_element015,I_element009]
  conduct = 2
  density = 1
  expand = 3
  formula = G4_SODIUM_IODIDE
  name = G4_SODIUM_IODIDE
  specific = 4
FEATURE [App::DocumentObjectGroupPython] Na_element016  label="Na_element : 003"  # scripted group (container) (typed FeaturePython)
  n = 2
  ref = Na_element
FEATURE [App::DocumentObjectGroupPython] O_element090  label="O_element : 050"  # scripted group (container) (typed FeaturePython)
  n = 1
  ref = O_element
FEATURE [App::DocumentObjectGroupPython] G4_SODIUM_MONOXIDE  # scripted group (container) (typed FeaturePython)
  Dunit = g/cm3
  Dvalue = 2.27
  Group = -> [Na_element016,O_element090]
  conduct = 2
  density = 1
  expand = 3
  formula = G4_SODIUM_MONOXIDE
  name = G4_SODIUM_MONOXIDE
  specific = 4
FEATURE [App::DocumentObjectGroupPython] Na_element017  label="Na_element : 004"  # scripted group (container) (typed FeaturePython)
  n = 1
  ref = Na_element
FEATURE [App::DocumentObjectGroupPython] N_element040  label="N_element : 018"  # scripted group (container) (typed FeaturePython)
  n = 1
  ref = N_element
FEATURE [App::DocumentObjectGroupPython] O_element091  label="O_element : 051"  # scripted group (container) (typed FeaturePython)
  n = 3
  ref = O_element
FEATURE [App::DocumentObjectGroupPython] G4_SODIUM_NITRATE  # scripted group (container) (typed FeaturePython)
  Dunit = g/cm3
  Dvalue = 2.261
  Group = -> [Na_element017,N_element040,O_element091]
  conduct = 2
  density = 1
  expand = 3
  formula = G4_SODIUM_NITRATE
  name = G4_SODIUM_NITRATE
  specific = 4
FEATURE [App::DocumentObjectGroupPython] C_element105  label="C_element : 059"  # scripted group (container) (typed FeaturePython)
  n = 14
  ref = C_element
FEATURE [App::DocumentObjectGroupPython] H_element096  label="H_element : 053"  # scripted group (container) (typed FeaturePython)
  n = 12
  ref = H_element
FEATURE [App::DocumentObjectGroupPython] G4_STILBENE  # scripted group (container) (typed FeaturePython)
  Dunit = g/cm3
  Dvalue = 0.9707
  Group = -> [C_element105,H_element096]
  conduct = 2
  density = 1
  expand = 3
  formula = G4_STILBENE
  name = G4_STILBENE
  specific = 4
FEATURE [App::DocumentObjectGroupPython] C_element106  label="C_element : 12"  # scripted group (container) (typed FeaturePython)
  n = 12
  ref = C_element
FEATURE [App::DocumentObjectGroupPython] H_element097  label="H_element : 22"  # scripted group (container) (typed FeaturePython)
  n = 22
  ref = H_element
FEATURE [App::DocumentObjectGroupPython] O_element092  label="O_element : 11"  # scripted group (container) (typed FeaturePython)
  n = 11
  ref = O_element
FEATURE [App::DocumentObjectGroupPython] G4_SUCROSE  # scripted group (container) (typed FeaturePython)
  Dunit = g/cm3
  Dvalue = 1.5805
  Group = -> [C_element106,H_element097,O_element092]
  conduct = 2
  density = 1
  expand = 3
  formula = G4_SUCROSE
  name = G4_SUCROSE
  specific = 4
FEATURE [App::DocumentObjectGroupPython] C_element107  label="C_element : 18"  # scripted group (container) (typed FeaturePython)
  n = 18
  ref = C_element
FEATURE [App::DocumentObjectGroupPython] H_element098  label="H_element : 054"  # scripted group (container) (typed FeaturePython)
  n = 14
  ref = H_element
FEATURE [App::DocumentObjectGroupPython] G4_TERPHENYL  # scripted group (container) (typed FeaturePython)
  Dunit = g/cm3
  Dvalue = 1.24
  Group = -> [C_element107,H_element098]
  conduct = 2
  density = 1
  expand = 3
  formula = G4_TERPHENYL
  name = G4_TERPHENYL
  specific = 4
FEATURE [App::DocumentObjectGroupPython] H_element099  label="H_element : 0.146"  # scripted group (container) (typed FeaturePython)
  n = 0.106
FEATURE [App::DocumentObjectGroupPython] C_element108  label="C_element : 0.883"  # scripted group (container) (typed FeaturePython)
  n = 0.099
FEATURE [App::DocumentObjectGroupPython] N_element041  label="N_element : 0.020"  # scripted group (container) (typed FeaturePython)
  n = 0.02
FEATURE [App::DocumentObjectGroupPython] O_element093  label="O_element : 0.766"  # scripted group (container) (typed FeaturePython)
  n = 0.766
FEATURE [App::DocumentObjectGroupPython] Na_element018  label="Na_element : 0.101"  # scripted group (container) (typed FeaturePython)
  n = 0.002
FEATURE [App::DocumentObjectGroupPython] P_element010  label="P_element : 0.108"  # scripted group (container) (typed FeaturePython)
  n = 0.001
FEATURE [App::DocumentObjectGroupPython] S_element021  label="S_element : 0.022"  # scripted group (container) (typed FeaturePython)
  n = 0.002
FEATURE [App::DocumentObjectGroupPython] Cl_element024  label="Cl_element : 0.002"  # scripted group (container) (typed FeaturePython)
  n = 0.002
FEATURE [App::DocumentObjectGroupPython] K_element011  label="K_element : 0.017"  # scripted group (container) (typed FeaturePython)
  n = 0.002
FEATURE [App::DocumentObjectGroupPython] G4_TESTIS_ICRP  # scripted group (container) (typed FeaturePython)
  Dunit = g/cm3
  Dvalue = 1.04
  Group = -> [H_element099,C_element108,N_element041,O_element093,Na_element018,P_element010,S_element021,Cl_element024,K_element011]
  conduct = 2
  density = 1
  expand = 3
  formula = G4_TESTIS_ICRP
  name = G4_TESTIS_ICRP
  specific = 4
FEATURE [App::DocumentObjectGroupPython] C_element109  label="C_element : 060"  # scripted group (container) (typed FeaturePython)
  n = 2
  ref = C_element
FEATURE [App::DocumentObjectGroupPython] Cl_element025  label="Cl_element : 012"  # scripted group (container) (typed FeaturePython)
  n = 4
  ref = Cl_element
FEATURE [App::DocumentObjectGroupPython] G4_TETRACHLOROETHYLENE  # scripted group (container) (typed FeaturePython)
  Dunit = g/cm3
  Dvalue = 1.625
  Group = -> [C_element109,Cl_element025]
  conduct = 2
  density = 1
  expand = 3
  formula = G4_TETRACHLOROETHYLENE
  name = G4_TETRACHLOROETHYLENE
  specific = 4
FEATURE [App::DocumentObjectGroupPython] Tl_element001  label="Tl_element : 1"  # scripted group (container) (typed FeaturePython)
  n = 1
  ref = Tl_element
FEATURE [App::DocumentObjectGroupPython] Cl_element026  label="Cl_element : 013"  # scripted group (container) (typed FeaturePython)
  n = 1
  ref = Cl_element
FEATURE [App::DocumentObjectGroupPython] G4_THALLIUM_CHLORIDE  # scripted group (container) (typed FeaturePython)
  Dunit = g/cm3
  Dvalue = 7.004
  Group = -> [Tl_element001,Cl_element026]
  conduct = 2
  density = 1
  expand = 3
  formula = G4_THALLIUM_CHLORIDE
  name = G4_THALLIUM_CHLORIDE
  specific = 4
FEATURE [App::DocumentObjectGroupPython] H_element100  label="H_element : 0.147"  # scripted group (container) (typed FeaturePython)
  n = 0.105
FEATURE [App::DocumentObjectGroupPython] C_element110  label="C_element : 0.256"  # scripted group (container) (typed FeaturePython)
  n = 0.256
FEATURE [App::DocumentObjectGroupPython] N_element042  label="N_element : 0.760"  # scripted group (container) (typed FeaturePython)
  n = 0.027
FEATURE [App::DocumentObjectGroupPython] O_element094  label="O_element : 0.602"  # scripted group (container) (typed FeaturePython)
  n = 0.602
FEATURE [App::DocumentObjectGroupPython] Na_element019  label="Na_element : 0.102"  # scripted group (container) (typed FeaturePython)
  n = 0.001
FEATURE [App::DocumentObjectGroupPython] P_element011  label="P_element : 0.109"  # scripted group (container) (typed FeaturePython)
  n = 0.002
FEATURE [App::DocumentObjectGroupPython] S_element022  label="S_element : 0.023"  # scripted group (container) (typed FeaturePython)
  n = 0.003
FEATURE [App::DocumentObjectGroupPython] Cl_element027  label="Cl_element : 0.591"  # scripted group (container) (typed FeaturePython)
  n = 0.002
FEATURE [App::DocumentObjectGroupPython] K_element012  label="K_element : 0.018"  # scripted group (container) (typed FeaturePython)
  n = 0.002
FEATURE [App::DocumentObjectGroupPython] G4_TISSUE_SOFT_ICRP  # scripted group (container) (typed FeaturePython)
  Dunit = g/cm3
  Dvalue = 1.03
  Group = -> [H_element100,C_element110,N_element042,O_element094,Na_element019,P_element011,S_element022,Cl_element027,K_element012]
  conduct = 2
  density = 1
  expand = 3
  formula = G4_TISSUE_SOFT_ICRP
  name = G4_TISSUE_SOFT_ICRP
  specific = 4
FEATURE [App::DocumentObjectGroupPython] H_element101  label="H_element : 0.148"  # scripted group (container) (typed FeaturePython)
  n = 0.101
FEATURE [App::DocumentObjectGroupPython] C_element111  label="C_element : 0.111"  # scripted group (container) (typed FeaturePython)
  n = 0.111
FEATURE [App::DocumentObjectGroupPython] N_element043  label="N_element : 0.026"  # scripted group (container) (typed FeaturePython)
  n = 0.026
FEATURE [App::DocumentObjectGroupPython] O_element095  label="O_element : 0.762"  # scripted group (container) (typed FeaturePython)
  n = 0.762
FEATURE [App::DocumentObjectGroupPython] G4_TISSUE_SOFT_ICRU_4  label="G4_TISSUE_SOFT_ICRU-4"  # scripted group (container) (typed FeaturePython)
  Dunit = g/cm3
  Dvalue = 1
  Group = -> [H_element101,C_element111,N_element043,O_element095]
  conduct = 2
  density = 1
  expand = 3
  formula = G4_TISSUE_SOFT_ICRU-4
  name = G4_TISSUE_SOFT_ICRU-4
  specific = 4
FEATURE [App::DocumentObjectGroupPython] H_element102  label="H_element : 0.149"  # scripted group (container) (typed FeaturePython)
  n = 0.101869
FEATURE [App::DocumentObjectGroupPython] C_element112  label="C_element : 0.456"  # scripted group (container) (typed FeaturePython)
  n = 0.456179
FEATURE [App::DocumentObjectGroupPython] N_element044  label="N_element : 0.761"  # scripted group (container) (typed FeaturePython)
  n = 0.035172
FEATURE [App::DocumentObjectGroupPython] O_element096  label="O_element : 0.407"  # scripted group (container) (typed FeaturePython)
  n = 0.40678
FEATURE [App::DocumentObjectGroupPython] G4_TISSUE_METHANE  label="G4_TISSUE-METHANE"  # scripted group (container) (typed FeaturePython)
  Dunit = g/cm3
  Dvalue = 0.00106409
  Group = -> [H_element102,C_element112,N_element044,O_element096]
  conduct = 2
  density = 1
  expand = 3
  formula = G4_TISSUE-METHANE
  name = G4_TISSUE-METHANE
  specific = 4
FEATURE [App::DocumentObjectGroupPython] H_element103  label="H_element : 0.103"  # scripted group (container) (typed FeaturePython)
  n = 0.102672
FEATURE [App::DocumentObjectGroupPython] C_element113  label="C_element : 0.569"  # scripted group (container) (typed FeaturePython)
  n = 0.56894
FEATURE [App::DocumentObjectGroupPython] N_element045  label="N_element : 0.762"  # scripted group (container) (typed FeaturePython)
  n = 0.035022
FEATURE [App::DocumentObjectGroupPython] O_element097  label="O_element : 0.293"  # scripted group (container) (typed FeaturePython)
  n = 0.293366
FEATURE [App::DocumentObjectGroupPython] G4_TISSUE_PROPANE  label="G4_TISSUE-PROPANE"  # scripted group (container) (typed FeaturePython)
  Dunit = g/cm3
  Dvalue = 0.00182628
  Group = -> [H_element103,C_element113,N_element045,O_element097]
  conduct = 2
  density = 1
  expand = 3
  formula = G4_TISSUE-PROPANE
  name = G4_TISSUE-PROPANE
  specific = 4
FEATURE [App::DocumentObjectGroupPython] Ti_element003  label="Ti_element : 1"  # scripted group (container) (typed FeaturePython)
  n = 1
  ref = Ti_element
FEATURE [App::DocumentObjectGroupPython] O_element098  label="O_element : 052"  # scripted group (container) (typed FeaturePython)
  n = 2
  ref = O_element
FEATURE [App::DocumentObjectGroupPython] G4_TITANIUM_DIOXIDE  # scripted group (container) (typed FeaturePython)
  Dunit = g/cm3
  Dvalue = 4.26
  Group = -> [Ti_element003,O_element098]
  conduct = 2
  density = 1
  expand = 3
  formula = G4_TITANIUM_DIOXIDE
  name = G4_TITANIUM_DIOXIDE
  specific = 4
FEATURE [App::DocumentObjectGroupPython] C_element114  label="C_element : 061"  # scripted group (container) (typed FeaturePython)
  n = 7
  ref = C_element
FEATURE [App::DocumentObjectGroupPython] H_element104  label="H_element : 055"  # scripted group (container) (typed FeaturePython)
  n = 8
  ref = H_element
FEATURE [App::DocumentObjectGroupPython] G4_TOLUENE  # scripted group (container) (typed FeaturePython)
  Dunit = g/cm3
  Dvalue = 0.8669
  Group = -> [C_element114,H_element104]
  conduct = 2
  density = 1
  expand = 3
  formula = G4_TOLUENE
  name = G4_TOLUENE
  specific = 4
FEATURE [App::DocumentObjectGroupPython] C_element115  label="C_element : 062"  # scripted group (container) (typed FeaturePython)
  n = 2
  ref = C_element
FEATURE [App::DocumentObjectGroupPython] H_element105  label="H_element : 056"  # scripted group (container) (typed FeaturePython)
  n = 1
  ref = H_element
FEATURE [App::DocumentObjectGroupPython] Cl_element028  label="Cl_element : 014"  # scripted group (container) (typed FeaturePython)
  n = 3
  ref = Cl_element
FEATURE [App::DocumentObjectGroupPython] G4_TRICHLOROETHYLENE  # scripted group (container) (typed FeaturePython)
  Dunit = g/cm3
  Dvalue = 1.46
  Group = -> [C_element115,H_element105,Cl_element028]
  conduct = 2
  density = 1
  expand = 3
  formula = G4_TRICHLOROETHYLENE
  name = G4_TRICHLOROETHYLENE
  specific = 4
FEATURE [App::DocumentObjectGroupPython] C_element116  label="C_element : 063"  # scripted group (container) (typed FeaturePython)
  n = 6
  ref = C_element
FEATURE [App::DocumentObjectGroupPython] H_element106  label="H_element : 15"  # scripted group (container) (typed FeaturePython)
  n = 15
  ref = H_element
FEATURE [App::DocumentObjectGroupPython] O_element099  label="O_element : 053"  # scripted group (container) (typed FeaturePython)
  n = 4
  ref = O_element
FEATURE [App::DocumentObjectGroupPython] P_element012  label="P_element : 1"  # scripted group (container) (typed FeaturePython)
  n = 1
  ref = P_element
FEATURE [App::DocumentObjectGroupPython] G4_TRIETHYL_PHOSPHATE  # scripted group (container) (typed FeaturePython)
  Dunit = g/cm3
  Dvalue = 1.07
  Group = -> [C_element116,H_element106,O_element099,P_element012]
  conduct = 2
  density = 1
  expand = 3
  formula = G4_TRIETHYL_PHOSPHATE
  name = G4_TRIETHYL_PHOSPHATE
  specific = 4
FEATURE [App::DocumentObjectGroupPython] W_element003  label="W_element : 003"  # scripted group (container) (typed FeaturePython)
  n = 1
  ref = W_element
FEATURE [App::DocumentObjectGroupPython] F_element017  label="F_element : 6"  # scripted group (container) (typed FeaturePython)
  n = 6
  ref = F_element
FEATURE [App::DocumentObjectGroupPython] G4_TUNGSTEN_HEXAFLUORIDE  # scripted group (container) (typed FeaturePython)
  Dunit = g/cm3
  Dvalue = 2.4
  Group = -> [W_element003,F_element017]
  conduct = 2
  density = 1
  expand = 3
  formula = G4_TUNGSTEN_HEXAFLUORIDE
  name = G4_TUNGSTEN_HEXAFLUORIDE
  specific = 4
FEATURE [App::DocumentObjectGroupPython] U_element001  label="U_element : 1"  # scripted group (container) (typed FeaturePython)
  n = 1
  ref = U_element
FEATURE [App::DocumentObjectGroupPython] C_element117  label="C_element : 064"  # scripted group (container) (typed FeaturePython)
  n = 2
  ref = C_element
FEATURE [App::DocumentObjectGroupPython] G4_URANIUM_DICARBIDE  # scripted group (container) (typed FeaturePython)
  Dunit = g/cm3
  Dvalue = 11.28
  Group = -> [U_element001,C_element117]
  conduct = 2
  density = 1
  expand = 3
  formula = G4_URANIUM_DICARBIDE
  name = G4_URANIUM_DICARBIDE
  specific = 4
FEATURE [App::DocumentObjectGroupPython] U_element002  label="U_element : 002"  # scripted group (container) (typed FeaturePython)
  n = 1
  ref = U_element
FEATURE [App::DocumentObjectGroupPython] C_element118  label="C_element : 065"  # scripted group (container) (typed FeaturePython)
  n = 1
  ref = C_element
FEATURE [App::DocumentObjectGroupPython] G4_URANIUM_MONOCARBIDE  # scripted group (container) (typed FeaturePython)
  Dunit = g/cm3
  Dvalue = 13.63
  Group = -> [U_element002,C_element118]
  conduct = 2
  density = 1
  expand = 3
  formula = G4_URANIUM_MONOCARBIDE
  name = G4_URANIUM_MONOCARBIDE
  specific = 4
FEATURE [App::DocumentObjectGroupPython] U_element003  label="U_element : 003"  # scripted group (container) (typed FeaturePython)
  n = 1
  ref = U_element
FEATURE [App::DocumentObjectGroupPython] O_element100  label="O_element : 054"  # scripted group (container) (typed FeaturePython)
  n = 2
  ref = O_element
FEATURE [App::DocumentObjectGroupPython] G4_URANIUM_OXIDE  # scripted group (container) (typed FeaturePython)
  Dunit = g/cm3
  Dvalue = 10.96
  Group = -> [U_element003,O_element100]
  conduct = 2
  density = 1
  expand = 3
  formula = G4_URANIUM_OXIDE
  name = G4_URANIUM_OXIDE
  specific = 4
FEATURE [App::DocumentObjectGroupPython] C_element119  label="C_element : 066"  # scripted group (container) (typed FeaturePython)
  n = 1
  ref = C_element
FEATURE [App::DocumentObjectGroupPython] H_element107  label="H_element : 057"  # scripted group (container) (typed FeaturePython)
  n = 4
  ref = H_element
FEATURE [App::DocumentObjectGroupPython] N_element046  label="N_element : 019"  # scripted group (container) (typed FeaturePython)
  n = 2
  ref = N_element
FEATURE [App::DocumentObjectGroupPython] O_element101  label="O_element : 055"  # scripted group (container) (typed FeaturePython)
  n = 1
  ref = O_element
FEATURE [App::DocumentObjectGroupPython] G4_UREA  # scripted group (container) (typed FeaturePython)
  Dunit = g/cm3
  Dvalue = 1.323
  Group = -> [C_element119,H_element107,N_element046,O_element101]
  conduct = 2
  density = 1
  expand = 3
  formula = G4_UREA
  name = G4_UREA
  specific = 4
FEATURE [App::DocumentObjectGroupPython] C_element120  label="C_element : 067"  # scripted group (container) (typed FeaturePython)
  n = 5
  ref = C_element
FEATURE [App::DocumentObjectGroupPython] H_element108  label="H_element : 058"  # scripted group (container) (typed FeaturePython)
  n = 11
  ref = H_element
FEATURE [App::DocumentObjectGroupPython] N_element047  label="N_element : 020"  # scripted group (container) (typed FeaturePython)
  n = 1
  ref = N_element
FEATURE [App::DocumentObjectGroupPython] O_element102  label="O_element : 056"  # scripted group (container) (typed FeaturePython)
  n = 2
  ref = O_element
FEATURE [App::DocumentObjectGroupPython] G4_VALINE  # scripted group (container) (typed FeaturePython)
  Dunit = g/cm3
  Dvalue = 1.23
  Group = -> [C_element120,H_element108,N_element047,O_element102]
  conduct = 2
  density = 1
  expand = 3
  formula = G4_VALINE
  name = G4_VALINE
  specific = 4
FEATURE [App::DocumentObjectGroupPython] H_element109  label="H_element : 0.009"  # scripted group (container) (typed FeaturePython)
  n = 0.009417
FEATURE [App::DocumentObjectGroupPython] C_element121  label="C_element : 0.281"  # scripted group (container) (typed FeaturePython)
  n = 0.280555
FEATURE [App::DocumentObjectGroupPython] F_element018  label="F_element : 0.710"  # scripted group (container) (typed FeaturePython)
  n = 0.710028
FEATURE [App::DocumentObjectGroupPython] G4_VITON  # scripted group (container) (typed FeaturePython)
  Dunit = g/cm3
  Dvalue = 1.8
  Group = -> [H_element109,C_element121,F_element018]
  conduct = 2
  density = 1
  expand = 3
  formula = G4_VITON
  name = G4_VITON
  specific = 4
FEATURE [App::DocumentObjectGroupPython] H_element110  label="H_element : 059"  # scripted group (container) (typed FeaturePython)
  n = 2
  ref = H_element
FEATURE [App::DocumentObjectGroupPython] O_element103  label="O_element : 057"  # scripted group (container) (typed FeaturePython)
  n = 1
  ref = O_element
FEATURE [App::DocumentObjectGroupPython] G4_WATER  # scripted group (container) (typed FeaturePython)
  Dunit = g/cm3
  Dvalue = 1
  Group = -> [H_element110,O_element103]
  conduct = 2
  density = 1
  expand = 3
  formula = G4_WATER
  name = G4_WATER
  specific = 4
FEATURE [App::DocumentObjectGroupPython] H_element111  label="H_element : 060"  # scripted group (container) (typed FeaturePython)
  n = 2
  ref = H_element
FEATURE [App::DocumentObjectGroupPython] O_element104  label="O_element : 058"  # scripted group (container) (typed FeaturePython)
  n = 1
  ref = O_element
FEATURE [App::DocumentObjectGroupPython] G4_WATER_VAPOR  # scripted group (container) (typed FeaturePython)
  Dunit = g/cm3
  Dvalue = 0.000756182
  Group = -> [H_element111,O_element104]
  conduct = 2
  density = 1
  expand = 3
  formula = G4_WATER_VAPOR
  name = G4_WATER_VAPOR
  specific = 4
FEATURE [App::DocumentObjectGroupPython] C_element122  label="C_element : 068"  # scripted group (container) (typed FeaturePython)
  n = 8
  ref = C_element
FEATURE [App::DocumentObjectGroupPython] H_element112  label="H_element : 061"  # scripted group (container) (typed FeaturePython)
  n = 10
  ref = H_element
FEATURE [App::DocumentObjectGroupPython] G4_XYLENE  # scripted group (container) (typed FeaturePython)
  Dunit = g/cm3
  Dvalue = 0.87
  Group = -> [C_element122,H_element112]
  conduct = 2
  density = 1
  expand = 3
  formula = G4_XYLENE
  name = G4_XYLENE
  specific = 4
FEATURE [App::DocumentObjectGroupPython] C_element123  label="C_element : 069"  # scripted group (container) (typed FeaturePython)
  n = 1
  ref = C_element
FEATURE [App::DocumentObjectGroupPython] G4_GRAPHITE  # scripted group (container) (typed FeaturePython)
  Dunit = g/cm3
  Dvalue = 2.21
  Group = -> [C_element123]
  conduct = 2
  density = 1
  expand = 3
  formula = G4_GRAPHITE
  name = G4_GRAPHITE
  specific = 4
FEATURE [App::DocumentObjectGroupPython] NIST  # scripted group (container) (typed FeaturePython)
  Group = -> [G4_A_150_TISSUE,G4_ACETONE,G4_ACETYLENE,G4_ADENINE,G4_ADIPOSE_TISSUE_ICRP,G4_AIR,G4_ALANINE,G4_ALUMINUM_OXIDE,G4_AMBER,G4_AMMONIA,G4_ANILINE,G4_ANTHRACENE,G4_B_100_BONE,G4_BAKELITE,G4_BARIUM_FLUORIDE,G4_BARIUM_SULFATE,G4_BENZENE,G4_BERYLLIUM_OXIDE,G4_BGO,G4_BLOOD_ICRP,G4_BONE_COMPACT_ICRU,G4_BONE_CORTICAL_ICRP,G4_BORON_CARBIDE,G4_BORON_OXIDE,G4_BRAIN_ICRP,G4_BUTANE,G4_N_BUTYL_ALCOHOL,G4_C_552,+152 more]
FEATURE [App::DocumentObjectGroupPython] H_element113  label="H_element : 062"  # scripted group (container) (typed FeaturePython)
  n = 1
  ref = H_element
FEATURE [App::DocumentObjectGroupPython] G4_H  # scripted group (container) (typed FeaturePython)
  Dunit = g/cm3
  Dvalue = 8.3748e-05
  Group = -> [H_element113]
  conduct = 2
  density = 1
  expand = 3
  formula = H
  name = G4_H
  specific = 4
FEATURE [App::DocumentObjectGroupPython] He_element001  label="He_element : 1"  # scripted group (container) (typed FeaturePython)
  n = 1
  ref = He_element
FEATURE [App::DocumentObjectGroupPython] G4_He  # scripted group (container) (typed FeaturePython)
  Dunit = g/cm3
  Dvalue = 0.000166322
  Group = -> [He_element001]
  conduct = 2
  density = 1
  expand = 3
  formula = He
  name = G4_He
  specific = 4
FEATURE [App::DocumentObjectGroupPython] Li_element008  label="Li_element : 008"  # scripted group (container) (typed FeaturePython)
  n = 1
  ref = Li_element
FEATURE [App::DocumentObjectGroupPython] G4_Li  # scripted group (container) (typed FeaturePython)
  Dunit = g/cm3
  Dvalue = 0.534
  Group = -> [Li_element008]
  conduct = 2
  density = 1
  expand = 3
  formula = Li
  name = G4_Li
  specific = 4
FEATURE [App::DocumentObjectGroupPython] Be_element002  label="Be_element : 002"  # scripted group (container) (typed FeaturePython)
  n = 1
  ref = Be_element
FEATURE [App::DocumentObjectGroupPython] G4_Be  # scripted group (container) (typed FeaturePython)
  Dunit = g/cm3
  Dvalue = 1.848
  Group = -> [Be_element002]
  conduct = 2
  density = 1
  expand = 3
  formula = Be
  name = G4_Be
  specific = 4
FEATURE [App::DocumentObjectGroupPython] B_element007  label="B_element : 007"  # scripted group (container) (typed FeaturePython)
  n = 1
  ref = B_element
FEATURE [App::DocumentObjectGroupPython] G4_B  # scripted group (container) (typed FeaturePython)
  Dunit = g/cm3
  Dvalue = 2.37
  Group = -> [B_element007]
  conduct = 2
  density = 1
  expand = 3
  formula = B
  name = G4_B
  specific = 4
FEATURE [App::DocumentObjectGroupPython] C_element124  label="C_element : 070"  # scripted group (container) (typed FeaturePython)
  n = 1
  ref = C_element
FEATURE [App::DocumentObjectGroupPython] G4_C  # scripted group (container) (typed FeaturePython)
  Dunit = g/cm3
  Dvalue = 2
  Group = -> [C_element124]
  conduct = 2
  density = 1
  expand = 3
  formula = C
  name = G4_C
  specific = 4
FEATURE [App::DocumentObjectGroupPython] N_element048  label="N_element : 021"  # scripted group (container) (typed FeaturePython)
  n = 1
  ref = N_element
FEATURE [App::DocumentObjectGroupPython] G4_N  # scripted group (container) (typed FeaturePython)
  Dunit = g/cm3
  Dvalue = 0.0011652
  Group = -> [N_element048]
  conduct = 2
  density = 1
  expand = 3
  formula = N
  name = G4_N
  specific = 4
FEATURE [App::DocumentObjectGroupPython] O_element105  label="O_element : 059"  # scripted group (container) (typed FeaturePython)
  n = 1
  ref = O_element
FEATURE [App::DocumentObjectGroupPython] G4_O  # scripted group (container) (typed FeaturePython)
  Dunit = g/cm3
  Dvalue = 0.00133151
  Group = -> [O_element105]
  conduct = 2
  density = 1
  expand = 3
  formula = O
  name = G4_O
  specific = 4
FEATURE [App::DocumentObjectGroupPython] F_element019  label="F_element : 008"  # scripted group (container) (typed FeaturePython)
  n = 1
  ref = F_element
FEATURE [App::DocumentObjectGroupPython] G4_F  # scripted group (container) (typed FeaturePython)
  Dunit = g/cm3
  Dvalue = 0.00158029
  Group = -> [F_element019]
  conduct = 2
  density = 1
  expand = 3
  formula = F
  name = G4_F
  specific = 4
FEATURE [App::DocumentObjectGroupPython] Ne_element001  label="Ne_element : 1"  # scripted group (container) (typed FeaturePython)
  n = 1
  ref = Ne_element
FEATURE [App::DocumentObjectGroupPython] G4_Ne  # scripted group (container) (typed FeaturePython)
  Dunit = g/cm3
  Dvalue = 0.000838505
  Group = -> [Ne_element001]
  conduct = 2
  density = 1
  expand = 3
  formula = Ne
  name = G4_Ne
  specific = 4
FEATURE [App::DocumentObjectGroupPython] Na_element020  label="Na_element : 005"  # scripted group (container) (typed FeaturePython)
  n = 1
  ref = Na_element
FEATURE [App::DocumentObjectGroupPython] G4_Na  # scripted group (container) (typed FeaturePython)
  Dunit = g/cm3
  Dvalue = 0.971
  Group = -> [Na_element020]
  conduct = 2
  density = 1
  expand = 3
  formula = Na
  name = G4_Na
  specific = 4
FEATURE [App::DocumentObjectGroupPython] Mg_element011  label="Mg_element : 005"  # scripted group (container) (typed FeaturePython)
  n = 1
  ref = Mg_element
FEATURE [App::DocumentObjectGroupPython] G4_Mg  # scripted group (container) (typed FeaturePython)
  Dunit = g/cm3
  Dvalue = 1.74
  Group = -> [Mg_element011]
  conduct = 2
  density = 1
  expand = 3
  formula = Mg
  name = G4_Mg
  specific = 4
FEATURE [App::DocumentObjectGroupPython] Al_element004  label="Al_element : 1"  # scripted group (container) (typed FeaturePython)
  n = 1
  ref = Al_element
FEATURE [App::DocumentObjectGroupPython] G4_Al  # scripted group (container) (typed FeaturePython)
  Dunit = g/cm3
  Dvalue = 2.699
  Group = -> [Al_element004]
  conduct = 2
  density = 1
  expand = 3
  formula = Al
  name = G4_Al
  specific = 4
FEATURE [App::DocumentObjectGroupPython] Si_element007  label="Si_element : 002"  # scripted group (container) (typed FeaturePython)
  n = 1
  ref = Si_element
FEATURE [App::DocumentObjectGroupPython] G4_Si  # scripted group (container) (typed FeaturePython)
  Dunit = g/cm3
  Dvalue = 2.33
  Group = -> [Si_element007]
  conduct = 2
  density = 1
  expand = 3
  formula = Si
  name = G4_Si
  specific = 4
FEATURE [App::DocumentObjectGroupPython] P_element013  label="P_element : 002"  # scripted group (container) (typed FeaturePython)
  n = 1
  ref = P_element
FEATURE [App::DocumentObjectGroupPython] G4_P  # scripted group (container) (typed FeaturePython)
  Dunit = g/cm3
  Dvalue = 2.2
  Group = -> [P_element013]
  conduct = 2
  density = 1
  expand = 3
  formula = P
  name = G4_P
  specific = 4
FEATURE [App::DocumentObjectGroupPython] S_element023  label="S_element : 007"  # scripted group (container) (typed FeaturePython)
  n = 1
  ref = S_element
FEATURE [App::DocumentObjectGroupPython] G4_S  # scripted group (container) (typed FeaturePython)
  Dunit = g/cm3
  Dvalue = 2
  Group = -> [S_element023]
  conduct = 2
  density = 1
  expand = 3
  formula = S
  name = G4_S
  specific = 4
FEATURE [App::DocumentObjectGroupPython] Cl_element029  label="Cl_element : 015"  # scripted group (container) (typed FeaturePython)
  n = 1
  ref = Cl_element
FEATURE [App::DocumentObjectGroupPython] G4_Cl  # scripted group (container) (typed FeaturePython)
  Dunit = g/cm3
  Dvalue = 0.00299473
  Group = -> [Cl_element029]
  conduct = 2
  density = 1
  expand = 3
  formula = Cl
  name = G4_Cl
  specific = 4
FEATURE [App::DocumentObjectGroupPython] Ar_element002  label="Ar_element : 1"  # scripted group (container) (typed FeaturePython)
  n = 1
  ref = Ar_element
FEATURE [App::DocumentObjectGroupPython] G4_Ar  # scripted group (container) (typed FeaturePython)
  Dunit = g/cm3
  Dvalue = 0.00166201
  Group = -> [Ar_element002]
  conduct = 2
  density = 1
  expand = 3
  formula = Ar
  name = G4_Ar
  specific = 4
FEATURE [App::DocumentObjectGroupPython] K_element013  label="K_element : 003"  # scripted group (container) (typed FeaturePython)
  n = 1
  ref = K_element
FEATURE [App::DocumentObjectGroupPython] G4_K  # scripted group (container) (typed FeaturePython)
  Dunit = g/cm3
  Dvalue = 0.862
  Group = -> [K_element013]
  conduct = 2
  density = 1
  expand = 3
  formula = K
  name = G4_K
  specific = 4
FEATURE [App::DocumentObjectGroupPython] Ca_element014  label="Ca_element : 007"  # scripted group (container) (typed FeaturePython)
  n = 1
  ref = Ca_element
FEATURE [App::DocumentObjectGroupPython] G4_Ca  # scripted group (container) (typed FeaturePython)
  Dunit = g/cm3
  Dvalue = 1.55
  Group = -> [Ca_element014]
  conduct = 2
  density = 1
  expand = 3
  formula = Ca
  name = G4_Ca
  specific = 4
FEATURE [App::DocumentObjectGroupPython] Sc_element001  label="Sc_element : 1"  # scripted group (container) (typed FeaturePython)
  n = 1
  ref = Sc_element
FEATURE [App::DocumentObjectGroupPython] G4_Sc  # scripted group (container) (typed FeaturePython)
  Dunit = g/cm3
  Dvalue = 2.989
  Group = -> [Sc_element001]
  conduct = 2
  density = 1
  expand = 3
  formula = Sc
  name = G4_Sc
  specific = 4
FEATURE [App::DocumentObjectGroupPython] Ti_element004  label="Ti_element : 002"  # scripted group (container) (typed FeaturePython)
  n = 1
  ref = Ti_element
FEATURE [App::DocumentObjectGroupPython] G4_Ti  # scripted group (container) (typed FeaturePython)
  Dunit = g/cm3
  Dvalue = 4.54
  Group = -> [Ti_element004]
  conduct = 2
  density = 1
  expand = 3
  formula = Ti
  name = G4_Ti
  specific = 4
FEATURE [App::DocumentObjectGroupPython] V_element001  label="V_element : 1"  # scripted group (container) (typed FeaturePython)
  n = 1
  ref = V_element
FEATURE [App::DocumentObjectGroupPython] G4_V  # scripted group (container) (typed FeaturePython)
  Dunit = g/cm3
  Dvalue = 6.11
  Group = -> [V_element001]
  conduct = 2
  density = 1
  expand = 3
  formula = V
  name = G4_V
  specific = 4
FEATURE [App::DocumentObjectGroupPython] Cr_element001  label="Cr_element : 1"  # scripted group (container) (typed FeaturePython)
  n = 1
  ref = Cr_element
FEATURE [App::DocumentObjectGroupPython] G4_Cr  # scripted group (container) (typed FeaturePython)
  Dunit = g/cm3
  Dvalue = 7.18
  Group = -> [Cr_element001]
  conduct = 2
  density = 1
  expand = 3
  formula = Cr
  name = G4_Cr
  specific = 4
FEATURE [App::DocumentObjectGroupPython] Mn_element001  label="Mn_element : 1"  # scripted group (container) (typed FeaturePython)
  n = 1
  ref = Mn_element
FEATURE [App::DocumentObjectGroupPython] G4_Mn  # scripted group (container) (typed FeaturePython)
  Dunit = g/cm3
  Dvalue = 7.44
  Group = -> [Mn_element001]
  conduct = 2
  density = 1
  expand = 3
  formula = Mn
  name = G4_Mn
  specific = 4
FEATURE [App::DocumentObjectGroupPython] Fe_element007  label="Fe_element : 004"  # scripted group (container) (typed FeaturePython)
  n = 1
  ref = Fe_element
FEATURE [App::DocumentObjectGroupPython] G4_Fe  # scripted group (container) (typed FeaturePython)
  Dunit = g/cm3
  Dvalue = 7.874
  Group = -> [Fe_element007]
  conduct = 2
  density = 1
  expand = 3
  formula = Fe
  name = G4_Fe
  specific = 4
FEATURE [App::DocumentObjectGroupPython] Co_element001  label="Co_element : 1"  # scripted group (container) (typed FeaturePython)
  n = 1
  ref = Co_element
FEATURE [App::DocumentObjectGroupPython] G4_Co  # scripted group (container) (typed FeaturePython)
  Dunit = g/cm3
  Dvalue = 8.9
  Group = -> [Co_element001]
  conduct = 2
  density = 1
  expand = 3
  formula = Co
  name = G4_Co
  specific = 4
FEATURE [App::DocumentObjectGroupPython] Ni_element001  label="Ni_element : 1"  # scripted group (container) (typed FeaturePython)
  n = 1
  ref = Ni_element
FEATURE [App::DocumentObjectGroupPython] G4_Ni  # scripted group (container) (typed FeaturePython)
  Dunit = g/cm3
  Dvalue = 8.902
  Group = -> [Ni_element001]
  conduct = 2
  density = 1
  expand = 3
  formula = Ni
  name = G4_Ni
  specific = 4
FEATURE [App::DocumentObjectGroupPython] Cu_element001  label="Cu_element : 1"  # scripted group (container) (typed FeaturePython)
  n = 1
  ref = Cu_element
FEATURE [App::DocumentObjectGroupPython] G4_Cu  # scripted group (container) (typed FeaturePython)
  Dunit = g/cm3
  Dvalue = 8.96
  Group = -> [Cu_element001]
  conduct = 2
  density = 1
  expand = 3
  formula = Cu
  name = G4_Cu
  specific = 4
FEATURE [App::DocumentObjectGroupPython] Zn_element001  label="Zn_element : 1"  # scripted group (container) (typed FeaturePython)
  n = 1
  ref = Zn_element
FEATURE [App::DocumentObjectGroupPython] G4_Zn  # scripted group (container) (typed FeaturePython)
  Dunit = g/cm3
  Dvalue = 7.133
  Group = -> [Zn_element001]
  conduct = 2
  density = 1
  expand = 3
  formula = Zn
  name = G4_Zn
  specific = 4
FEATURE [App::DocumentObjectGroupPython] Ga_element002  label="Ga_element : 002"  # scripted group (container) (typed FeaturePython)
  n = 1
  ref = Ga_element
FEATURE [App::DocumentObjectGroupPython] G4_Ga  # scripted group (container) (typed FeaturePython)
  Dunit = g/cm3
  Dvalue = 5.904
  Group = -> [Ga_element002]
  conduct = 2
  density = 1
  expand = 3
  formula = Ga
  name = G4_Ga
  specific = 4
FEATURE [App::DocumentObjectGroupPython] Ge_element002  label="Ge_element : 1"  # scripted group (container) (typed FeaturePython)
  n = 1
  ref = Ge_element
FEATURE [App::DocumentObjectGroupPython] G4_Ge  # scripted group (container) (typed FeaturePython)
  Dunit = g/cm3
  Dvalue = 5.323
  Group = -> [Ge_element002]
  conduct = 2
  density = 1
  expand = 3
  formula = Ge
  name = G4_Ge
  specific = 4
FEATURE [App::DocumentObjectGroupPython] As_element003  label="As_element : 002"  # scripted group (container) (typed FeaturePython)
  n = 1
  ref = As_element
FEATURE [App::DocumentObjectGroupPython] G4_As  # scripted group (container) (typed FeaturePython)
  Dunit = g/cm3
  Dvalue = 5.73
  Group = -> [As_element003]
  conduct = 2
  density = 1
  expand = 3
  formula = As
  name = G4_As
  specific = 4
FEATURE [App::DocumentObjectGroupPython] Se_element001  label="Se_element : 1"  # scripted group (container) (typed FeaturePython)
  n = 1
  ref = Se_element
FEATURE [App::DocumentObjectGroupPython] G4_Se  # scripted group (container) (typed FeaturePython)
  Dunit = g/cm3
  Dvalue = 4.5
  Group = -> [Se_element001]
  conduct = 2
  density = 1
  expand = 3
  formula = Se
  name = G4_Se
  specific = 4
FEATURE [App::DocumentObjectGroupPython] Br_element007  label="Br_element : 004"  # scripted group (container) (typed FeaturePython)
  n = 1
  ref = Br_element
FEATURE [App::DocumentObjectGroupPython] G4_Br  # scripted group (container) (typed FeaturePython)
  Dunit = g/cm3
  Dvalue = 0.0070721
  Group = -> [Br_element007]
  conduct = 2
  density = 1
  expand = 3
  formula = Br
  name = G4_Br
  specific = 4
FEATURE [App::DocumentObjectGroupPython] Kr_element001  label="Kr_element : 1"  # scripted group (container) (typed FeaturePython)
  n = 1
  ref = Kr_element
FEATURE [App::DocumentObjectGroupPython] G4_Kr  # scripted group (container) (typed FeaturePython)
  Dunit = g/cm3
  Dvalue = 0.00347832
  Group = -> [Kr_element001]
  conduct = 2
  density = 1
  expand = 3
  formula = Kr
  name = G4_Kr
  specific = 4
FEATURE [App::DocumentObjectGroupPython] Rb_element001  label="Rb_element : 1"  # scripted group (container) (typed FeaturePython)
  n = 1
  ref = Rb_element
FEATURE [App::DocumentObjectGroupPython] G4_Rb  # scripted group (container) (typed FeaturePython)
  Dunit = g/cm3
  Dvalue = 1.532
  Group = -> [Rb_element001]
  conduct = 2
  density = 1
  expand = 3
  formula = Rb
  name = G4_Rb
  specific = 4
FEATURE [App::DocumentObjectGroupPython] Sr_element001  label="Sr_element : 1"  # scripted group (container) (typed FeaturePython)
  n = 1
  ref = Sr_element
FEATURE [App::DocumentObjectGroupPython] G4_Sr  # scripted group (container) (typed FeaturePython)
  Dunit = g/cm3
  Dvalue = 2.54
  Group = -> [Sr_element001]
  conduct = 2
  density = 1
  expand = 3
  formula = Sr
  name = G4_Sr
  specific = 4
FEATURE [App::DocumentObjectGroupPython] Y_element001  label="Y_element : 1"  # scripted group (container) (typed FeaturePython)
  n = 1
  ref = Y_element
FEATURE [App::DocumentObjectGroupPython] G4_Y  # scripted group (container) (typed FeaturePython)
  Dunit = g/cm3
  Dvalue = 4.469
  Group = -> [Y_element001]
  conduct = 2
  density = 1
  expand = 3
  formula = Y
  name = G4_Y
  specific = 4
FEATURE [App::DocumentObjectGroupPython] Zr_element001  label="Zr_element : 1"  # scripted group (container) (typed FeaturePython)
  n = 1
  ref = Zr_element
FEATURE [App::DocumentObjectGroupPython] G4_Zr  # scripted group (container) (typed FeaturePython)
  Dunit = g/cm3
  Dvalue = 6.506
  Group = -> [Zr_element001]
  conduct = 2
  density = 1
  expand = 3
  formula = Zr
  name = G4_Zr
  specific = 4
FEATURE [App::DocumentObjectGroupPython] Nb_element001  label="Nb_element : 1"  # scripted group (container) (typed FeaturePython)
  n = 1
  ref = Nb_element
FEATURE [App::DocumentObjectGroupPython] G4_Nb  # scripted group (container) (typed FeaturePython)
  Dunit = g/cm3
  Dvalue = 8.57
  Group = -> [Nb_element001]
  conduct = 2
  density = 1
  expand = 3
  formula = Nb
  name = G4_Nb
  specific = 4
FEATURE [App::DocumentObjectGroupPython] Mo_element001  label="Mo_element : 1"  # scripted group (container) (typed FeaturePython)
  n = 1
  ref = Mo_element
FEATURE [App::DocumentObjectGroupPython] G4_Mo  # scripted group (container) (typed FeaturePython)
  Dunit = g/cm3
  Dvalue = 10.22
  Group = -> [Mo_element001]
  conduct = 2
  density = 1
  expand = 3
  formula = Mo
  name = G4_Mo
  specific = 4
FEATURE [App::DocumentObjectGroupPython] Tc_element001  label="Tc_element : 1"  # scripted group (container) (typed FeaturePython)
  n = 1
  ref = Tc_element
FEATURE [App::DocumentObjectGroupPython] G4_Tc  # scripted group (container) (typed FeaturePython)
  Dunit = g/cm3
  Dvalue = 11.5
  Group = -> [Tc_element001]
  conduct = 2
  density = 1
  expand = 3
  formula = Tc
  name = G4_Tc
  specific = 4
FEATURE [App::DocumentObjectGroupPython] Ru_element001  label="Ru_element : 1"  # scripted group (container) (typed FeaturePython)
  n = 1
  ref = Ru_element
FEATURE [App::DocumentObjectGroupPython] G4_Ru  # scripted group (container) (typed FeaturePython)
  Dunit = g/cm3
  Dvalue = 12.41
  Group = -> [Ru_element001]
  conduct = 2
  density = 1
  expand = 3
  formula = Ru
  name = G4_Ru
  specific = 4
FEATURE [App::DocumentObjectGroupPython] Rh_element001  label="Rh_element : 1"  # scripted group (container) (typed FeaturePython)
  n = 1
  ref = Rh_element
FEATURE [App::DocumentObjectGroupPython] G4_Rh  # scripted group (container) (typed FeaturePython)
  Dunit = g/cm3
  Dvalue = 12.41
  Group = -> [Rh_element001]
  conduct = 2
  density = 1
  expand = 3
  formula = Rh
  name = G4_Rh
  specific = 4
FEATURE [App::DocumentObjectGroupPython] Pd_element001  label="Pd_element : 1"  # scripted group (container) (typed FeaturePython)
  n = 1
  ref = Pd_element
FEATURE [App::DocumentObjectGroupPython] G4_Pd  # scripted group (container) (typed FeaturePython)
  Dunit = g/cm3
  Dvalue = 12.02
  Group = -> [Pd_element001]
  conduct = 2
  density = 1
  expand = 3
  formula = Pd
  name = G4_Pd
  specific = 4
FEATURE [App::DocumentObjectGroupPython] Ag_element006  label="Ag_element : 004"  # scripted group (container) (typed FeaturePython)
  n = 1
  ref = Ag_element
FEATURE [App::DocumentObjectGroupPython] G4_Ag  # scripted group (container) (typed FeaturePython)
  Dunit = g/cm3
  Dvalue = 10.5
  Group = -> [Ag_element006]
  conduct = 2
  density = 1
  expand = 3
  formula = Ag
  name = G4_Ag
  specific = 4
FEATURE [App::DocumentObjectGroupPython] Cd_element003  label="Cd_element : 003"  # scripted group (container) (typed FeaturePython)
  n = 1
  ref = Cd_element
FEATURE [App::DocumentObjectGroupPython] G4_Cd  # scripted group (container) (typed FeaturePython)
  Dunit = g/cm3
  Dvalue = 8.65
  Group = -> [Cd_element003]
  conduct = 2
  density = 1
  expand = 3
  formula = Cd
  name = G4_Cd
  specific = 4
FEATURE [App::DocumentObjectGroupPython] In_element001  label="In_element : 1"  # scripted group (container) (typed FeaturePython)
  n = 1
  ref = In_element
FEATURE [App::DocumentObjectGroupPython] G4_In  # scripted group (container) (typed FeaturePython)
  Dunit = g/cm3
  Dvalue = 7.31
  Group = -> [In_element001]
  conduct = 2
  density = 1
  expand = 3
  formula = In
  name = G4_In
  specific = 4
FEATURE [App::DocumentObjectGroupPython] Sn_element001  label="Sn_element : 1"  # scripted group (container) (typed FeaturePython)
  n = 1
  ref = Sn_element
FEATURE [App::DocumentObjectGroupPython] G4_Sn  # scripted group (container) (typed FeaturePython)
  Dunit = g/cm3
  Dvalue = 7.31
  Group = -> [Sn_element001]
  conduct = 2
  density = 1
  expand = 3
  formula = Sn
  name = G4_Sn
  specific = 4
FEATURE [App::DocumentObjectGroupPython] Sb_element001  label="Sb_element : 1"  # scripted group (container) (typed FeaturePython)
  n = 1
  ref = Sb_element
FEATURE [App::DocumentObjectGroupPython] G4_Sb  # scripted group (container) (typed FeaturePython)
  Dunit = g/cm3
  Dvalue = 6.691
  Group = -> [Sb_element001]
  conduct = 2
  density = 1
  expand = 3
  formula = Sb
  name = G4_Sb
  specific = 4
FEATURE [App::DocumentObjectGroupPython] Te_element002  label="Te_element : 002"  # scripted group (container) (typed FeaturePython)
  n = 1
  ref = Te_element
FEATURE [App::DocumentObjectGroupPython] G4_Te  # scripted group (container) (typed FeaturePython)
  Dunit = g/cm3
  Dvalue = 6.24
  Group = -> [Te_element002]
  conduct = 2
  density = 1
  expand = 3
  formula = Te
  name = G4_Te
  specific = 4
FEATURE [App::DocumentObjectGroupPython] I_element010  label="I_element : 006"  # scripted group (container) (typed FeaturePython)
  n = 1
  ref = I_element
FEATURE [App::DocumentObjectGroupPython] G4_I  # scripted group (container) (typed FeaturePython)
  Dunit = g/cm3
  Dvalue = 4.93
  Group = -> [I_element010]
  conduct = 2
  density = 1
  expand = 3
  formula = I
  name = G4_I
  specific = 4
FEATURE [App::DocumentObjectGroupPython] Xe_element001  label="Xe_element : 1"  # scripted group (container) (typed FeaturePython)
  n = 1
  ref = Xe_element
FEATURE [App::DocumentObjectGroupPython] G4_Xe  # scripted group (container) (typed FeaturePython)
  Dunit = g/cm3
  Dvalue = 0.00548536
  Group = -> [Xe_element001]
  conduct = 2
  density = 1
  expand = 3
  formula = Xe
  name = G4_Xe
  specific = 4
FEATURE [App::DocumentObjectGroupPython] Cs_element003  label="Cs_element : 003"  # scripted group (container) (typed FeaturePython)
  n = 1
  ref = Cs_element
FEATURE [App::DocumentObjectGroupPython] G4_Cs  # scripted group (container) (typed FeaturePython)
  Dunit = g/cm3
  Dvalue = 1.873
  Group = -> [Cs_element003]
  conduct = 2
  density = 1
  expand = 3
  formula = Cs
  name = G4_Cs
  specific = 4
FEATURE [App::DocumentObjectGroupPython] Ba_element003  label="Ba_element : 003"  # scripted group (container) (typed FeaturePython)
  n = 1
  ref = Ba_element
FEATURE [App::DocumentObjectGroupPython] G4_Ba  # scripted group (container) (typed FeaturePython)
  Dunit = g/cm3
  Dvalue = 3.5
  Group = -> [Ba_element003]
  conduct = 2
  density = 1
  expand = 3
  formula = Ba
  name = G4_Ba
  specific = 4
FEATURE [App::DocumentObjectGroupPython] La_element003  label="La_element : 003"  # scripted group (container) (typed FeaturePython)
  n = 1
  ref = La_element
FEATURE [App::DocumentObjectGroupPython] G4_La  # scripted group (container) (typed FeaturePython)
  Dunit = g/cm3
  Dvalue = 6.154
  Group = -> [La_element003]
  conduct = 2
  density = 1
  expand = 3
  formula = La
  name = G4_La
  specific = 4
FEATURE [App::DocumentObjectGroupPython] Ce_element002  label="Ce_element : 1"  # scripted group (container) (typed FeaturePython)
  n = 1
  ref = Ce_element
FEATURE [App::DocumentObjectGroupPython] G4_Ce  # scripted group (container) (typed FeaturePython)
  Dunit = g/cm3
  Dvalue = 6.657
  Group = -> [Ce_element002]
  conduct = 2
  density = 1
  expand = 3
  formula = Ce
  name = G4_Ce
  specific = 4
FEATURE [App::DocumentObjectGroupPython] Pr_element001  label="Pr_element : 1"  # scripted group (container) (typed FeaturePython)
  n = 1
  ref = Pr_element
FEATURE [App::DocumentObjectGroupPython] G4_Pr  # scripted group (container) (typed FeaturePython)
  Dunit = g/cm3
  Dvalue = 6.71
  Group = -> [Pr_element001]
  conduct = 2
  density = 1
  expand = 3
  formula = Pr
  name = G4_Pr
  specific = 4
FEATURE [App::DocumentObjectGroupPython] Nd_element001  label="Nd_element : 1"  # scripted group (container) (typed FeaturePython)
  n = 1
  ref = Nd_element
FEATURE [App::DocumentObjectGroupPython] G4_Nd  # scripted group (container) (typed FeaturePython)
  Dunit = g/cm3
  Dvalue = 6.9
  Group = -> [Nd_element001]
  conduct = 2
  density = 1
  expand = 3
  formula = Nd
  name = G4_Nd
  specific = 4
FEATURE [App::DocumentObjectGroupPython] Pm_element001  label="Pm_element : 1"  # scripted group (container) (typed FeaturePython)
  n = 1
  ref = Pm_element
FEATURE [App::DocumentObjectGroupPython] G4_Pm  # scripted group (container) (typed FeaturePython)
  Dunit = g/cm3
  Dvalue = 7.22
  Group = -> [Pm_element001]
  conduct = 2
  density = 1
  expand = 3
  formula = Pm
  name = G4_Pm
  specific = 4
FEATURE [App::DocumentObjectGroupPython] Sm_element001  label="Sm_element : 1"  # scripted group (container) (typed FeaturePython)
  n = 1
  ref = Sm_element
FEATURE [App::DocumentObjectGroupPython] G4_Sm  # scripted group (container) (typed FeaturePython)
  Dunit = g/cm3
  Dvalue = 7.46
  Group = -> [Sm_element001]
  conduct = 2
  density = 1
  expand = 3
  formula = Sm
  name = G4_Sm
  specific = 4
FEATURE [App::DocumentObjectGroupPython] Eu_element001  label="Eu_element : 1"  # scripted group (container) (typed FeaturePython)
  n = 1
  ref = Eu_element
FEATURE [App::DocumentObjectGroupPython] G4_Eu  # scripted group (container) (typed FeaturePython)
  Dunit = g/cm3
  Dvalue = 5.243
  Group = -> [Eu_element001]
  conduct = 2
  density = 1
  expand = 3
  formula = Eu
  name = G4_Eu
  specific = 4
FEATURE [App::DocumentObjectGroupPython] Gd_element002  label="Gd_element : 1"  # scripted group (container) (typed FeaturePython)
  n = 1
  ref = Gd_element
FEATURE [App::DocumentObjectGroupPython] G4_Gd  # scripted group (container) (typed FeaturePython)
  Dunit = g/cm3
  Dvalue = 7.9004
  Group = -> [Gd_element002]
  conduct = 2
  density = 1
  expand = 3
  formula = Gd
  name = G4_Gd
  specific = 4
FEATURE [App::DocumentObjectGroupPython] Tb_element001  label="Tb_element : 1"  # scripted group (container) (typed FeaturePython)
  n = 1
  ref = Tb_element
FEATURE [App::DocumentObjectGroupPython] G4_Tb  # scripted group (container) (typed FeaturePython)
  Dunit = g/cm3
  Dvalue = 8.229
  Group = -> [Tb_element001]
  conduct = 2
  density = 1
  expand = 3
  formula = Tb
  name = G4_Tb
  specific = 4
FEATURE [App::DocumentObjectGroupPython] Dy_element001  label="Dy_element : 1"  # scripted group (container) (typed FeaturePython)
  n = 1
  ref = Dy_element
FEATURE [App::DocumentObjectGroupPython] G4_Dy  # scripted group (container) (typed FeaturePython)
  Dunit = g/cm3
  Dvalue = 8.55
  Group = -> [Dy_element001]
  conduct = 2
  density = 1
  expand = 3
  formula = Dy
  name = G4_Dy
  specific = 4
FEATURE [App::DocumentObjectGroupPython] Ho_element001  label="Ho_element : 1"  # scripted group (container) (typed FeaturePython)
  n = 1
  ref = Ho_element
FEATURE [App::DocumentObjectGroupPython] G4_Ho  # scripted group (container) (typed FeaturePython)
  Dunit = g/cm3
  Dvalue = 8.795
  Group = -> [Ho_element001]
  conduct = 2
  density = 1
  expand = 3
  formula = Ho
  name = G4_Ho
  specific = 4
FEATURE [App::DocumentObjectGroupPython] Er_element001  label="Er_element : 1"  # scripted group (container) (typed FeaturePython)
  n = 1
  ref = Er_element
FEATURE [App::DocumentObjectGroupPython] G4_Er  # scripted group (container) (typed FeaturePython)
  Dunit = g/cm3
  Dvalue = 9.066
  Group = -> [Er_element001]
  conduct = 2
  density = 1
  expand = 3
  formula = Er
  name = G4_Er
  specific = 4
FEATURE [App::DocumentObjectGroupPython] Tm_element001  label="Tm_element : 1"  # scripted group (container) (typed FeaturePython)
  n = 1
  ref = Tm_element
FEATURE [App::DocumentObjectGroupPython] G4_Tm  # scripted group (container) (typed FeaturePython)
  Dunit = g/cm3
  Dvalue = 9.321
  Group = -> [Tm_element001]
  conduct = 2
  density = 1
  expand = 3
  formula = Tm
  name = G4_Tm
  specific = 4
FEATURE [App::DocumentObjectGroupPython] Yb_element001  label="Yb_element : 1"  # scripted group (container) (typed FeaturePython)
  n = 1
  ref = Yb_element
FEATURE [App::DocumentObjectGroupPython] G4_Yb  # scripted group (container) (typed FeaturePython)
  Dunit = g/cm3
  Dvalue = 6.73
  Group = -> [Yb_element001]
  conduct = 2
  density = 1
  expand = 3
  formula = Yb
  name = G4_Yb
  specific = 4
FEATURE [App::DocumentObjectGroupPython] Lu_element001  label="Lu_element : 1"  # scripted group (container) (typed FeaturePython)
  n = 1
  ref = Lu_element
FEATURE [App::DocumentObjectGroupPython] G4_Lu  # scripted group (container) (typed FeaturePython)
  Dunit = g/cm3
  Dvalue = 9.84
  Group = -> [Lu_element001]
  conduct = 2
  density = 1
  expand = 3
  formula = Lu
  name = G4_Lu
  specific = 4
FEATURE [App::DocumentObjectGroupPython] Hf_element001  label="Hf_element : 1"  # scripted group (container) (typed FeaturePython)
  n = 1
  ref = Hf_element
FEATURE [App::DocumentObjectGroupPython] G4_Hf  # scripted group (container) (typed FeaturePython)
  Dunit = g/cm3
  Dvalue = 13.31
  Group = -> [Hf_element001]
  conduct = 2
  density = 1
  expand = 3
  formula = Hf
  name = G4_Hf
  specific = 4
FEATURE [App::DocumentObjectGroupPython] Ta_element001  label="Ta_element : 1"  # scripted group (container) (typed FeaturePython)
  n = 1
  ref = Ta_element
FEATURE [App::DocumentObjectGroupPython] G4_Ta  # scripted group (container) (typed FeaturePython)
  Dunit = g/cm3
  Dvalue = 16.654
  Group = -> [Ta_element001]
  conduct = 2
  density = 1
  expand = 3
  formula = Ta
  name = G4_Ta
  specific = 4
FEATURE [App::DocumentObjectGroupPython] W_element004  label="W_element : 004"  # scripted group (container) (typed FeaturePython)
  n = 1
  ref = W_element
FEATURE [App::DocumentObjectGroupPython] G4_W  # scripted group (container) (typed FeaturePython)
  Dunit = g/cm3
  Dvalue = 19.3
  Group = -> [W_element004]
  conduct = 2
  density = 1
  expand = 3
  formula = W
  name = G4_W
  specific = 4
FEATURE [App::DocumentObjectGroupPython] Re_element001  label="Re_element : 1"  # scripted group (container) (typed FeaturePython)
  n = 1
  ref = Re_element
FEATURE [App::DocumentObjectGroupPython] G4_Re  # scripted group (container) (typed FeaturePython)
  Dunit = g/cm3
  Dvalue = 21.02
  Group = -> [Re_element001]
  conduct = 2
  density = 1
  expand = 3
  formula = Re
  name = G4_Re
  specific = 4
FEATURE [App::DocumentObjectGroupPython] Os_element001  label="Os_element : 1"  # scripted group (container) (typed FeaturePython)
  n = 1
  ref = Os_element
FEATURE [App::DocumentObjectGroupPython] G4_Os  # scripted group (container) (typed FeaturePython)
  Dunit = g/cm3
  Dvalue = 22.57
  Group = -> [Os_element001]
  conduct = 2
  density = 1
  expand = 3
  formula = Os
  name = G4_Os
  specific = 4
FEATURE [App::DocumentObjectGroupPython] Ir_element001  label="Ir_element : 1"  # scripted group (container) (typed FeaturePython)
  n = 1
  ref = Ir_element
FEATURE [App::DocumentObjectGroupPython] G4_Ir  # scripted group (container) (typed FeaturePython)
  Dunit = g/cm3
  Dvalue = 22.42
  Group = -> [Ir_element001]
  conduct = 2
  density = 1
  expand = 3
  formula = Ir
  name = G4_Ir
  specific = 4
FEATURE [App::DocumentObjectGroupPython] Pt_element001  label="Pt_element : 1"  # scripted group (container) (typed FeaturePython)
  n = 1
  ref = Pt_element
FEATURE [App::DocumentObjectGroupPython] G4_Pt  # scripted group (container) (typed FeaturePython)
  Dunit = g/cm3
  Dvalue = 21.45
  Group = -> [Pt_element001]
  conduct = 2
  density = 1
  expand = 3
  formula = Pt
  name = G4_Pt
  specific = 4
FEATURE [App::DocumentObjectGroupPython] Au_element001  label="Au_element : 1"  # scripted group (container) (typed FeaturePython)
  n = 1
  ref = Au_element
FEATURE [App::DocumentObjectGroupPython] G4_Au  # scripted group (container) (typed FeaturePython)
  Dunit = g/cm3
  Dvalue = 19.32
  Group = -> [Au_element001]
  conduct = 2
  density = 1
  expand = 3
  formula = Au
  name = G4_Au
  specific = 4
FEATURE [App::DocumentObjectGroupPython] Hg_element002  label="Hg_element : 002"  # scripted group (container) (typed FeaturePython)
  n = 1
  ref = Hg_element
FEATURE [App::DocumentObjectGroupPython] G4_Hg  # scripted group (container) (typed FeaturePython)
  Dunit = g/cm3
  Dvalue = 13.546
  Group = -> [Hg_element002]
  conduct = 2
  density = 1
  expand = 3
  formula = Hg
  name = G4_Hg
  specific = 4
FEATURE [App::DocumentObjectGroupPython] Tl_element002  label="Tl_element : 002"  # scripted group (container) (typed FeaturePython)
  n = 1
  ref = Tl_element
FEATURE [App::DocumentObjectGroupPython] G4_Tl  # scripted group (container) (typed FeaturePython)
  Dunit = g/cm3
  Dvalue = 11.72
  Group = -> [Tl_element002]
  conduct = 2
  density = 1
  expand = 3
  formula = Tl
  name = G4_Tl
  specific = 4
FEATURE [App::DocumentObjectGroupPython] Pb_element003  label="Pb_element : 1"  # scripted group (container) (typed FeaturePython)
  n = 1
  ref = Pb_element
FEATURE [App::DocumentObjectGroupPython] G4_Pb  # scripted group (container) (typed FeaturePython)
  Dunit = g/cm3
  Dvalue = 11.35
  Group = -> [Pb_element003]
  conduct = 2
  density = 1
  expand = 3
  formula = Pb
  name = G4_Pb
  specific = 4
FEATURE [App::DocumentObjectGroupPython] Bi_element002  label="Bi_element : 1"  # scripted group (container) (typed FeaturePython)
  n = 1
  ref = Bi_element
FEATURE [App::DocumentObjectGroupPython] G4_Bi  # scripted group (container) (typed FeaturePython)
  Dunit = g/cm3
  Dvalue = 9.747
  Group = -> [Bi_element002]
  conduct = 2
  density = 1
  expand = 3
  formula = Bi
  name = G4_Bi
  specific = 4
FEATURE [App::DocumentObjectGroupPython] Po_element001  label="Po_element : 1"  # scripted group (container) (typed FeaturePython)
  n = 1
  ref = Po_element
FEATURE [App::DocumentObjectGroupPython] G4_Po  # scripted group (container) (typed FeaturePython)
  Dunit = g/cm3
  Dvalue = 9.32
  Group = -> [Po_element001]
  conduct = 2
  density = 1
  expand = 3
  formula = Po
  name = G4_Po
  specific = 4
FEATURE [App::DocumentObjectGroupPython] At_element001  label="At_element : 1"  # scripted group (container) (typed FeaturePython)
  n = 1
  ref = At_element
FEATURE [App::DocumentObjectGroupPython] G4_At  # scripted group (container) (typed FeaturePython)
  Dunit = g/cm3
  Dvalue = 9.32
  Group = -> [At_element001]
  conduct = 2
  density = 1
  expand = 3
  formula = At
  name = G4_At
  specific = 4
FEATURE [App::DocumentObjectGroupPython] Rn_element001  label="Rn_element : 1"  # scripted group (container) (typed FeaturePython)
  n = 1
  ref = Rn_element
FEATURE [App::DocumentObjectGroupPython] G4_Rn  # scripted group (container) (typed FeaturePython)
  Dunit = g/cm3
  Dvalue = 0.00900662
  Group = -> [Rn_element001]
  conduct = 2
  density = 1
  expand = 3
  formula = Rn
  name = G4_Rn
  specific = 4
FEATURE [App::DocumentObjectGroupPython] Fr_element001  label="Fr_element : 1"  # scripted group (container) (typed FeaturePython)
  n = 1
  ref = Fr_element
FEATURE [App::DocumentObjectGroupPython] G4_Fr  # scripted group (container) (typed FeaturePython)
  Dunit = g/cm3
  Dvalue = 1
  Group = -> [Fr_element001]
  conduct = 2
  density = 1
  expand = 3
  formula = Fr
  name = G4_Fr
  specific = 4
FEATURE [App::DocumentObjectGroupPython] Ra_element001  label="Ra_element : 1"  # scripted group (container) (typed FeaturePython)
  n = 1
  ref = Ra_element
FEATURE [App::DocumentObjectGroupPython] G4_Ra  # scripted group (container) (typed FeaturePython)
  Dunit = g/cm3
  Dvalue = 5
  Group = -> [Ra_element001]
  conduct = 2
  density = 1
  expand = 3
  formula = Ra
  name = G4_Ra
  specific = 4
FEATURE [App::DocumentObjectGroupPython] Ac_element001  label="Ac_element : 1"  # scripted group (container) (typed FeaturePython)
  n = 1
  ref = Ac_element
FEATURE [App::DocumentObjectGroupPython] G4_Ac  # scripted group (container) (typed FeaturePython)
  Dunit = g/cm3
  Dvalue = 10.07
  Group = -> [Ac_element001]
  conduct = 2
  density = 1
  expand = 3
  formula = Ac
  name = G4_Ac
  specific = 4
FEATURE [App::DocumentObjectGroupPython] Th_element001  label="Th_element : 1"  # scripted group (container) (typed FeaturePython)
  n = 1
  ref = Th_element
FEATURE [App::DocumentObjectGroupPython] G4_Th  # scripted group (container) (typed FeaturePython)
  Dunit = g/cm3
  Dvalue = 11.72
  Group = -> [Th_element001]
  conduct = 2
  density = 1
  expand = 3
  formula = Th
  name = G4_Th
  specific = 4
FEATURE [App::DocumentObjectGroupPython] Pa_element001  label="Pa_element : 1"  # scripted group (container) (typed FeaturePython)
  n = 1
  ref = Pa_element
FEATURE [App::DocumentObjectGroupPython] G4_Pa  # scripted group (container) (typed FeaturePython)
  Dunit = g/cm3
  Dvalue = 15.37
  Group = -> [Pa_element001]
  conduct = 2
  density = 1
  expand = 3
  formula = Pa
  name = G4_Pa
  specific = 4
FEATURE [App::DocumentObjectGroupPython] U_element004  label="U_element : 004"  # scripted group (container) (typed FeaturePython)
  n = 1
  ref = U_element
FEATURE [App::DocumentObjectGroupPython] G4_U  # scripted group (container) (typed FeaturePython)
  Dunit = g/cm3
  Dvalue = 18.95
  Group = -> [U_element004]
  conduct = 2
  density = 1
  expand = 3
  formula = U
  name = G4_U
  specific = 4
FEATURE [App::DocumentObjectGroupPython] Np_element001  label="Np_element : 1"  # scripted group (container) (typed FeaturePython)
  n = 1
  ref = Np_element
FEATURE [App::DocumentObjectGroupPython] G4_Np  # scripted group (container) (typed FeaturePython)
  Dunit = g/cm3
  Dvalue = 20.25
  Group = -> [Np_element001]
  conduct = 2
  density = 1
  expand = 3
  formula = Np
  name = G4_Np
  specific = 4
FEATURE [App::DocumentObjectGroupPython] Pu_element002  label="Pu_element : 002"  # scripted group (container) (typed FeaturePython)
  n = 1
  ref = Pu_element
FEATURE [App::DocumentObjectGroupPython] G4_Pu  # scripted group (container) (typed FeaturePython)
  Dunit = g/cm3
  Dvalue = 19.84
  Group = -> [Pu_element002]
  conduct = 2
  density = 1
  expand = 3
  formula = Pu
  name = G4_Pu
  specific = 4
FEATURE [App::DocumentObjectGroupPython] Am_element001  label="Am_element : 1"  # scripted group (container) (typed FeaturePython)
  n = 1
  ref = Am_element
FEATURE [App::DocumentObjectGroupPython] G4_Am  # scripted group (container) (typed FeaturePython)
  Dunit = g/cm3
  Dvalue = 13.67
  Group = -> [Am_element001]
  conduct = 2
  density = 1
  expand = 3
  formula = Am
  name = G4_Am
  specific = 4
FEATURE [App::DocumentObjectGroupPython] Cm_element001  label="Cm_element : 1"  # scripted group (container) (typed FeaturePython)
  n = 1
  ref = Cm_element
FEATURE [App::DocumentObjectGroupPython] G4_Cm  # scripted group (container) (typed FeaturePython)
  Dunit = g/cm3
  Dvalue = 13.51
  Group = -> [Cm_element001]
  conduct = 2
  density = 1
  expand = 3
  formula = Cm
  name = G4_Cm
  specific = 4
FEATURE [App::DocumentObjectGroupPython] Bk_element001  label="Bk_element : 1"  # scripted group (container) (typed FeaturePython)
  n = 1
  ref = Bk_element
FEATURE [App::DocumentObjectGroupPython] G4_Bk  # scripted group (container) (typed FeaturePython)
  Dunit = g/cm3
  Dvalue = 14
  Group = -> [Bk_element001]
  conduct = 2
  density = 1
  expand = 3
  formula = Bk
  name = G4_Bk
  specific = 4
FEATURE [App::DocumentObjectGroupPython] Cf_element001  label="Cf_element : 1"  # scripted group (container) (typed FeaturePython)
  n = 1
  ref = Cf_element
FEATURE [App::DocumentObjectGroupPython] G4_Cf  # scripted group (container) (typed FeaturePython)
  Dunit = g/cm3
  Dvalue = 10
  Group = -> [Cf_element001]
  conduct = 2
  density = 1
  expand = 3
  formula = Cf
  name = G4_Cf
  specific = 4
FEATURE [App::DocumentObjectGroupPython] Element  # scripted group (container) (typed FeaturePython)
  Group = -> [G4_H,G4_He,G4_Li,G4_Be,G4_B,G4_C,G4_N,G4_O,G4_F,G4_Ne,G4_Na,G4_Mg,G4_Al,G4_Si,G4_P,G4_S,G4_Cl,G4_Ar,G4_K,G4_Ca,G4_Sc,G4_Ti,G4_V,G4_Cr,G4_Mn,G4_Fe,G4_Co,G4_Ni,G4_Cu,G4_Zn,G4_Ga,G4_Ge,G4_As,G4_Se,G4_Br,G4_Kr,G4_Rb,G4_Sr,G4_Y,G4_Zr,G4_Nb,G4_Mo,G4_Tc,G4_Ru,G4_Rh,G4_Pd,G4_Ag,G4_Cd,G4_In,G4_Sn,G4_Sb,G4_Te,G4_I,G4_Xe,G4_Cs,G4_Ba,G4_La,G4_Ce,G4_Pr,G4_Nd,G4_Pm,G4_Sm,G4_Eu,G4_Gd,G4_Tb,G4_Dy,G4_Ho,G4_Er,+30 more]
FEATURE [App::DocumentObjectGroupPython] H_element114  label="H_element : 063"  # scripted group (container) (typed FeaturePython)
  n = 2
  ref = H_element
FEATURE [App::DocumentObjectGroupPython] G4_lH2  # scripted group (container) (typed FeaturePython)
  Dunit = g/cm3
  Dvalue = 0.0708
  Group = -> [H_element114]
  conduct = 2
  density = 1
  expand = 3
  formula = G4_lH2
  name = G4_lH2
  specific = 4
FEATURE [App::DocumentObjectGroupPython] N_element049  label="N_element : 022"  # scripted group (container) (typed FeaturePython)
  n = 2
  ref = N_element
FEATURE [App::DocumentObjectGroupPython] G4_lN2  # scripted group (container) (typed FeaturePython)
  Dunit = g/cm3
  Dvalue = 0.807
  Group = -> [N_element049]
  conduct = 2
  density = 1
  expand = 3
  formula = G4_lN2
  name = G4_lN2
  specific = 4
FEATURE [App::DocumentObjectGroupPython] O_element106  label="O_element : 060"  # scripted group (container) (typed FeaturePython)
  n = 2
  ref = O_element
FEATURE [App::DocumentObjectGroupPython] G4_lO2  # scripted group (container) (typed FeaturePython)
  Dunit = g/cm3
  Dvalue = 1.141
  Group = -> [O_element106]
  conduct = 2
  density = 1
  expand = 3
  formula = G4_lO2
  name = G4_lO2
  specific = 4
FEATURE [App::DocumentObjectGroupPython] Ar  label="Ar : 1"  # scripted group (container) (typed FeaturePython)
  n = 1
  ref = Ar
FEATURE [App::DocumentObjectGroupPython] G4_lAr  # scripted group (container) (typed FeaturePython)
  Dunit = g/cm3
  Dvalue = 1.396
  Group = -> [Ar]
  conduct = 2
  density = 1
  expand = 3
  formula = G4_lAr
  name = G4_lAr
  specific = 4
FEATURE [App::DocumentObjectGroupPython] Br  label="Br : 1"  # scripted group (container) (typed FeaturePython)
  n = 1
  ref = Br
FEATURE [App::DocumentObjectGroupPython] G4_lBr  # scripted group (container) (typed FeaturePython)
  Dunit = g/cm3
  Dvalue = 3.1028
  Group = -> [Br]
  conduct = 2
  density = 1
  expand = 3
  formula = G4_lBr
  name = G4_lBr
  specific = 4
FEATURE [App::DocumentObjectGroupPython] Kr  label="Kr : 1"  # scripted group (container) (typed FeaturePython)
  n = 1
  ref = Kr
FEATURE [App::DocumentObjectGroupPython] G4_lKr  # scripted group (container) (typed FeaturePython)
  Dunit = g/cm3
  Dvalue = 2.418
  Group = -> [Kr]
  conduct = 2
  density = 1
  expand = 3
  formula = G4_lKr
  name = G4_lKr
  specific = 4
FEATURE [App::DocumentObjectGroupPython] Xe  label="Xe : 1"  # scripted group (container) (typed FeaturePython)
  n = 1
  ref = Xe
FEATURE [App::DocumentObjectGroupPython] G4_lXe  # scripted group (container) (typed FeaturePython)
  Dunit = g/cm3
  Dvalue = 2.953
  Group = -> [Xe]
  conduct = 2
  density = 1
  expand = 3
  formula = G4_lXe
  name = G4_lXe
  specific = 4
FEATURE [App::DocumentObjectGroupPython] O_element107  label="O_element : 061"  # scripted group (container) (typed FeaturePython)
  n = 4
  ref = O_element
FEATURE [App::DocumentObjectGroupPython] Pb_element004  label="Pb_element : 002"  # scripted group (container) (typed FeaturePython)
  n = 1
  ref = Pb_element
FEATURE [App::DocumentObjectGroupPython] W_element005  label="W_element : 005"  # scripted group (container) (typed FeaturePython)
  n = 1
  ref = W_element
FEATURE [App::DocumentObjectGroupPython] G4_PbWO4  # scripted group (container) (typed FeaturePython)
  Dunit = g/cm3
  Dvalue = 8.28
  Group = -> [O_element107,Pb_element004,W_element005]
  conduct = 2
  density = 1
  expand = 3
  formula = G4_PbWO4
  name = G4_PbWO4
  specific = 4
FEATURE [App::DocumentObjectGroupPython] alactic  label="alactic : 1"  # scripted group (container) (typed FeaturePython)
  n = 1
  ref = alactic
FEATURE [App::DocumentObjectGroupPython] G4_Galactic  # scripted group (container) (typed FeaturePython)
  Dunit = g/cm3
  Dvalue = 0
  Group = -> [alactic]
  conduct = 2
  density = 1
  expand = 3
  formula = G4_Galactic
  name = G4_Galactic
  specific = 4
FEATURE [App::DocumentObjectGroupPython] RAPHITE_POROUS  label="RAPHITE_POROUS : 1"  # scripted group (container) (typed FeaturePython)
  n = 1
  ref = RAPHITE_POROUS
FEATURE [App::DocumentObjectGroupPython] G4_GRAPHITE_POROUS  # scripted group (container) (typed FeaturePython)
  Dunit = g/cm3
  Dvalue = 1.7
  Group = -> [RAPHITE_POROUS]
  conduct = 2
  density = 1
  expand = 3
  formula = G4_GRAPHITE_POROUS
  name = G4_GRAPHITE_POROUS
  specific = 4
FEATURE [App::DocumentObjectGroupPython] H_element115  label="H_element : 0.150"  # scripted group (container) (typed FeaturePython)
  n = 0.080538
FEATURE [App::DocumentObjectGroupPython] C_element125  label="C_element : 0.600"  # scripted group (container) (typed FeaturePython)
  n = 0.599848
FEATURE [App::DocumentObjectGroupPython] O_element108  label="O_element : 0.320"  # scripted group (container) (typed FeaturePython)
  n = 0.319614
FEATURE [App::DocumentObjectGroupPython] G4_LUCITE  # scripted group (container) (typed FeaturePython)
  Dunit = g/cm3
  Dvalue = 1.19
  Group = -> [H_element115,C_element125,O_element108]
  conduct = 2
  density = 1
  expand = 3
  formula = G4_LUCITE
  name = G4_LUCITE
  specific = 4
FEATURE [App::DocumentObjectGroupPython] Cu_element002  label="Cu_element : 62"  # scripted group (container) (typed FeaturePython)
  n = 62
  ref = Cu_element
FEATURE [App::DocumentObjectGroupPython] Zn_element002  label="Zn_element : 35"  # scripted group (container) (typed FeaturePython)
  n = 35
  ref = Zn_element
FEATURE [App::DocumentObjectGroupPython] Pb_element005  label="Pb_element : 3"  # scripted group (container) (typed FeaturePython)
  n = 3
  ref = Pb_element
FEATURE [App::DocumentObjectGroupPython] G4_BRASS  # scripted group (container) (typed FeaturePython)
  Dunit = g/cm3
  Dvalue = 8.52
  Group = -> [Cu_element002,Zn_element002,Pb_element005]
  conduct = 2
  density = 1
  expand = 3
  formula = G4_BRASS
  name = G4_BRASS
  specific = 4
FEATURE [App::DocumentObjectGroupPython] Cu_element003  label="Cu_element : 89"  # scripted group (container) (typed FeaturePython)
  n = 89
  ref = Cu_element
FEATURE [App::DocumentObjectGroupPython] Zn_element003  label="Zn_element : 9"  # scripted group (container) (typed FeaturePython)
  n = 9
  ref = Zn_element
FEATURE [App::DocumentObjectGroupPython] Pb_element006  label="Pb_element : 2"  # scripted group (container) (typed FeaturePython)
  n = 2
  ref = Pb_element
FEATURE [App::DocumentObjectGroupPython] G4_BRONZE  # scripted group (container) (typed FeaturePython)
  Dunit = g/cm3
  Dvalue = 8.82
  Group = -> [Cu_element003,Zn_element003,Pb_element006]
  conduct = 2
  density = 1
  expand = 3
  formula = G4_BRONZE
  name = G4_BRONZE
  specific = 4
FEATURE [App::DocumentObjectGroupPython] Fe_element008  label="Fe_element : 74"  # scripted group (container) (typed FeaturePython)
  n = 74
  ref = Fe_element
FEATURE [App::DocumentObjectGroupPython] Cr_element002  label="Cr_element : 18"  # scripted group (container) (typed FeaturePython)
  n = 18
  ref = Cr_element
FEATURE [App::DocumentObjectGroupPython] Ni_element002  label="Ni_element : 8"  # scripted group (container) (typed FeaturePython)
  n = 8
  ref = Ni_element
FEATURE [App::DocumentObjectGroupPython] G4_STAINLESS_STEEL  label="G4_STAINLESS-STEEL"  # scripted group (container) (typed FeaturePython)
  Dunit = g/cm3
  Dvalue = 8
  Group = -> [Fe_element008,Cr_element002,Ni_element002]
  conduct = 2
  density = 1
  expand = 3
  formula = G4_STAINLESS-STEEL
  name = G4_STAINLESS-STEEL
  specific = 4
FEATURE [App::DocumentObjectGroupPython] H_element116  label="H_element : 064"  # scripted group (container) (typed FeaturePython)
  n = 18
  ref = H_element
FEATURE [App::DocumentObjectGroupPython] C_element126  label="C_element : 071"  # scripted group (container) (typed FeaturePython)
  n = 12
  ref = C_element
FEATURE [App::DocumentObjectGroupPython] O_element109  label="O_element : 062"  # scripted group (container) (typed FeaturePython)
  n = 7
  ref = O_element
FEATURE [App::DocumentObjectGroupPython] G4_CR39  # scripted group (container) (typed FeaturePython)
  Dunit = g/cm3
  Dvalue = 1.32
  Group = -> [H_element116,C_element126,O_element109]
  conduct = 2
  density = 1
  expand = 3
  formula = G4_CR39
  name = G4_CR39
  specific = 4
FEATURE [App::DocumentObjectGroupPython] H_element117  label="H_element : 38"  # scripted group (container) (typed FeaturePython)
  n = 38
  ref = H_element
FEATURE [App::DocumentObjectGroupPython] C_element127  label="C_element : 072"  # scripted group (container) (typed FeaturePython)
  n = 18
  ref = C_element
FEATURE [App::DocumentObjectGroupPython] O_element110  label="O_element : 063"  # scripted group (container) (typed FeaturePython)
  n = 1
  ref = O_element
FEATURE [App::DocumentObjectGroupPython] G4_OCTADECANOL  # scripted group (container) (typed FeaturePython)
  Dunit = g/cm3
  Dvalue = 0.812
  Group = -> [H_element117,C_element127,O_element110]
  conduct = 2
  density = 1
  expand = 3
  formula = G4_OCTADECANOL
  name = G4_OCTADECANOL
  specific = 4
FEATURE [App::DocumentObjectGroupPython] HEP  # scripted group (container) (typed FeaturePython)
  Group = -> [G4_lH2,G4_lN2,G4_lO2,G4_lAr,G4_lBr,G4_lKr,G4_lXe,G4_PbWO4,G4_Galactic,G4_GRAPHITE_POROUS,G4_LUCITE,G4_BRASS,G4_BRONZE,G4_STAINLESS_STEEL,G4_CR39,G4_OCTADECANOL]
FEATURE [App::DocumentObjectGroupPython] C_element128  label="C_element : 073"  # scripted group (container) (typed FeaturePython)
  n = 14
  ref = C_element
FEATURE [App::DocumentObjectGroupPython] H_element118  label="H_element : 065"  # scripted group (container) (typed FeaturePython)
  n = 10
  ref = H_element
FEATURE [App::DocumentObjectGroupPython] O_element111  label="O_element : 064"  # scripted group (container) (typed FeaturePython)
  n = 2
  ref = O_element
FEATURE [App::DocumentObjectGroupPython] N_element050  label="N_element : 023"  # scripted group (container) (typed FeaturePython)
  n = 2
  ref = N_element
FEATURE [App::DocumentObjectGroupPython] G4_KEVLAR  # scripted group (container) (typed FeaturePython)
  Dunit = g/cm3
  Dvalue = 1.44
  Group = -> [C_element128,H_element118,O_element111,N_element050]
  conduct = 2
  density = 1
  expand = 3
  formula = G4_KEVLAR
  name = G4_KEVLAR
  specific = 4
FEATURE [App::DocumentObjectGroupPython] C_element129  label="C_element : 074"  # scripted group (container) (typed FeaturePython)
  n = 10
  ref = C_element
FEATURE [App::DocumentObjectGroupPython] H_element119  label="H_element : 066"  # scripted group (container) (typed FeaturePython)
  n = 8
  ref = H_element
FEATURE [App::DocumentObjectGroupPython] O_element112  label="O_element : 065"  # scripted group (container) (typed FeaturePython)
  n = 4
  ref = O_element
FEATURE [App::DocumentObjectGroupPython] G4_DACRON  # scripted group (container) (typed FeaturePython)
  Dunit = g/cm3
  Dvalue = 1.4
  Group = -> [C_element129,H_element119,O_element112]
  conduct = 2
  density = 1
  expand = 3
  formula = G4_DACRON
  name = G4_DACRON
  specific = 4
FEATURE [App::DocumentObjectGroupPython] C_element130  label="C_element : 075"  # scripted group (container) (typed FeaturePython)
  n = 4
  ref = C_element
FEATURE [App::DocumentObjectGroupPython] H_element120  label="H_element : 067"  # scripted group (container) (typed FeaturePython)
  n = 5
  ref = H_element
FEATURE [App::DocumentObjectGroupPython] Cl_element030  label="Cl_element : 016"  # scripted group (container) (typed FeaturePython)
  n = 1
  ref = Cl_element
FEATURE [App::DocumentObjectGroupPython] G4_NEOPRENE  # scripted group (container) (typed FeaturePython)
  Dunit = g/cm3
  Dvalue = 1.23
  Group = -> [C_element130,H_element120,Cl_element030]
  conduct = 2
  density = 1
  expand = 3
  formula = G4_NEOPRENE
  name = G4_NEOPRENE
  specific = 4
FEATURE [App::DocumentObjectGroupPython] Space  # scripted group (container) (typed FeaturePython)
  Group = -> [G4_KEVLAR,G4_DACRON,G4_NEOPRENE]
FEATURE [App::DocumentObjectGroupPython] H_element121  label="H_element : 068"  # scripted group (container) (typed FeaturePython)
  n = 5
  ref = H_element
FEATURE [App::DocumentObjectGroupPython] C_element131  label="C_element : 076"  # scripted group (container) (typed FeaturePython)
  n = 4
  ref = C_element
FEATURE [App::DocumentObjectGroupPython] N_element051  label="N_element : 3"  # scripted group (container) (typed FeaturePython)
  n = 3
  ref = N_element
FEATURE [App::DocumentObjectGroupPython] O_element113  label="O_element : 066"  # scripted group (container) (typed FeaturePython)
  n = 1
  ref = O_element
FEATURE [App::DocumentObjectGroupPython] G4_CYTOSINE  # scripted group (container) (typed FeaturePython)
  Dunit = g/cm3
  Dvalue = 1.55
  Group = -> [H_element121,C_element131,N_element051,O_element113]
  conduct = 2
  density = 1
  expand = 3
  formula = G4_CYTOSINE
  name = G4_CYTOSINE
  specific = 4
FEATURE [App::DocumentObjectGroupPython] H_element122  label="H_element : 069"  # scripted group (container) (typed FeaturePython)
  n = 6
  ref = H_element
FEATURE [App::DocumentObjectGroupPython] C_element132  label="C_element : 077"  # scripted group (container) (typed FeaturePython)
  n = 5
  ref = C_element
FEATURE [App::DocumentObjectGroupPython] N_element052  label="N_element : 024"  # scripted group (container) (typed FeaturePython)
  n = 2
  ref = N_element
FEATURE [App::DocumentObjectGroupPython] O_element114  label="O_element : 067"  # scripted group (container) (typed FeaturePython)
  n = 2
  ref = O_element
FEATURE [App::DocumentObjectGroupPython] G4_THYMINE  # scripted group (container) (typed FeaturePython)
  Dunit = g/cm3
  Dvalue = 1.23
  Group = -> [H_element122,C_element132,N_element052,O_element114]
  conduct = 2
  density = 1
  expand = 3
  formula = G4_THYMINE
  name = G4_THYMINE
  specific = 4
FEATURE [App::DocumentObjectGroupPython] H_element123  label="H_element : 070"  # scripted group (container) (typed FeaturePython)
  n = 4
  ref = H_element
FEATURE [App::DocumentObjectGroupPython] C_element133  label="C_element : 078"  # scripted group (container) (typed FeaturePython)
  n = 4
  ref = C_element
FEATURE [App::DocumentObjectGroupPython] N_element053  label="N_element : 025"  # scripted group (container) (typed FeaturePython)
  n = 2
  ref = N_element
FEATURE [App::DocumentObjectGroupPython] O_element115  label="O_element : 068"  # scripted group (container) (typed FeaturePython)
  n = 2
  ref = O_element
FEATURE [App::DocumentObjectGroupPython] G4_URACIL  # scripted group (container) (typed FeaturePython)
  Dunit = g/cm3
  Dvalue = 1.32
  Group = -> [H_element123,C_element133,N_element053,O_element115]
  conduct = 2
  density = 1
  expand = 3
  formula = G4_URACIL
  name = G4_URACIL
  specific = 4
FEATURE [App::DocumentObjectGroupPython] H_element124  label="H_element : 071"  # scripted group (container) (typed FeaturePython)
  n = 4
  ref = H_element
FEATURE [App::DocumentObjectGroupPython] C_element134  label="C_element : 079"  # scripted group (container) (typed FeaturePython)
  n = 5
  ref = C_element
FEATURE [App::DocumentObjectGroupPython] N_element054  label="N_element : 026"  # scripted group (container) (typed FeaturePython)
  n = 5
  ref = N_element
FEATURE [App::DocumentObjectGroupPython] G4_DNA_ADENINE  # scripted group (container) (typed FeaturePython)
  Dunit = g/cm3
  Dvalue = 1
  Group = -> [H_element124,C_element134,N_element054]
  conduct = 2
  density = 1
  expand = 3
  formula = G4_DNA_ADENINE
  name = G4_DNA_ADENINE
  specific = 4
FEATURE [App::DocumentObjectGroupPython] H_element125  label="H_element : 072"  # scripted group (container) (typed FeaturePython)
  n = 4
  ref = H_element
FEATURE [App::DocumentObjectGroupPython] C_element135  label="C_element : 080"  # scripted group (container) (typed FeaturePython)
  n = 5
  ref = C_element
FEATURE [App::DocumentObjectGroupPython] N_element055  label="N_element : 027"  # scripted group (container) (typed FeaturePython)
  n = 5
  ref = N_element
FEATURE [App::DocumentObjectGroupPython] O_element116  label="O_element : 069"  # scripted group (container) (typed FeaturePython)
  n = 1
  ref = O_element
FEATURE [App::DocumentObjectGroupPython] G4_DNA_GUANINE  # scripted group (container) (typed FeaturePython)
  Dunit = g/cm3
  Dvalue = 1
  Group = -> [H_element125,C_element135,N_element055,O_element116]
  conduct = 2
  density = 1
  expand = 3
  formula = G4_DNA_GUANINE
  name = G4_DNA_GUANINE
  specific = 4
FEATURE [App::DocumentObjectGroupPython] H_element126  label="H_element : 073"  # scripted group (container) (typed FeaturePython)
  n = 4
  ref = H_element
FEATURE [App::DocumentObjectGroupPython] C_element136  label="C_element : 081"  # scripted group (container) (typed FeaturePython)
  n = 4
  ref = C_element
FEATURE [App::DocumentObjectGroupPython] N_element056  label="N_element : 028"  # scripted group (container) (typed FeaturePython)
  n = 3
  ref = N_element
FEATURE [App::DocumentObjectGroupPython] O_element117  label="O_element : 070"  # scripted group (container) (typed FeaturePython)
  n = 1
  ref = O_element
FEATURE [App::DocumentObjectGroupPython] G4_DNA_CYTOSINE  # scripted group (container) (typed FeaturePython)
  Dunit = g/cm3
  Dvalue = 1
  Group = -> [H_element126,C_element136,N_element056,O_element117]
  conduct = 2
  density = 1
  expand = 3
  formula = G4_DNA_CYTOSINE
  name = G4_DNA_CYTOSINE
  specific = 4
FEATURE [App::DocumentObjectGroupPython] H_element127  label="H_element : 074"  # scripted group (container) (typed FeaturePython)
  n = 5
  ref = H_element
FEATURE [App::DocumentObjectGroupPython] C_element137  label="C_element : 082"  # scripted group (container) (typed FeaturePython)
  n = 5
  ref = C_element
FEATURE [App::DocumentObjectGroupPython] N_element057  label="N_element : 029"  # scripted group (container) (typed FeaturePython)
  n = 2
  ref = N_element
FEATURE [App::DocumentObjectGroupPython] O_element118  label="O_element : 071"  # scripted group (container) (typed FeaturePython)
  n = 2
  ref = O_element
FEATURE [App::DocumentObjectGroupPython] G4_DNA_THYMINE  # scripted group (container) (typed FeaturePython)
  Dunit = g/cm3
  Dvalue = 1
  Group = -> [H_element127,C_element137,N_element057,O_element118]
  conduct = 2
  density = 1
  expand = 3
  formula = G4_DNA_THYMINE
  name = G4_DNA_THYMINE
  specific = 4
FEATURE [App::DocumentObjectGroupPython] H_element128  label="H_element : 075"  # scripted group (container) (typed FeaturePython)
  n = 3
  ref = H_element
FEATURE [App::DocumentObjectGroupPython] C_element138  label="C_element : 083"  # scripted group (container) (typed FeaturePython)
  n = 4
  ref = C_element
FEATURE [App::DocumentObjectGroupPython] N_element058  label="N_element : 030"  # scripted group (container) (typed FeaturePython)
  n = 2
  ref = N_element
FEATURE [App::DocumentObjectGroupPython] O_element119  label="O_element : 072"  # scripted group (container) (typed FeaturePython)
  n = 2
  ref = O_element
FEATURE [App::DocumentObjectGroupPython] G4_DNA_URACIL  # scripted group (container) (typed FeaturePython)
  Dunit = g/cm3
  Dvalue = 1
  Group = -> [H_element128,C_element138,N_element058,O_element119]
  conduct = 2
  density = 1
  expand = 3
  formula = G4_DNA_URACIL
  name = G4_DNA_URACIL
  specific = 4
FEATURE [App::DocumentObjectGroupPython] H_element129  label="H_element : 076"  # scripted group (container) (typed FeaturePython)
  n = 10
  ref = H_element
FEATURE [App::DocumentObjectGroupPython] C_element139  label="C_element : 084"  # scripted group (container) (typed FeaturePython)
  n = 10
  ref = C_element
FEATURE [App::DocumentObjectGroupPython] N_element059  label="N_element : 031"  # scripted group (container) (typed FeaturePython)
  n = 5
  ref = N_element
FEATURE [App::DocumentObjectGroupPython] O_element120  label="O_element : 073"  # scripted group (container) (typed FeaturePython)
  n = 4
  ref = O_element
FEATURE [App::DocumentObjectGroupPython] G4_DNA_ADENOSINE  # scripted group (container) (typed FeaturePython)
  Dunit = g/cm3
  Dvalue = 1
  Group = -> [H_element129,C_element139,N_element059,O_element120]
  conduct = 2
  density = 1
  expand = 3
  formula = G4_DNA_ADENOSINE
  name = G4_DNA_ADENOSINE
  specific = 4
FEATURE [App::DocumentObjectGroupPython] H_element130  label="H_element : 077"  # scripted group (container) (typed FeaturePython)
  n = 10
  ref = H_element
FEATURE [App::DocumentObjectGroupPython] C_element140  label="C_element : 085"  # scripted group (container) (typed FeaturePython)
  n = 10
  ref = C_element
FEATURE [App::DocumentObjectGroupPython] N_element060  label="N_element : 032"  # scripted group (container) (typed FeaturePython)
  n = 5
  ref = N_element
FEATURE [App::DocumentObjectGroupPython] O_element121  label="O_element : 074"  # scripted group (container) (typed FeaturePython)
  n = 5
  ref = O_element
FEATURE [App::DocumentObjectGroupPython] G4_DNA_GUANOSINE  # scripted group (container) (typed FeaturePython)
  Dunit = g/cm3
  Dvalue = 1
  Group = -> [H_element130,C_element140,N_element060,O_element121]
  conduct = 2
  density = 1
  expand = 3
  formula = G4_DNA_GUANOSINE
  name = G4_DNA_GUANOSINE
  specific = 4
FEATURE [App::DocumentObjectGroupPython] H_element131  label="H_element : 078"  # scripted group (container) (typed FeaturePython)
  n = 10
  ref = H_element
FEATURE [App::DocumentObjectGroupPython] C_element141  label="C_element : 086"  # scripted group (container) (typed FeaturePython)
  n = 9
  ref = C_element
FEATURE [App::DocumentObjectGroupPython] N_element061  label="N_element : 033"  # scripted group (container) (typed FeaturePython)
  n = 3
  ref = N_element
FEATURE [App::DocumentObjectGroupPython] O_element122  label="O_element : 075"  # scripted group (container) (typed FeaturePython)
  n = 5
  ref = O_element
FEATURE [App::DocumentObjectGroupPython] G4_DNA_CYTIDINE  # scripted group (container) (typed FeaturePython)
  Dunit = g/cm3
  Dvalue = 1
  Group = -> [H_element131,C_element141,N_element061,O_element122]
  conduct = 2
  density = 1
  expand = 3
  formula = G4_DNA_CYTIDINE
  name = G4_DNA_CYTIDINE
  specific = 4
FEATURE [App::DocumentObjectGroupPython] H_element132  label="H_element : 079"  # scripted group (container) (typed FeaturePython)
  n = 9
  ref = H_element
FEATURE [App::DocumentObjectGroupPython] C_element142  label="C_element : 087"  # scripted group (container) (typed FeaturePython)
  n = 9
  ref = C_element
FEATURE [App::DocumentObjectGroupPython] N_element062  label="N_element : 034"  # scripted group (container) (typed FeaturePython)
  n = 2
  ref = N_element
FEATURE [App::DocumentObjectGroupPython] O_element123  label="O_element : 076"  # scripted group (container) (typed FeaturePython)
  n = 6
  ref = O_element
FEATURE [App::DocumentObjectGroupPython] G4_DNA_URIDINE  # scripted group (container) (typed FeaturePython)
  Dunit = g/cm3
  Dvalue = 1
  Group = -> [H_element132,C_element142,N_element062,O_element123]
  conduct = 2
  density = 1
  expand = 3
  formula = G4_DNA_URIDINE
  name = G4_DNA_URIDINE
  specific = 4
FEATURE [App::DocumentObjectGroupPython] H_element133  label="H_element : 080"  # scripted group (container) (typed FeaturePython)
  n = 11
  ref = H_element
FEATURE [App::DocumentObjectGroupPython] C_element143  label="C_element : 088"  # scripted group (container) (typed FeaturePython)
  n = 10
  ref = C_element
FEATURE [App::DocumentObjectGroupPython] N_element063  label="N_element : 035"  # scripted group (container) (typed FeaturePython)
  n = 2
  ref = N_element
FEATURE [App::DocumentObjectGroupPython] O_element124  label="O_element : 077"  # scripted group (container) (typed FeaturePython)
  n = 6
  ref = O_element
FEATURE [App::DocumentObjectGroupPython] G4_DNA_METHYLURIDINE  # scripted group (container) (typed FeaturePython)
  Dunit = g/cm3
  Dvalue = 1
  Group = -> [H_element133,C_element143,N_element063,O_element124]
  conduct = 2
  density = 1
  expand = 3
  formula = G4_DNA_METHYLURIDINE
  name = G4_DNA_METHYLURIDINE
  specific = 4
FEATURE [App::DocumentObjectGroupPython] P_element014  label="P_element : 003"  # scripted group (container) (typed FeaturePython)
  n = 1
  ref = P_element
FEATURE [App::DocumentObjectGroupPython] O_element125  label="O_element : 078"  # scripted group (container) (typed FeaturePython)
  n = 3
  ref = O_element
FEATURE [App::DocumentObjectGroupPython] G4_DNA_MONOPHOSPHATE  # scripted group (container) (typed FeaturePython)
  Dunit = g/cm3
  Dvalue = 1
  Group = -> [P_element014,O_element125]
  conduct = 2
  density = 1
  expand = 3
  formula = G4_DNA_MONOPHOSPHATE
  name = G4_DNA_MONOPHOSPHATE
  specific = 4
FEATURE [App::DocumentObjectGroupPython] H_element134  label="H_element : 081"  # scripted group (container) (typed FeaturePython)
  n = 10
  ref = H_element
FEATURE [App::DocumentObjectGroupPython] C_element144  label="C_element : 089"  # scripted group (container) (typed FeaturePython)
  n = 10
  ref = C_element
FEATURE [App::DocumentObjectGroupPython] N_element064  label="N_element : 036"  # scripted group (container) (typed FeaturePython)
  n = 5
  ref = N_element
FEATURE [App::DocumentObjectGroupPython] O_element126  label="O_element : 079"  # scripted group (container) (typed FeaturePython)
  n = 7
  ref = O_element
FEATURE [App::DocumentObjectGroupPython] P_element015  label="P_element : 004"  # scripted group (container) (typed FeaturePython)
  n = 1
  ref = P_element
FEATURE [App::DocumentObjectGroupPython] G4_DNA_A  # scripted group (container) (typed FeaturePython)
  Dunit = g/cm3
  Dvalue = 1
  Group = -> [H_element134,C_element144,N_element064,O_element126,P_element015]
  conduct = 2
  density = 1
  expand = 3
  formula = G4_DNA_A
  name = G4_DNA_A
  specific = 4
FEATURE [App::DocumentObjectGroupPython] H_element135  label="H_element : 082"  # scripted group (container) (typed FeaturePython)
  n = 10
  ref = H_element
FEATURE [App::DocumentObjectGroupPython] C_element145  label="C_element : 090"  # scripted group (container) (typed FeaturePython)
  n = 10
  ref = C_element
FEATURE [App::DocumentObjectGroupPython] N_element065  label="N_element : 037"  # scripted group (container) (typed FeaturePython)
  n = 5
  ref = N_element
FEATURE [App::DocumentObjectGroupPython] O_element127  label="O_element : 8"  # scripted group (container) (typed FeaturePython)
  n = 8
  ref = O_element
FEATURE [App::DocumentObjectGroupPython] P_element016  label="P_element : 005"  # scripted group (container) (typed FeaturePython)
  n = 1
  ref = P_element
FEATURE [App::DocumentObjectGroupPython] G4_DNA_G  # scripted group (container) (typed FeaturePython)
  Dunit = g/cm3
  Dvalue = 1
  Group = -> [H_element135,C_element145,N_element065,O_element127,P_element016]
  conduct = 2
  density = 1
  expand = 3
  formula = G4_DNA_G
  name = G4_DNA_G
  specific = 4
FEATURE [App::DocumentObjectGroupPython] H_element136  label="H_element : 083"  # scripted group (container) (typed FeaturePython)
  n = 10
  ref = H_element
FEATURE [App::DocumentObjectGroupPython] C_element146  label="C_element : 091"  # scripted group (container) (typed FeaturePython)
  n = 9
  ref = C_element
FEATURE [App::DocumentObjectGroupPython] N_element066  label="N_element : 038"  # scripted group (container) (typed FeaturePython)
  n = 3
  ref = N_element
FEATURE [App::DocumentObjectGroupPython] O_element128  label="O_element : 080"  # scripted group (container) (typed FeaturePython)
  n = 8
  ref = O_element
FEATURE [App::DocumentObjectGroupPython] P_element017  label="P_element : 006"  # scripted group (container) (typed FeaturePython)
  n = 1
  ref = P_element
FEATURE [App::DocumentObjectGroupPython] G4_DNA_C  # scripted group (container) (typed FeaturePython)
  Dunit = g/cm3
  Dvalue = 1
  Group = -> [H_element136,C_element146,N_element066,O_element128,P_element017]
  conduct = 2
  density = 1
  expand = 3
  formula = G4_DNA_C
  name = G4_DNA_C
  specific = 4
FEATURE [App::DocumentObjectGroupPython] H_element137  label="H_element : 084"  # scripted group (container) (typed FeaturePython)
  n = 9
  ref = H_element
FEATURE [App::DocumentObjectGroupPython] C_element147  label="C_element : 092"  # scripted group (container) (typed FeaturePython)
  n = 9
  ref = C_element
FEATURE [App::DocumentObjectGroupPython] N_element067  label="N_element : 039"  # scripted group (container) (typed FeaturePython)
  n = 2
  ref = N_element
FEATURE [App::DocumentObjectGroupPython] O_element129  label="O_element : 9"  # scripted group (container) (typed FeaturePython)
  n = 9
  ref = O_element
FEATURE [App::DocumentObjectGroupPython] P_element018  label="P_element : 007"  # scripted group (container) (typed FeaturePython)
  n = 1
  ref = P_element
FEATURE [App::DocumentObjectGroupPython] G4_DNA_U  # scripted group (container) (typed FeaturePython)
  Dunit = g/cm3
  Dvalue = 1
  Group = -> [H_element137,C_element147,N_element067,O_element129,P_element018]
  conduct = 2
  density = 1
  expand = 3
  formula = G4_DNA_U
  name = G4_DNA_U
  specific = 4
FEATURE [App::DocumentObjectGroupPython] H_element138  label="H_element : 085"  # scripted group (container) (typed FeaturePython)
  n = 11
  ref = H_element
FEATURE [App::DocumentObjectGroupPython] C_element148  label="C_element : 093"  # scripted group (container) (typed FeaturePython)
  n = 10
  ref = C_element
FEATURE [App::DocumentObjectGroupPython] N_element068  label="N_element : 040"  # scripted group (container) (typed FeaturePython)
  n = 2
  ref = N_element
FEATURE [App::DocumentObjectGroupPython] O_element130  label="O_element : 081"  # scripted group (container) (typed FeaturePython)
  n = 9
  ref = O_element
FEATURE [App::DocumentObjectGroupPython] P_element019  label="P_element : 008"  # scripted group (container) (typed FeaturePython)
  n = 1
  ref = P_element
FEATURE [App::DocumentObjectGroupPython] G4_DNA_MU  # scripted group (container) (typed FeaturePython)
  Dunit = g/cm3
  Dvalue = 1
  Group = -> [H_element138,C_element148,N_element068,O_element130,P_element019]
  conduct = 2
  density = 1
  expand = 3
  formula = G4_DNA_MU
  name = G4_DNA_MU
  specific = 4
FEATURE [App::DocumentObjectGroupPython] BioChemical  # scripted group (container) (typed FeaturePython)
  Group = -> [G4_CYTOSINE,G4_THYMINE,G4_URACIL,G4_DNA_ADENINE,G4_DNA_GUANINE,G4_DNA_CYTOSINE,G4_DNA_THYMINE,G4_DNA_URACIL,G4_DNA_ADENOSINE,G4_DNA_GUANOSINE,G4_DNA_CYTIDINE,G4_DNA_URIDINE,G4_DNA_METHYLURIDINE,G4_DNA_MONOPHOSPHATE,G4_DNA_A,G4_DNA_G,G4_DNA_C,G4_DNA_U,G4_DNA_MU]
FEATURE [App::DocumentObjectGroupPython] G4Materials  # scripted group (container) (typed FeaturePython)
  Group = -> [NIST,Element,HEP,Space,BioChemical]
  version = 1
FEATURE [App::DocumentObjectGroupPython] Geant4  # scripted group (container) (typed FeaturePython)
  Group = -> [G4Isotopes,G4Elements,G4Materials]
FEATURE [App::DocumentObjectGroupPython] Materials  # scripted group (container) (typed FeaturePython)
  Group = -> [Geant4]
FEATURE [Part::FeaturePython] GDMLBox_WorldBox  # WARN: FeaturePython — macro-defined, semantics opaque (R4)
  lunit = 2
  material = 5
  x = 130
  y = 243.533
  z = 141.597
FEATURE [Part::Part2DObjectPython] Circle  # Draft 2D object (typed FeaturePython)
  Area = 5026.55
  FirstAngle = 0
  LastAngle = 0
  MakeFace = true
  Placement = pos=(-6.62621,-53.6724,-16.5942) rot=(-0.574466,0.143177,0.805909;3.50816rad)
  Radius = 40
FEATURE [Part::FeaturePython] GDMLBox_Box  # WARN: FeaturePython — macro-defined, semantics opaque (R4)
  lunit = 2
  material = 0
  x = 10
  y = 10
  z = 10
FEATURE [App::Part] LV_Box001
  Group = -> [GDMLBox_Box,Circle]
  Origin = -> Origin002
FEATURE [App::Part] worldVOL
  Group = -> [GDMLBox_WorldBox,LV_Box001]
  Origin = -> Origin
FEATURE [Part::FeaturePython] PathArray  # WARN: FeaturePython — macro-defined, semantics opaque (R4)
  Align = false
  AlignMode = 0
  Base = -> GDMLBox_Box
  Count = 4
  EndOffset = 0
  ExtraTranslation = (0,0,0)
  ForceVertical = false
  Fuse = false
  PathObject = -> Circle
  StartOffset = 0
  TangentVector = (1,0,0)
  VerticalVector = (0,0,1)
